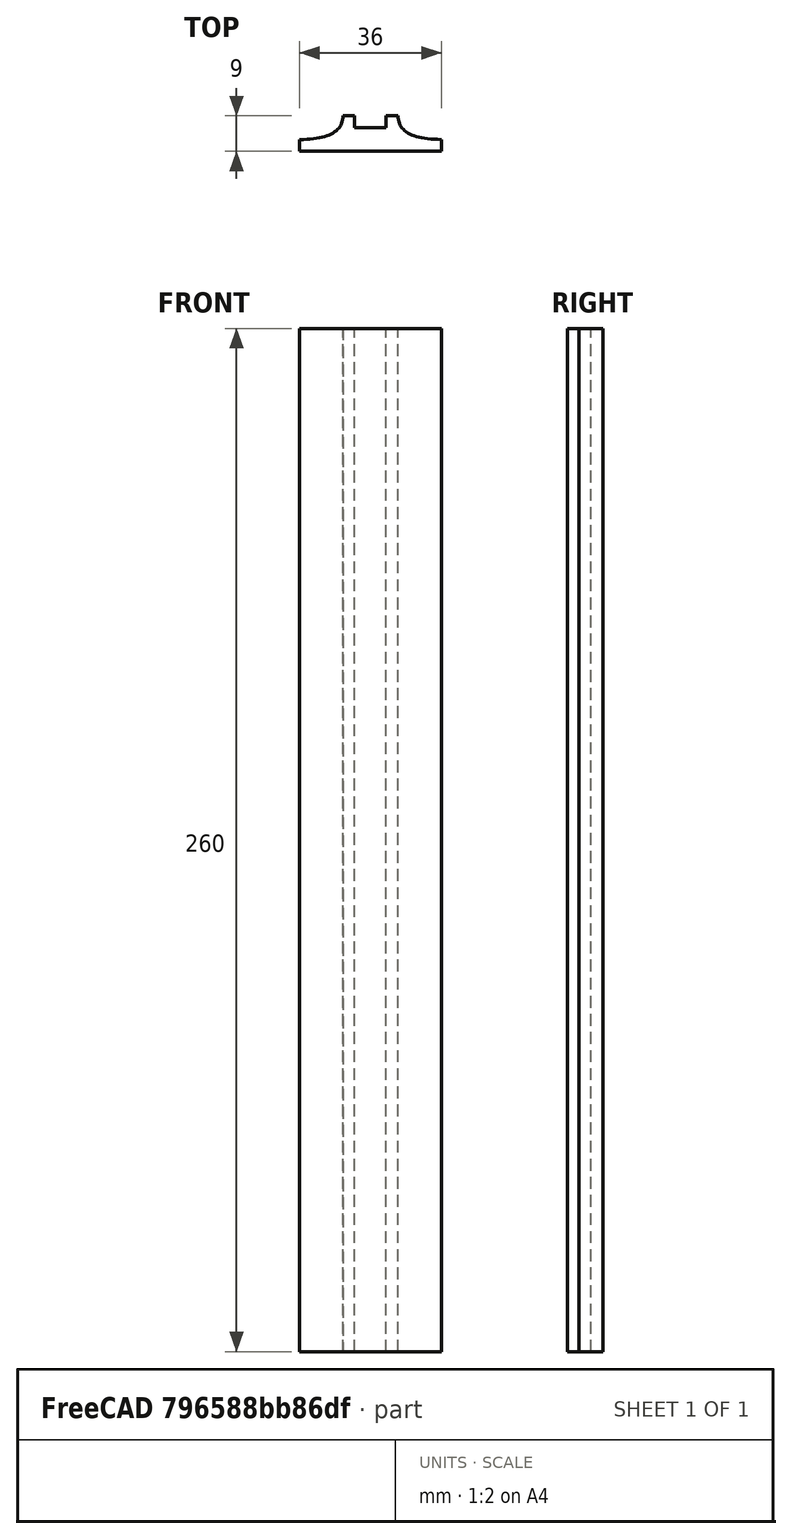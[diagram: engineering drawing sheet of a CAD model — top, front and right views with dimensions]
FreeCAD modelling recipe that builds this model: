
FCSTD DOCUMENT  (FreeCAD 0.19R0.19.2)
Label: laptopStand293.FCStd
License: All rights reserved
LicenseURL: http://en.wikipedia.org/wiki/All_rights_reserved
objects: Sketcher::SketchObject×10, Part::Extrusion×1
note: 11 computed .brp shape members not serialized (recipe doc carries the construction recipe); baked Part::Feature solids carry a one-line shape summary decoded from their .brp

FEATURE [Sketcher::SketchObject] Sketch001  label="legTop"
  FullyConstrained = false
  MapMode = 4
  Placement = pos=(0,0,0) rot=(0.57735,0.57735,0.57735;2.0944rad)
  sketch-geometry (59):
    g0: BSplineCurve PolesCount=3 KnotsCount=2 Degree=2 IsPeriodic=0
    g1: ArcOfCircle CenterX=73.1223 CenterY=-32.291 CenterZ=0 NormalX=0 NormalY=0 NormalZ=1 AngleXU=0 Radius=13 StartAngle=5.92268 EndAngle=9.06428
    g2: ArcOfCircle CenterX=66.7816 CenterY=-49.1439 CenterZ=0 NormalX=0 NormalY=0 NormalZ=1 AngleXU=0 Radius=13 StartAngle=2.78068 EndAngle=5.92131
    g3-g6: Circle x4 (B-spline internal-alignment scaffolding for g7; pole/knot coordinates omitted)
    g7: BSplineCurve PolesCount=4 KnotsCount=2 Degree=3 IsPeriodic=0
    g8: GeomPoint X=28.8094 Y=-19.0875 Z=0
    g9: GeomPoint X=47.0443 Y=-50.4712 Z=0
    g10: Circle CenterX=53.5586 CenterY=-23.2695 CenterZ=0 NormalX=0 NormalY=0 NormalZ=1 AngleXU=0 Radius=3.24518
    g11: LineSegment StartX=117.223 StartY=-19.0875 StartZ=0 EndX=117.223 EndY=-16.0875 EndZ=0
    g12: LineSegment StartX=117.223 StartY=-16.0875 StartZ=0 EndX=17.2232 EndY=-16.0875 EndZ=0
    g13: LineSegment StartX=17.2232 StartY=-16.0875 StartZ=0 EndX=17.2232 EndY=-19.0875 EndZ=0
    g14: LineSegment StartX=28.8094 StartY=-19.0875 StartZ=0 EndX=17.2232 EndY=-19.0875 EndZ=0
    g15: LineSegment StartX=85.2866 StartY=-36.8766 StartZ=0 EndX=78.9396 EndY=-53.7463 EndZ=0
    g16: LineSegment StartX=60.9579 StartY=-27.7053 StartZ=0 EndX=54.6191 EndY=-44.5532 EndZ=0
    g17: BSplineCurve PolesCount=3 KnotsCount=2 Degree=2 IsPeriodic=0
    g18: Circle CenterX=-199.665 CenterY=-138.314 CenterZ=0 NormalX=0 NormalY=0 NormalZ=1 AngleXU=0 Radius=1
    g19: GeomPoint X=-199.665 Y=-138.314 Z=0
    g20: LineSegment StartX=-199.665 StartY=-138.314 StartZ=0 EndX=-200.721 EndY=-141.122 EndZ=0
    g21: Circle CenterX=-17.0256 CenterY=-190.268 CenterZ=0 NormalX=0 NormalY=0 NormalZ=1 AngleXU=0 Radius=10.5072
    g22: Circle CenterX=-37.7758 CenterY=-187.672 CenterZ=0 NormalX=0 NormalY=0 NormalZ=1 AngleXU=0 Radius=5.64388
    g23: Circle CenterX=-51.4606 CenterY=-185.091 CenterZ=0 NormalX=0 NormalY=0 NormalZ=1 AngleXU=0 Radius=3.01653
    g24: Circle CenterX=-60.4835 CenterY=-182.688 CenterZ=0 NormalX=0 NormalY=0 NormalZ=1 AngleXU=0 Radius=2.12826
    g25: Circle CenterX=-3.29005 CenterY=-177.662 CenterZ=0 NormalX=0 NormalY=0 NormalZ=1 AngleXU=0 Radius=3.26661
    g26: ArcOfCircle CenterX=11.0205 CenterY=-198.019 CenterZ=0 NormalX=0 NormalY=0 NormalZ=1 AngleXU=0 Radius=13 StartAngle=2.78068 EndAngle=5.92131
    g27: LineSegment StartX=5.08312 StartY=-176.581 StartZ=0 EndX=-1.14188 EndY=-193.429 EndZ=0
    g28: LineSegment StartX=29.4118 StartY=-185.752 StartZ=0 EndX=23.1786 EndY=-202.622 EndZ=0
    g29: ArcOfCircle CenterX=17.2475 CenterY=-181.166 CenterZ=0 NormalX=0 NormalY=0 NormalZ=1 AngleXU=0 Radius=13 StartAngle=5.92268 EndAngle=9.06428
    g30: LineSegment StartX=38.8952 StartY=-231.233 StartZ=0 EndX=-200.721 EndY=-141.122 EndZ=0
    g31: LineSegment StartX=38.8952 StartY=-231.233 StartZ=0 EndX=39.9512 EndY=-228.425 EndZ=0
    g32: ArcOfCircle CenterX=46.9911 CenterY=-209.705 CenterZ=0 NormalX=0 NormalY=0 NormalZ=1 AngleXU=0 Radius=20 StartAngle=2.78766 EndAngle=4.35269
    g33: LineSegment StartX=23.7323 StartY=-126.969 StartZ=0 EndX=17.4091 EndY=-143.817 EndZ=0
    g34: ArcOfCircle CenterX=29.5716 CenterY=-148.408 CenterZ=0 NormalX=0 NormalY=0 NormalZ=1 AngleXU=0 Radius=13 StartAngle=2.78068 EndAngle=5.92131
    g35: ArcOfCircle CenterX=35.8967 CenterY=-131.555 CenterZ=0 NormalX=0 NormalY=0 NormalZ=1 AngleXU=0 Radius=13 StartAngle=5.92268 EndAngle=9.06428
    g36: ArcOfCircle CenterX=48.1805 CenterY=-98.7782 CenterZ=0 NormalX=0 NormalY=0 NormalZ=1 AngleXU=0 Radius=13 StartAngle=2.78068 EndAngle=5.92131
    g37: LineSegment StartX=42.354 StartY=-77.3391 StartZ=0 EndX=36.018 EndY=-94.1875 EndZ=0
    g38: ArcOfCircle CenterX=54.5183 CenterY=-81.9247 CenterZ=0 NormalX=0 NormalY=0 NormalZ=1 AngleXU=0 Radius=13 StartAngle=5.92268 EndAngle=9.06428
    g39: LineSegment StartX=66.6827 StartY=-86.5104 StartZ=0 EndX=60.3386 EndY=-103.381 EndZ=0
    g40: LineSegment StartX=48.061 StartY=-136.14 StartZ=0 EndX=41.7296 EndY=-153.01 EndZ=0
    g41: LineSegment StartX=28.2308 StartY=-202.773 StartZ=0 EndX=94.6579 EndY=-26.1359 EndZ=0
    g42: LineSegment StartX=47.0443 StartY=-50.4712 StartZ=0 EndX=8.65492 EndY=-152.553 EndZ=0
    g43: LineSegment StartX=23.1786 StartY=-202.622 StartZ=0 EndX=19.0195 EndY=-213.878 EndZ=0
    g44: ArcOfCircle CenterX=20.184 CenterY=-217.506 CenterZ=0 NormalX=0 NormalY=0 NormalZ=1 AngleXU=0 Radius=3.81084 StartAngle=1.88136 EndAngle=6.80465
    g45: LineSegment StartX=28.2308 StartY=-202.773 StartZ=0 EndX=23.4884 EndY=-215.608 EndZ=0
    g46: LineSegment StartX=41.2852 StartY=-117.017 StartZ=0 EndX=40.4092 EndY=-119.359 EndZ=0
    g47: LineSegment StartX=38.4753 StartY=-115.966 StartZ=0 EndX=41.2852 EndY=-117.017 EndZ=0
    g48: ArcOfCircle CenterX=36.3663 CenterY=-113.042 CenterZ=0 NormalX=0 NormalY=0 NormalZ=1 AngleXU=0 Radius=3.60555 StartAngle=0.230024 EndAngle=5.3372
    g49: LineSegment StartX=39.8769 StartY=-112.22 StartZ=0 EndX=42.6867 EndY=-113.271 EndZ=0
    g50: LineSegment StartX=42.6867 StartY=-113.271 StartZ=0 EndX=43.5628 EndY=-110.929 EndZ=0
    g51: LineSegment StartX=22.7134 StartY=-166.661 StartZ=0 EndX=21.8375 EndY=-169.003 EndZ=0
    g52: LineSegment StartX=19.9036 StartY=-165.61 StartZ=0 EndX=22.7134 EndY=-166.661 EndZ=0
    g53: ArcOfCircle CenterX=17.7945 CenterY=-162.686 CenterZ=0 NormalX=0 NormalY=0 NormalZ=1 AngleXU=0 Radius=3.60555 StartAngle=0.230024 EndAngle=5.3372
    g54: LineSegment StartX=21.3051 StartY=-161.864 StartZ=0 EndX=24.1149 EndY=-162.915 EndZ=0
    g55: LineSegment StartX=24.1149 StartY=-162.915 StartZ=0 EndX=24.991 EndY=-160.573 EndZ=0
    g56: LineSegment StartX=41.085 StartY=-66.3176 StartZ=0 EndX=46.0385 EndY=-62.5254 EndZ=0
    g57: LineSegment StartX=48.9563 StartY=-66.3367 StartZ=0 EndX=44.7488 EndY=-73.3482 EndZ=0
    g58: ArcOfCircle CenterX=49.8795 CenterY=-62.6074 CenterZ=0 NormalX=0 NormalY=0 NormalZ=1 AngleXU=0 Radius=3.84187 StartAngle=4.46973 EndAngle=9.40343
  constraints (101):
    c: Block(g0)
    c: Block(g1)
    c: Block(g2)
    c: Weight(g3) = 1
    c: Equal(g3,g4)
    c: Equal(g3,g5)
    c: Equal(g3,g6)
    c: InternalAlignment(g3-g6 -> g7) x4
    c: InternalAlignment(g8,g7)
    c: InternalAlignment(g9,g7)
    c: Block(g10)
    c: Block(g7)
    c: Coincident(g11,g0)
    c: Vertical(g11)
    c: Coincident(g12,g11)
    c: Horizontal(g12)
    c: Coincident(g13,g12)
    c: Vertical(g13)
    c: Block(g12)
    c: Coincident(g14,g7)
    c: Coincident(g14,g13)
    c: Horizontal(g14)
    c: Coincident(g15,g1)
    c: Coincident(g15,g2)
    c: Coincident(g16,g1)
    c: Coincident(g16,g2)
    c: Distance(g12) = 100
    c: Block(g26)
    c: Block(g29)
    c: InternalAlignment(g18,g17)
    c: InternalAlignment(g19,g17)
    c: Block(g17)
    c: Block(g21)
    c: Block(g25)
    c: Block(g22)
    c: Block(g23)
    c: Block(g24)
    c: Block(g32)
    c: Coincident(g31,g30)
    c: Coincident(g31,g32)
    c: Block(g31)
    c: Coincident(g20,g17)
    c: Coincident(g20,g30)
    c: Block(g30)
    c: Coincident(g27,g29)
    c: Coincident(g27,g26)
    c: Coincident(g28,g29)
    c: Coincident(g28,g26)
    c: Block(g34)
    c: Block(g35)
    c: Coincident(g33,g35)
    c: Coincident(g33,g34)
    c: Block(g36)
    c: Block(g38)
    c: Coincident(g37,g38)
    c: Coincident(g37,g36)
    c: Coincident(g39,g38)
    c: Coincident(g39,g36)
    c: Coincident(g40,g35)
    c: Coincident(g40,g34)
    c: Coincident(g41,g32)
    c: Coincident(g41,g0)
    c: Coincident(g42,g7)
    c: Coincident(g42,g17)
    c: Coincident(g43,g26)
    c: Parallel(g28,g43)
    c: Distance(g43) = 12
    c: Block(g28)
    c: Coincident(g44,g43)
    c: Block(g44)
    c: Coincident(g45,g32)
    c: Coincident(g45,g44)
    c: Tangent(g45,g32)
    c: Parallel(g45,g43)
    c: Block(g45)
    c: Block(g48)
    c: Coincident(g49,g48)
    c: Coincident(g47,g48)
    c: Parallel(g49,g47)
    c: Coincident(g46,g47)
    c: Coincident(g50,g49)
    c: Block(g50)
    c: Block(g46)
    c: Block(g47)
    c: Block(g49)
    c: Block(g53)
    c: Coincident(g54,g53)
    c: Coincident(g52,g53)
    c: Parallel(g54,g52)
    c: Coincident(g51,g52)
    c: Coincident(g55,g54)
    c: Block(g55)
    c: Block(g51)
    c: Block(g52)
    c: Block(g54)
    c: PointOnObject(g56,g42)
    c: Block(g56)
    c: PointOnObject(g57,g38)
    c: Coincident(g58,g56)
    c: Coincident(g58,g57)
    c: Block(g58)
FEATURE [Sketcher::SketchObject] Sketch002
  FullyConstrained = true
  sketch-geometry (20):
    g0: LineSegment StartX=-2.77179 StartY=-200.304 StartZ=0 EndX=5.22821 EndY=-200.304 EndZ=0
    g1: LineSegment StartX=5.22821 StartY=-200.304 StartZ=0 EndX=5.22821 EndY=-197.304 EndZ=0
    g2: LineSegment StartX=-2.77179 StartY=-200.304 StartZ=0 EndX=-2.77179 EndY=-197.304 EndZ=0
    g3: LineSegment StartX=5.22821 StartY=-197.304 StartZ=0 EndX=8.22821 EndY=-197.304 EndZ=0
    g4: LineSegment StartX=-2.77179 StartY=-197.304 StartZ=0 EndX=-5.77179 EndY=-197.304 EndZ=0
    g5: LineSegment StartX=19.2282 StartY=-203.304 StartZ=0 EndX=19.2282 EndY=-206.304 EndZ=0
    g6: LineSegment StartX=-16.7718 StartY=-203.304 StartZ=0 EndX=-16.7718 EndY=-206.304 EndZ=0
    g7: LineSegment StartX=-16.7718 StartY=-206.304 StartZ=0 EndX=19.2282 EndY=-206.304 EndZ=0
    g8: Circle CenterX=-16.7718 CenterY=-203.304 CenterZ=0 NormalX=0 NormalY=0 NormalZ=1 AngleXU=0 Radius=1
    g9: Circle CenterX=-5.77179 CenterY=-203.304 CenterZ=0 NormalX=0 NormalY=0 NormalZ=1 AngleXU=0 Radius=1
    g10: Circle CenterX=-5.77179 CenterY=-197.304 CenterZ=0 NormalX=0 NormalY=0 NormalZ=1 AngleXU=0 Radius=1
    g11: BSplineCurve PolesCount=3 KnotsCount=2 Degree=2 IsPeriodic=0
    g12: GeomPoint X=-16.7718 Y=-203.304 Z=0
    g13: GeomPoint X=-5.77179 Y=-197.304 Z=0
    g14: Circle CenterX=19.2282 CenterY=-203.304 CenterZ=0 NormalX=0 NormalY=0 NormalZ=1 AngleXU=0 Radius=1
    g15: Circle CenterX=8.22821 CenterY=-203.304 CenterZ=0 NormalX=0 NormalY=0 NormalZ=1 AngleXU=0 Radius=1
    g16: Circle CenterX=8.22821 CenterY=-197.304 CenterZ=0 NormalX=0 NormalY=0 NormalZ=1 AngleXU=0 Radius=1
    g17: BSplineCurve PolesCount=3 KnotsCount=2 Degree=2 IsPeriodic=0
    g18: GeomPoint X=19.2282 Y=-203.304 Z=0
    g19: GeomPoint X=8.22821 Y=-197.304 Z=0
  constraints (41):
    c: Horizontal(g0)
    c: Distance(g0) = 8
    c: Coincident(g1,g0)
    c: Vertical(g1)
    c: Distance(g1) = 3
    c: Coincident(g2,g0)
    c: Vertical(g2)
    c: Distance(g2) = 3
    c: Coincident(g3,g1)
    c: Horizontal(g3)
    c: Distance(g3) = 3
    c: Coincident(g4,g2)
    c: Horizontal(g4)
    c: Distance(g4) = 3
    c: Vertical(g5)
    c: Vertical(g6)
    c: Coincident(g7,g6)
    c: Coincident(g7,g5)
    c: Weight(g8) = 1
    c: Equal(g8,g9)
    c: Equal(g8,g10)
    c: Coincident(g11,g4)
    c: InternalAlignment(g8,g11)
    c: InternalAlignment(g9,g11)
    c: InternalAlignment(g10,g11)
    c: InternalAlignment(g12,g11)
    c: InternalAlignment(g13,g11)
    c: Coincident(g17,g5)
    c: Weight(g14) = 1
    c: Equal(g14,g15)
    c: Equal(g14,g16)
    c: Coincident(g17,g3)
    c: InternalAlignment(g14,g17)
    c: InternalAlignment(g15,g17)
    c: InternalAlignment(g16,g17)
    c: InternalAlignment(g18,g17)
    c: InternalAlignment(g19,g17)
    c: Block(g7)
    c: Block(g17)
    c: Block(g11)
    c: Block(g6)
FEATURE [Part::Extrusion] Extrude003
  Base = -> Sketch002
  Dir = (0,0,1)
  DirMode = 2
  FaceMakerClass = Part::FaceMakerBullseye
  LengthFwd = 260
  LengthRev = 0
  Solid = true
  Symmetric = false
FEATURE [Sketcher::SketchObject] Sketch003  label="original"
  FullyConstrained = false
  sketch-geometry (469):
    g0: LineSegment StartX=-42.9272 StartY=136.221 StartZ=0 EndX=-42.9272 EndY=-103.779 EndZ=0
    g1: LineSegment StartX=407.073 StartY=136.221 StartZ=0 EndX=407.073 EndY=-103.779 EndZ=0
    g2: ArcOfCircle CenterX=-26.9272 CenterY=-83.7794 CenterZ=0 NormalX=0 NormalY=0 NormalZ=1 AngleXU=0 Radius=8 StartAngle=3.14159 EndAngle=6.28319
    g3: ArcOfCircle CenterX=391.073 CenterY=-83.7794 CenterZ=0 NormalX=0 NormalY=0 NormalZ=1 AngleXU=0 Radius=8 StartAngle=3.14159 EndAngle=6.28319
    g4: Circle CenterX=175.022 CenterY=27.0628 CenterZ=0 NormalX=0 NormalY=0 NormalZ=1 AngleXU=0 Radius=1
    g5: Circle CenterX=179.022 CenterY=24.8665 CenterZ=0 NormalX=0 NormalY=0 NormalZ=1 AngleXU=0 Radius=1
    g6: Circle CenterX=179.022 CenterY=27.0628 CenterZ=0 NormalX=0 NormalY=0 NormalZ=1 AngleXU=0 Radius=1
    g7: BSplineCurve PolesCount=3 KnotsCount=2 Degree=2 IsPeriodic=0
    g8: GeomPoint X=175.022 Y=27.0628 Z=0
    g9: GeomPoint X=179.022 Y=27.0628 Z=0
    g10: Circle CenterX=189.124 CenterY=27.0628 CenterZ=0 NormalX=0 NormalY=0 NormalZ=1 AngleXU=0 Radius=1
    g11: Circle CenterX=185.124 CenterY=24.8665 CenterZ=0 NormalX=0 NormalY=0 NormalZ=1 AngleXU=0 Radius=1
    g12: Circle CenterX=185.124 CenterY=27.0628 CenterZ=0 NormalX=0 NormalY=0 NormalZ=1 AngleXU=0 Radius=1
    g13: BSplineCurve PolesCount=3 KnotsCount=2 Degree=2 IsPeriodic=0
    g14: GeomPoint X=189.124 Y=27.0628 Z=0
    g15: GeomPoint X=185.124 Y=27.0628 Z=0
    g16: Circle CenterX=175.022 CenterY=5.37834 CenterZ=0 NormalX=0 NormalY=0 NormalZ=1 AngleXU=0 Radius=1
    g17: Circle CenterX=179.022 CenterY=7.57463 CenterZ=0 NormalX=0 NormalY=0 NormalZ=1 AngleXU=0 Radius=1
    g18: Circle CenterX=179.022 CenterY=5.34704 CenterZ=0 NormalX=0 NormalY=0 NormalZ=1 AngleXU=0 Radius=1
    g19: BSplineCurve PolesCount=3 KnotsCount=2 Degree=2 IsPeriodic=0
    g20: GeomPoint X=175.022 Y=5.37834 Z=0
    g21: GeomPoint X=179.022 Y=5.34704 Z=0
    g22: Circle CenterX=189.124 CenterY=5.37834 CenterZ=0 NormalX=0 NormalY=0 NormalZ=1 AngleXU=0 Radius=1
    g23: Circle CenterX=185.124 CenterY=7.57463 CenterZ=0 NormalX=0 NormalY=0 NormalZ=1 AngleXU=0 Radius=1
    g24: Circle CenterX=185.124 CenterY=5.34704 CenterZ=0 NormalX=0 NormalY=0 NormalZ=1 AngleXU=0 Radius=1
    g25: BSplineCurve PolesCount=3 KnotsCount=2 Degree=2 IsPeriodic=0
    g26: GeomPoint X=189.124 Y=5.37834 Z=0
    g27: GeomPoint X=185.124 Y=5.34704 Z=0
    g28: Circle CenterX=165.871 CenterY=18.1458 CenterZ=0 NormalX=0 NormalY=0 NormalZ=1 AngleXU=0 Radius=1
    g29: Circle CenterX=169.377 CenterY=16.2206 CenterZ=0 NormalX=0 NormalY=0 NormalZ=1 AngleXU=0 Radius=1
    g30: Circle CenterX=165.871 CenterY=14.2956 CenterZ=0 NormalX=0 NormalY=0 NormalZ=1 AngleXU=0 Radius=1
    g31: BSplineCurve PolesCount=3 KnotsCount=2 Degree=2 IsPeriodic=0
    g32: GeomPoint X=165.871 Y=18.1458 Z=0
    g33: GeomPoint X=165.871 Y=14.2956 Z=0
    g34: Circle CenterX=198.275 CenterY=18.1318 CenterZ=0 NormalX=0 NormalY=0 NormalZ=1 AngleXU=0 Radius=1
    g35: Circle CenterX=194.768 CenterY=16.2206 CenterZ=0 NormalX=0 NormalY=0 NormalZ=1 AngleXU=0 Radius=1
    g36: Circle CenterX=198.264 CenterY=14.2963 CenterZ=0 NormalX=0 NormalY=0 NormalZ=1 AngleXU=0 Radius=1
    g37: BSplineCurve PolesCount=3 KnotsCount=2 Degree=2 IsPeriodic=0
    g38: GeomPoint X=198.275 Y=18.1318 Z=0
    g39: GeomPoint X=198.264 Y=14.2963 Z=0
    g40: LineSegment StartX=407.073 StartY=-103.779 StartZ=0 EndX=-42.9272 EndY=-103.779 EndZ=0
    g41: Circle CenterX=125.607 CenterY=54.1951 CenterZ=0 NormalX=0 NormalY=0 NormalZ=1 AngleXU=0 Radius=1
    g42: Circle CenterX=139.632 CenterY=46.4944 CenterZ=0 NormalX=0 NormalY=0 NormalZ=1 AngleXU=0 Radius=1
    g43: Circle CenterX=127.326 CenterY=56.7187 CenterZ=0 NormalX=0 NormalY=0 NormalZ=1 AngleXU=0 Radius=1
    g44: BSplineCurve PolesCount=3 KnotsCount=2 Degree=2 IsPeriodic=0
    g45: GeomPoint X=125.607 Y=54.1951 Z=0
    g46: GeomPoint X=127.326 Y=56.7187 Z=0
    g47: Circle CenterX=236.824 CenterY=56.7187 CenterZ=0 NormalX=0 NormalY=0 NormalZ=1 AngleXU=0 Radius=1
    g48: Circle CenterX=224.513 CenterY=46.4944 CenterZ=0 NormalX=0 NormalY=0 NormalZ=1 AngleXU=0 Radius=1
    g49: Circle CenterX=238.538 CenterY=54.1951 CenterZ=0 NormalX=0 NormalY=0 NormalZ=1 AngleXU=0 Radius=1
    g50: BSplineCurve PolesCount=3 KnotsCount=2 Degree=2 IsPeriodic=0
    g51: GeomPoint X=236.824 Y=56.7187 Z=0
    g52: GeomPoint X=238.538 Y=54.1951 Z=0
    g53: Circle CenterX=238.538 CenterY=-21.7516 CenterZ=0 NormalX=0 NormalY=0 NormalZ=1 AngleXU=0 Radius=1
    g54: Circle CenterX=224.513 CenterY=-14.0532 CenterZ=0 NormalX=0 NormalY=0 NormalZ=1 AngleXU=0 Radius=1
    g55: Circle CenterX=236.584 CenterY=-24.2775 CenterZ=0 NormalX=0 NormalY=0 NormalZ=1 AngleXU=0 Radius=1
    g56: BSplineCurve PolesCount=3 KnotsCount=2 Degree=2 IsPeriodic=0
    g57: GeomPoint X=238.538 Y=-21.7516 Z=0
    g58: GeomPoint X=236.584 Y=-24.2775 Z=0
    g59: Circle CenterX=125.607 CenterY=-21.7539 CenterZ=0 NormalX=0 NormalY=0 NormalZ=1 AngleXU=0 Radius=1
    g60: Circle CenterX=139.632 CenterY=-14.0532 CenterZ=0 NormalX=0 NormalY=0 NormalZ=1 AngleXU=0 Radius=1
    g61: Circle CenterX=127.325 CenterY=-24.2775 CenterZ=0 NormalX=0 NormalY=0 NormalZ=1 AngleXU=0 Radius=1
    g62: BSplineCurve PolesCount=3 KnotsCount=2 Degree=2 IsPeriodic=0
    g63: GeomPoint X=125.607 Y=-21.7539 Z=0
    g64: GeomPoint X=127.325 Y=-24.2775 Z=0
    g65: Circle CenterX=302.996 CenterY=111.695 CenterZ=0 NormalX=0 NormalY=0 NormalZ=1 AngleXU=0 Radius=1
    g66: Circle CenterX=306.073 CenterY=114.251 CenterZ=0 NormalX=0 NormalY=0 NormalZ=1 AngleXU=0 Radius=1
    g67: Circle CenterX=306.073 CenterY=110.251 CenterZ=0 NormalX=0 NormalY=0 NormalZ=1 AngleXU=0 Radius=1
    g68: BSplineCurve PolesCount=3 KnotsCount=2 Degree=2 IsPeriodic=0
    g69: GeomPoint X=302.996 Y=111.695 Z=0
    g70: GeomPoint X=306.073 Y=110.251 Z=0
    g71: Circle CenterX=306.073 CenterY=95.2763 CenterZ=0 NormalX=0 NormalY=0 NormalZ=1 AngleXU=0 Radius=1
    g72: Circle CenterX=306.073 CenterY=91.2763 CenterZ=0 NormalX=0 NormalY=0 NormalZ=1 AngleXU=0 Radius=1
    g73: Circle CenterX=302.567 CenterY=89.3511 CenterZ=0 NormalX=0 NormalY=0 NormalZ=1 AngleXU=0 Radius=1
    g74: BSplineCurve PolesCount=3 KnotsCount=2 Degree=2 IsPeriodic=0
    g75: GeomPoint X=306.073 Y=95.2763 Z=0
    g76: GeomPoint X=302.567 Y=89.3511 Z=0
    g77: LineSegment StartX=306.073 StartY=110.251 StartZ=0 EndX=306.073 EndY=95.2763 EndZ=0
    g78: LineSegment StartX=302.996 StartY=111.695 StartZ=0 EndX=236.824 EndY=56.7187 EndZ=0
    g79: LineSegment StartX=238.538 StartY=54.1951 StartZ=0 EndX=302.567 EndY=89.3511 EndZ=0
    g80: Circle CenterX=61.1496 CenterY=111.695 CenterZ=0 NormalX=0 NormalY=0 NormalZ=1 AngleXU=0 Radius=1
    g81: Circle CenterX=58.0728 CenterY=114.251 CenterZ=0 NormalX=0 NormalY=0 NormalZ=1 AngleXU=0 Radius=1
    g82: Circle CenterX=58.0728 CenterY=110.251 CenterZ=0 NormalX=0 NormalY=0 NormalZ=1 AngleXU=0 Radius=1
    g83: BSplineCurve PolesCount=3 KnotsCount=2 Degree=2 IsPeriodic=0
    g84: GeomPoint X=61.1496 Y=111.695 Z=0
    g85: GeomPoint X=58.0728 Y=110.251 Z=0
    g86: Circle CenterX=61.5791 CenterY=89.3511 CenterZ=0 NormalX=0 NormalY=0 NormalZ=1 AngleXU=0 Radius=1
    g87: Circle CenterX=58.0728 CenterY=91.2763 CenterZ=0 NormalX=0 NormalY=0 NormalZ=1 AngleXU=0 Radius=1
    g88: Circle CenterX=58.0728 CenterY=95.2763 CenterZ=0 NormalX=0 NormalY=0 NormalZ=1 AngleXU=0 Radius=1
    g89: BSplineCurve PolesCount=3 KnotsCount=2 Degree=2 IsPeriodic=0
    g90: GeomPoint X=61.5791 Y=89.3511 Z=0
    g91: GeomPoint X=58.0728 Y=95.2763 Z=0
    g92: LineSegment StartX=58.0728 StartY=110.251 StartZ=0 EndX=58.0728 EndY=95.2763 EndZ=0
    g93: LineSegment StartX=61.1496 StartY=111.695 StartZ=0 EndX=127.326 EndY=56.7187 EndZ=0
    g94: LineSegment StartX=125.607 StartY=54.1951 StartZ=0 EndX=61.5791 EndY=89.3511 EndZ=0
    g95: Circle CenterX=61.5791 CenterY=-56.9099 CenterZ=0 NormalX=0 NormalY=0 NormalZ=1 AngleXU=0 Radius=1
    g96: Circle CenterX=58.0728 CenterY=-58.8351 CenterZ=0 NormalX=0 NormalY=0 NormalZ=1 AngleXU=0 Radius=1
    g97: Circle CenterX=58.0728 CenterY=-62.8351 CenterZ=0 NormalX=0 NormalY=0 NormalZ=1 AngleXU=0 Radius=1
    g98: BSplineCurve PolesCount=3 KnotsCount=2 Degree=2 IsPeriodic=0
    g99: GeomPoint X=61.5791 Y=-56.9099 Z=0
    g100: GeomPoint X=58.0728 Y=-62.8351 Z=0
    g101: Circle CenterX=58.0728 CenterY=-77.8102 CenterZ=0 NormalX=0 NormalY=0 NormalZ=1 AngleXU=0 Radius=1
    g102: Circle CenterX=58.0728 CenterY=-81.8102 CenterZ=0 NormalX=0 NormalY=0 NormalZ=1 AngleXU=0 Radius=1
    g103: Circle CenterX=61.1496 CenterY=-79.2541 CenterZ=0 NormalX=0 NormalY=0 NormalZ=1 AngleXU=0 Radius=1
    g104: BSplineCurve PolesCount=3 KnotsCount=2 Degree=2 IsPeriodic=0
    g105: GeomPoint X=58.0728 Y=-77.8102 Z=0
    g106: GeomPoint X=61.1496 Y=-79.2541 Z=0
    g107: LineSegment StartX=58.0728 StartY=-62.8351 StartZ=0 EndX=58.0728 EndY=-77.8102 EndZ=0
    g108: LineSegment StartX=61.1496 StartY=-79.2541 StartZ=0 EndX=127.325 EndY=-24.2775 EndZ=0
    g109: LineSegment StartX=125.607 StartY=-21.7539 StartZ=0 EndX=61.5791 EndY=-56.9099 EndZ=0
    g110: Circle CenterX=302.567 CenterY=-56.9099 CenterZ=0 NormalX=0 NormalY=0 NormalZ=1 AngleXU=0 Radius=1
    g111: Circle CenterX=306.073 CenterY=-58.8351 CenterZ=0 NormalX=0 NormalY=0 NormalZ=1 AngleXU=0 Radius=1
    g112: Circle CenterX=306.073 CenterY=-62.8351 CenterZ=0 NormalX=0 NormalY=0 NormalZ=1 AngleXU=0 Radius=1
    g113: BSplineCurve PolesCount=3 KnotsCount=2 Degree=2 IsPeriodic=0
    g114: GeomPoint X=302.567 Y=-56.9099 Z=0
    g115: GeomPoint X=306.073 Y=-62.8351 Z=0
    g116: Circle CenterX=302.996 CenterY=-79.2541 CenterZ=0 NormalX=0 NormalY=0 NormalZ=1 AngleXU=0 Radius=1
    g117: Circle CenterX=306.073 CenterY=-81.8102 CenterZ=0 NormalX=0 NormalY=0 NormalZ=1 AngleXU=0 Radius=1
    g118: Circle CenterX=306.073 CenterY=-77.8102 CenterZ=0 NormalX=0 NormalY=0 NormalZ=1 AngleXU=0 Radius=1
    g119: BSplineCurve PolesCount=3 KnotsCount=2 Degree=2 IsPeriodic=0
    g120: GeomPoint X=302.996 Y=-79.2541 Z=0
    g121: GeomPoint X=306.073 Y=-77.8102 Z=0
    g122: LineSegment StartX=306.073 StartY=-62.8351 StartZ=0 EndX=306.073 EndY=-77.8102 EndZ=0
    g123: LineSegment StartX=302.996 StartY=-79.2541 StartZ=0 EndX=236.584 EndY=-24.2775 EndZ=0
    g124: LineSegment StartX=238.538 StartY=-21.7516 StartZ=0 EndX=302.567 EndY=-56.9099 EndZ=0
    g125: Circle CenterX=61.6457 CenterY=-88.8112 CenterZ=0 NormalX=0 NormalY=0 NormalZ=1 AngleXU=0 Radius=1
    g126: Circle CenterX=58.0728 CenterY=-91.7794 CenterZ=0 NormalX=0 NormalY=0 NormalZ=1 AngleXU=0 Radius=1
    g127: Circle CenterX=63.9135 CenterY=-91.7791 CenterZ=0 NormalX=0 NormalY=0 NormalZ=1 AngleXU=0 Radius=1
    g128: BSplineCurve PolesCount=3 KnotsCount=2 Degree=2 IsPeriodic=0
    g129: GeomPoint X=61.6457 Y=-88.8112 Z=0
    g130: GeomPoint X=63.9135 Y=-91.7791 Z=0
    g131: Circle CenterX=179.022 CenterY=-85.8163 CenterZ=0 NormalX=0 NormalY=0 NormalZ=1 AngleXU=0 Radius=1
    g132: Circle CenterX=179.022 CenterY=-91.7794 CenterZ=0 NormalX=0 NormalY=0 NormalZ=1 AngleXU=0 Radius=1
    g133: Circle CenterX=171.895 CenterY=-91.7791 CenterZ=0 NormalX=0 NormalY=0 NormalZ=1 AngleXU=0 Radius=1
    g134: BSplineCurve PolesCount=3 KnotsCount=2 Degree=2 IsPeriodic=0
    g135: GeomPoint X=179.022 Y=-85.8163 Z=0
    g136: GeomPoint X=171.895 Y=-91.7791 Z=0
    g137: Circle CenterX=185.124 CenterY=-86.2028 CenterZ=0 NormalX=0 NormalY=0 NormalZ=1 AngleXU=0 Radius=1
    g138: Circle CenterX=185.124 CenterY=-91.7794 CenterZ=0 NormalX=0 NormalY=0 NormalZ=1 AngleXU=0 Radius=1
    g139: Circle CenterX=191.747 CenterY=-91.7794 CenterZ=0 NormalX=0 NormalY=0 NormalZ=1 AngleXU=0 Radius=1
    g140: BSplineCurve PolesCount=3 KnotsCount=2 Degree=2 IsPeriodic=0
    g141: GeomPoint X=185.124 Y=-86.2028 Z=0
    g142: GeomPoint X=191.747 Y=-91.7794 Z=0
    g143: Circle CenterX=299.888 CenterY=-86.6413 CenterZ=0 NormalX=0 NormalY=0 NormalZ=1 AngleXU=0 Radius=1
    g144: Circle CenterX=306.073 CenterY=-91.7794 CenterZ=0 NormalX=0 NormalY=0 NormalZ=1 AngleXU=0 Radius=1
    g145: Circle CenterX=298.776 CenterY=-91.7794 CenterZ=0 NormalX=0 NormalY=0 NormalZ=1 AngleXU=0 Radius=1
    g146: BSplineCurve PolesCount=3 KnotsCount=2 Degree=2 IsPeriodic=0
    g147: GeomPoint X=299.888 Y=-86.6413 Z=0
    g148: GeomPoint X=298.776 Y=-91.7794 Z=0
    g149: LineSegment StartX=189.124 StartY=5.37834 StartZ=0 EndX=299.888 EndY=-86.6413 EndZ=0
    g150: LineSegment StartX=298.776 StartY=-91.7794 StartZ=0 EndX=191.747 EndY=-91.7794 EndZ=0
    g151: LineSegment StartX=185.124 StartY=-86.2028 StartZ=0 EndX=185.124 EndY=5.34704 EndZ=0
    g152: LineSegment StartX=179.022 StartY=5.34704 StartZ=0 EndX=179.022 EndY=-85.8163 EndZ=0
    g153: LineSegment StartX=171.895 StartY=-91.7791 StartZ=0 EndX=63.9135 EndY=-91.7791 EndZ=0
    g154: LineSegment StartX=61.6457 StartY=-88.8112 StartZ=0 EndX=175.022 EndY=5.37834 EndZ=0
    g155: Circle CenterX=302.073 CenterY=124.221 CenterZ=0 NormalX=0 NormalY=0 NormalZ=1 AngleXU=0 Radius=1
    g156: Circle CenterX=306.073 CenterY=124.221 CenterZ=0 NormalX=0 NormalY=0 NormalZ=1 AngleXU=0 Radius=1
    g157: Circle CenterX=302.996 CenterY=121.665 CenterZ=0 NormalX=0 NormalY=0 NormalZ=1 AngleXU=0 Radius=1
    g158: BSplineCurve PolesCount=3 KnotsCount=2 Degree=2 IsPeriodic=0
    g159: GeomPoint X=302.073 Y=124.221 Z=0
    g160: GeomPoint X=302.996 Y=121.665 Z=0
    g161: Circle CenterX=189.124 CenterY=124.221 CenterZ=0 NormalX=0 NormalY=0 NormalZ=1 AngleXU=0 Radius=1
    g162: Circle CenterX=185.124 CenterY=124.221 CenterZ=0 NormalX=0 NormalY=0 NormalZ=1 AngleXU=0 Radius=1
    g163: Circle CenterX=185.124 CenterY=120.221 CenterZ=0 NormalX=0 NormalY=0 NormalZ=1 AngleXU=0 Radius=1
    g164: BSplineCurve PolesCount=3 KnotsCount=2 Degree=2 IsPeriodic=0
    g165: GeomPoint X=189.124 Y=124.221 Z=0
    g166: GeomPoint X=185.124 Y=120.221 Z=0
    g167: Circle CenterX=175.022 CenterY=124.221 CenterZ=0 NormalX=0 NormalY=0 NormalZ=1 AngleXU=0 Radius=1
    g168: Circle CenterX=179.022 CenterY=124.221 CenterZ=0 NormalX=0 NormalY=0 NormalZ=1 AngleXU=0 Radius=1
    g169: Circle CenterX=179.022 CenterY=120.221 CenterZ=0 NormalX=0 NormalY=0 NormalZ=1 AngleXU=0 Radius=1
    g170: BSplineCurve PolesCount=3 KnotsCount=2 Degree=2 IsPeriodic=0
    g171: GeomPoint X=175.022 Y=124.221 Z=0
    g172: GeomPoint X=179.022 Y=120.221 Z=0
    g173: Circle CenterX=62.0728 CenterY=124.221 CenterZ=0 NormalX=0 NormalY=0 NormalZ=1 AngleXU=0 Radius=1
    g174: Circle CenterX=58.0728 CenterY=124.221 CenterZ=0 NormalX=0 NormalY=0 NormalZ=1 AngleXU=0 Radius=1
    g175: Circle CenterX=61.1496 CenterY=121.665 CenterZ=0 NormalX=0 NormalY=0 NormalZ=1 AngleXU=0 Radius=1
    g176: BSplineCurve PolesCount=3 KnotsCount=2 Degree=2 IsPeriodic=0
    g177: GeomPoint X=62.0728 Y=124.221 Z=0
    g178: GeomPoint X=61.1496 Y=121.665 Z=0
    g179: LineSegment StartX=179.022 StartY=120.221 StartZ=0 EndX=179.022 EndY=27.0628 EndZ=0
    g180: LineSegment StartX=185.124 StartY=27.0628 StartZ=0 EndX=185.124 EndY=120.221 EndZ=0
    g181: LineSegment StartX=302.996 StartY=121.665 StartZ=0 EndX=189.124 EndY=27.0628 EndZ=0
    g182: LineSegment StartX=175.022 StartY=27.0628 StartZ=0 EndX=61.1496 EndY=121.665 EndZ=0
    g183: Circle CenterX=61.5791 CenterY=75.4095 CenterZ=0 NormalX=0 NormalY=0 NormalZ=1 AngleXU=0 Radius=1
    g184: Circle CenterX=58.0728 CenterY=77.3346 CenterZ=0 NormalX=0 NormalY=0 NormalZ=1 AngleXU=0 Radius=1
    g185: Circle CenterX=58.0728 CenterY=73.3346 CenterZ=0 NormalX=0 NormalY=0 NormalZ=1 AngleXU=0 Radius=1
    g186: BSplineCurve PolesCount=3 KnotsCount=2 Degree=2 IsPeriodic=0
    g187: GeomPoint X=61.5791 Y=75.4095 Z=0
    g188: GeomPoint X=58.0728 Y=73.3346 Z=0
    g189: Circle CenterX=58.0728 CenterY=-40.8935 CenterZ=0 NormalX=0 NormalY=0 NormalZ=1 AngleXU=0 Radius=1
    g190: Circle CenterX=58.0728 CenterY=-44.8935 CenterZ=0 NormalX=0 NormalY=0 NormalZ=1 AngleXU=0 Radius=1
    g191: Circle CenterX=61.5791 CenterY=-42.9683 CenterZ=0 NormalX=0 NormalY=0 NormalZ=1 AngleXU=0 Radius=1
    g192: BSplineCurve PolesCount=3 KnotsCount=2 Degree=2 IsPeriodic=0
    g193: GeomPoint X=58.0728 Y=-40.8935 Z=0
    g194: GeomPoint X=61.5791 Y=-42.9683 Z=0
    g195: LineSegment StartX=61.5791 StartY=-42.9683 StartZ=0 EndX=165.871 EndY=14.2956 EndZ=0
    g196: LineSegment StartX=165.871 StartY=18.1458 StartZ=0 EndX=61.5791 EndY=75.4095 EndZ=0
    g197: LineSegment StartX=58.0728 StartY=73.3346 StartZ=0 EndX=58.0728 EndY=-40.8935 EndZ=0
    g198: Circle CenterX=302.567 CenterY=-42.9683 CenterZ=0 NormalX=0 NormalY=0 NormalZ=1 AngleXU=0 Radius=1
    g199: Circle CenterX=306.073 CenterY=-44.8935 CenterZ=0 NormalX=0 NormalY=0 NormalZ=1 AngleXU=0 Radius=1
    g200: Circle CenterX=306.073 CenterY=-40.8935 CenterZ=0 NormalX=0 NormalY=0 NormalZ=1 AngleXU=0 Radius=1
    g201: BSplineCurve PolesCount=3 KnotsCount=2 Degree=2 IsPeriodic=0
    g202: GeomPoint X=302.567 Y=-42.9683 Z=0
    g203: GeomPoint X=306.073 Y=-40.8935 Z=0
    g204: Circle CenterX=306.073 CenterY=73.3346 CenterZ=0 NormalX=0 NormalY=0 NormalZ=1 AngleXU=0 Radius=1
    g205: Circle CenterX=306.073 CenterY=77.3346 CenterZ=0 NormalX=0 NormalY=0 NormalZ=1 AngleXU=0 Radius=1
    g206: Circle CenterX=302.535 CenterY=75.4095 CenterZ=0 NormalX=0 NormalY=0 NormalZ=1 AngleXU=0 Radius=1
    g207: BSplineCurve PolesCount=3 KnotsCount=2 Degree=2 IsPeriodic=0
    g208: GeomPoint X=306.073 Y=73.3346 Z=0
    g209: GeomPoint X=302.535 Y=75.4095 Z=0
    g210: LineSegment StartX=302.567 StartY=-42.9683 StartZ=0 EndX=198.264 EndY=14.2963 EndZ=0
    g211: LineSegment StartX=198.275 StartY=18.1318 StartZ=0 EndX=302.535 EndY=75.4095 EndZ=0
    g212: LineSegment StartX=306.073 StartY=73.3346 StartZ=0 EndX=306.073 EndY=-40.8935 EndZ=0
    g213: LineSegment StartX=322.073 StartY=105.865 StartZ=0 EndX=328.643 EndY=105.865 EndZ=0
    g214: LineSegment StartX=318.073 StartY=120.221 StartZ=0 EndX=318.073 EndY=109.865 EndZ=0
    g215: LineSegment StartX=336.157 StartY=107.779 StartZ=0 EndX=362.567 EndY=122.294 EndZ=0
    g216: Circle CenterX=362.073 CenterY=124.221 CenterZ=0 NormalX=0 NormalY=0 NormalZ=1 AngleXU=0 Radius=1
    g217: Circle CenterX=366.073 CenterY=124.221 CenterZ=0 NormalX=0 NormalY=0 NormalZ=1 AngleXU=0 Radius=1
    g218: Circle CenterX=362.567 CenterY=122.294 CenterZ=0 NormalX=0 NormalY=0 NormalZ=1 AngleXU=0 Radius=1
    g219: BSplineCurve PolesCount=3 KnotsCount=2 Degree=2 IsPeriodic=0
    g220: GeomPoint X=362.073 Y=124.221 Z=0
    g221: GeomPoint X=362.567 Y=122.294 Z=0
    g222: Circle CenterX=322.073 CenterY=124.221 CenterZ=0 NormalX=0 NormalY=0 NormalZ=1 AngleXU=0 Radius=1
    g223: Circle CenterX=318.073 CenterY=124.221 CenterZ=0 NormalX=0 NormalY=0 NormalZ=1 AngleXU=0 Radius=1
    g224: Circle CenterX=318.073 CenterY=120.221 CenterZ=0 NormalX=0 NormalY=0 NormalZ=1 AngleXU=0 Radius=1
    g225: BSplineCurve PolesCount=3 KnotsCount=2 Degree=2 IsPeriodic=0
    g226: GeomPoint X=322.073 Y=124.221 Z=0
    g227: GeomPoint X=318.073 Y=120.221 Z=0
    g228: Circle CenterX=322.073 CenterY=105.865 CenterZ=0 NormalX=0 NormalY=0 NormalZ=1 AngleXU=0 Radius=1
    g229: Circle CenterX=318.073 CenterY=105.865 CenterZ=0 NormalX=0 NormalY=0 NormalZ=1 AngleXU=0 Radius=1
    g230: Circle CenterX=318.073 CenterY=109.865 CenterZ=0 NormalX=0 NormalY=0 NormalZ=1 AngleXU=0 Radius=1
    g231: BSplineCurve PolesCount=3 KnotsCount=2 Degree=2 IsPeriodic=0
    g232: GeomPoint X=322.073 Y=105.865 Z=0
    g233: GeomPoint X=318.073 Y=109.865 Z=0
    g234: Circle CenterX=336.157 CenterY=107.779 CenterZ=0 NormalX=0 NormalY=0 NormalZ=1 AngleXU=0 Radius=1
    g235: Circle CenterX=332.651 CenterY=105.853 CenterZ=0 NormalX=0 NormalY=0 NormalZ=1 AngleXU=0 Radius=1
    g236: Circle CenterX=328.643 CenterY=105.865 CenterZ=0 NormalX=0 NormalY=0 NormalZ=1 AngleXU=0 Radius=1
    g237: BSplineCurve PolesCount=3 KnotsCount=2 Degree=2 IsPeriodic=0
    g238: GeomPoint X=336.157 Y=107.779 Z=0
    g239: GeomPoint X=328.643 Y=105.865 Z=0
    g240: LineSegment StartX=322.073 StartY=124.221 StartZ=0 EndX=362.073 EndY=124.221 EndZ=0
    g241: Circle CenterX=371.567 CenterY=-80.8644 CenterZ=0 NormalX=0 NormalY=0 NormalZ=1 AngleXU=0 Radius=1
    g242: Circle CenterX=375.073 CenterY=-82.7896 CenterZ=0 NormalX=0 NormalY=0 NormalZ=1 AngleXU=0 Radius=1
    g243: Circle CenterX=375.073 CenterY=-78.7896 CenterZ=0 NormalX=0 NormalY=0 NormalZ=1 AngleXU=0 Radius=1
    g244: BSplineCurve PolesCount=3 KnotsCount=2 Degree=2 IsPeriodic=0
    g245: GeomPoint X=371.567 Y=-80.8644 Z=0
    g246: GeomPoint X=375.073 Y=-78.7896 Z=0
    g247: Circle CenterX=321.579 CenterY=-53.4075 CenterZ=0 NormalX=0 NormalY=0 NormalZ=1 AngleXU=0 Radius=1
    g248: Circle CenterX=318.073 CenterY=-51.4823 CenterZ=0 NormalX=0 NormalY=0 NormalZ=1 AngleXU=0 Radius=1
    g249: Circle CenterX=318.073 CenterY=-47.4805 CenterZ=0 NormalX=0 NormalY=0 NormalZ=1 AngleXU=0 Radius=1
    g250: BSplineCurve PolesCount=3 KnotsCount=2 Degree=2 IsPeriodic=0
    g251: GeomPoint X=321.579 Y=-53.4075 Z=0
    g252: GeomPoint X=318.073 Y=-47.4805 Z=0
    g253: LineSegment StartX=371.567 StartY=-80.8644 StartZ=0 EndX=321.579 EndY=-53.4075 EndZ=0
    g254: Circle CenterX=321.579 CenterY=-67.3492 CenterZ=0 NormalX=0 NormalY=0 NormalZ=1 AngleXU=0 Radius=1
    g255: Circle CenterX=318.073 CenterY=-65.424 CenterZ=0 NormalX=0 NormalY=0 NormalZ=1 AngleXU=0 Radius=1
    g256: Circle CenterX=318.073 CenterY=-69.424 CenterZ=0 NormalX=0 NormalY=0 NormalZ=1 AngleXU=0 Radius=1
    g257: BSplineCurve PolesCount=3 KnotsCount=2 Degree=2 IsPeriodic=0
    g258: GeomPoint X=321.579 Y=-67.3492 Z=0
    g259: GeomPoint X=318.073 Y=-69.424 Z=0
    g260: Circle CenterX=362.567 CenterY=-89.8542 CenterZ=0 NormalX=0 NormalY=0 NormalZ=1 AngleXU=0 Radius=1
    g261: Circle CenterX=366.073 CenterY=-91.7794 CenterZ=0 NormalX=0 NormalY=0 NormalZ=1 AngleXU=0 Radius=1
    g262: Circle CenterX=362.073 CenterY=-91.7794 CenterZ=0 NormalX=0 NormalY=0 NormalZ=1 AngleXU=0 Radius=1
    g263: BSplineCurve PolesCount=3 KnotsCount=2 Degree=2 IsPeriodic=0
    g264: GeomPoint X=362.567 Y=-89.8542 Z=0
    g265: GeomPoint X=362.073 Y=-91.7794 Z=0
    g266: Circle CenterX=322.073 CenterY=-91.7794 CenterZ=0 NormalX=0 NormalY=0 NormalZ=1 AngleXU=0 Radius=1
    g267: Circle CenterX=318.073 CenterY=-91.7794 CenterZ=0 NormalX=0 NormalY=0 NormalZ=1 AngleXU=0 Radius=1
    g268: Circle CenterX=318.073 CenterY=-87.7794 CenterZ=0 NormalX=0 NormalY=0 NormalZ=1 AngleXU=0 Radius=1
    g269: BSplineCurve PolesCount=3 KnotsCount=2 Degree=2 IsPeriodic=0
    g270: GeomPoint X=322.073 Y=-91.7794 Z=0
    g271: GeomPoint X=318.073 Y=-87.7794 Z=0
    g272: LineSegment StartX=362.567 StartY=-89.8542 StartZ=0 EndX=321.579 EndY=-67.3492 EndZ=0
    g273: LineSegment StartX=318.073 StartY=-69.424 StartZ=0 EndX=318.073 EndY=-87.7794 EndZ=0
    g274: LineSegment StartX=322.073 StartY=-91.7794 StartZ=0 EndX=362.073 EndY=-91.7794 EndZ=0
    g275: Circle CenterX=2.07281 CenterY=124.221 CenterZ=0 NormalX=0 NormalY=0 NormalZ=1 AngleXU=0 Radius=1
    g276: Circle CenterX=1.57905 CenterY=122.295 CenterZ=0 NormalX=0 NormalY=0 NormalZ=1 AngleXU=0 Radius=1
    g277: BSplineCurve PolesCount=3 KnotsCount=2 Degree=2 IsPeriodic=0
    g278: GeomPoint X=2.07281 Y=124.221 Z=0
    g279: GeomPoint X=1.57905 Y=122.295 Z=0
    g280: Circle CenterX=42.0728 CenterY=124.221 CenterZ=0 NormalX=0 NormalY=0 NormalZ=1 AngleXU=0 Radius=1
    g281: Circle CenterX=46.0728 CenterY=124.221 CenterZ=0 NormalX=0 NormalY=0 NormalZ=1 AngleXU=0 Radius=1
    g282: Circle CenterX=46.0728 CenterY=120.221 CenterZ=0 NormalX=0 NormalY=0 NormalZ=1 AngleXU=0 Radius=1
    g283: BSplineCurve PolesCount=3 KnotsCount=2 Degree=2 IsPeriodic=0
    g284: GeomPoint X=42.0728 Y=124.221 Z=0
    g285: GeomPoint X=46.0728 Y=120.221 Z=0
    g286: Circle CenterX=46.0728 CenterY=109.865 CenterZ=0 NormalX=0 NormalY=0 NormalZ=1 AngleXU=0 Radius=1
    g287: Circle CenterX=46.0728 CenterY=105.865 CenterZ=0 NormalX=0 NormalY=0 NormalZ=1 AngleXU=0 Radius=1
    g288: Circle CenterX=42.0728 CenterY=105.865 CenterZ=0 NormalX=0 NormalY=0 NormalZ=1 AngleXU=0 Radius=1
    g289: BSplineCurve PolesCount=3 KnotsCount=2 Degree=2 IsPeriodic=0
    g290: GeomPoint X=46.0728 Y=109.865 Z=0
    g291: GeomPoint X=42.0728 Y=105.865 Z=0
    g292: Circle CenterX=35.5028 CenterY=105.865 CenterZ=0 NormalX=0 NormalY=0 NormalZ=1 AngleXU=0 Radius=1
    g293: Circle CenterX=31.5028 CenterY=105.865 CenterZ=0 NormalX=0 NormalY=0 NormalZ=1 AngleXU=0 Radius=1
    g294: Circle CenterX=27.9965 CenterY=107.79 CenterZ=0 NormalX=0 NormalY=0 NormalZ=1 AngleXU=0 Radius=1
    g295: BSplineCurve PolesCount=3 KnotsCount=2 Degree=2 IsPeriodic=0
    g296: GeomPoint X=35.5028 Y=105.865 Z=0
    g297: GeomPoint X=27.9965 Y=107.79 Z=0
    g298: LineSegment StartX=2.07281 StartY=124.221 StartZ=0 EndX=42.0728 EndY=124.221 EndZ=0
    g299: LineSegment StartX=46.0728 StartY=120.221 StartZ=0 EndX=46.0728 EndY=109.865 EndZ=0
    g300: LineSegment StartX=42.0728 StartY=105.865 StartZ=0 EndX=35.5028 EndY=105.865 EndZ=0
    g301: LineSegment StartX=27.9965 StartY=107.79 StartZ=0 EndX=1.57905 EndY=122.295 EndZ=0
    g302: Circle CenterX=42.5666 CenterY=-67.3492 CenterZ=0 NormalX=0 NormalY=0 NormalZ=1 AngleXU=0 Radius=1
    g303: Circle CenterX=46.0728 CenterY=-65.424 CenterZ=0 NormalX=0 NormalY=0 NormalZ=1 AngleXU=0 Radius=1
    g304: Circle CenterX=46.0728 CenterY=-69.424 CenterZ=0 NormalX=0 NormalY=0 NormalZ=1 AngleXU=0 Radius=1
    g305: BSplineCurve PolesCount=3 KnotsCount=2 Degree=2 IsPeriodic=0
    g306: GeomPoint X=42.5666 Y=-67.3492 Z=0
    g307: GeomPoint X=46.0728 Y=-69.424 Z=0
    g308: Circle CenterX=46.0728 CenterY=-87.7794 CenterZ=0 NormalX=0 NormalY=0 NormalZ=1 AngleXU=0 Radius=1
    g309: Circle CenterX=46.0728 CenterY=-91.7794 CenterZ=0 NormalX=0 NormalY=0 NormalZ=1 AngleXU=0 Radius=1
    g310: Circle CenterX=42.0728 CenterY=-91.7794 CenterZ=0 NormalX=0 NormalY=0 NormalZ=1 AngleXU=0 Radius=1
    g311: BSplineCurve PolesCount=3 KnotsCount=2 Degree=2 IsPeriodic=0
    g312: GeomPoint X=46.0728 Y=-87.7794 Z=0
    g313: GeomPoint X=42.0728 Y=-91.7794 Z=0
    g314: Circle CenterX=2.07281 CenterY=-91.7794 CenterZ=0 NormalX=0 NormalY=0 NormalZ=1 AngleXU=0 Radius=1
    g315: Circle CenterX=-1.92719 CenterY=-91.7794 CenterZ=0 NormalX=0 NormalY=0 NormalZ=1 AngleXU=0 Radius=1
    g316: Circle CenterX=1.57905 CenterY=-89.8542 CenterZ=0 NormalX=0 NormalY=0 NormalZ=1 AngleXU=0 Radius=1
    g317: BSplineCurve PolesCount=3 KnotsCount=2 Degree=2 IsPeriodic=0
    g318: GeomPoint X=2.07281 Y=-91.7794 Z=0
    g319: GeomPoint X=1.57905 Y=-89.8542 Z=0
    g320: LineSegment StartX=2.07281 StartY=-91.7794 StartZ=0 EndX=42.0728 EndY=-91.7794 EndZ=0
    g321: LineSegment StartX=46.0728 StartY=-87.7794 StartZ=0 EndX=46.0728 EndY=-69.424 EndZ=0
    g322: LineSegment StartX=42.5666 StartY=-67.3492 StartZ=0 EndX=1.57905 EndY=-89.8542 EndZ=0
    g323: Circle CenterX=322.073 CenterY=76.4095 CenterZ=0 NormalX=0 NormalY=0 NormalZ=1 AngleXU=0 Radius=4
    g324: BSplineCurve PolesCount=3 KnotsCount=2 Degree=2 IsPeriodic=0
    g325: GeomPoint X=318.073 Y=72.4095 Z=0
    g326: GeomPoint X=322.073 Y=76.4095 Z=0
    g327: Circle CenterX=375.073 CenterY=72.4095 CenterZ=0 NormalX=0 NormalY=0 NormalZ=1 AngleXU=0 Radius=1
    g328: Circle CenterX=375.073 CenterY=76.4095 CenterZ=0 NormalX=0 NormalY=0 NormalZ=1 AngleXU=0 Radius=1
    g329: Circle CenterX=371.073 CenterY=76.4095 CenterZ=0 NormalX=0 NormalY=0 NormalZ=1 AngleXU=0 Radius=1
    g330: BSplineCurve PolesCount=3 KnotsCount=2 Degree=2 IsPeriodic=0
    g331: GeomPoint X=375.073 Y=72.4095 Z=0
    g332: GeomPoint X=371.073 Y=76.4095 Z=0
    g333: LineSegment StartX=322.073 StartY=76.4095 StartZ=0 EndX=371.073 EndY=76.4095 EndZ=0
    g334: LineSegment StartX=318.073 StartY=72.4095 StartZ=0 EndX=318.073 EndY=-47.4805 EndZ=0
    g335: LineSegment StartX=375.073 StartY=72.4095 StartZ=0 EndX=375.073 EndY=-78.7896 EndZ=0
    g336: ArcOfCircle CenterX=-26.9272 CenterY=22.1087 CenterZ=0 NormalX=0 NormalY=0 NormalZ=1 AngleXU=0 Radius=4 StartAngle=5e-16 EndAngle=3.14159
    g337: LineSegment StartX=-22.9272 StartY=22.1087 StartZ=0 EndX=-18.9272 EndY=-83.7794 EndZ=0
    g338: LineSegment StartX=-34.9272 StartY=-83.7794 StartZ=0 EndX=-30.9272 EndY=22.1087 EndZ=0
    g339: ArcOfCircle CenterX=391.073 CenterY=22.1087 CenterZ=0 NormalX=0 NormalY=0 NormalZ=1 AngleXU=0 Radius=4 StartAngle=0 EndAngle=3.14159
    g340: LineSegment StartX=387.073 StartY=22.1087 StartZ=0 EndX=383.073 EndY=-83.7794 EndZ=0
    g341: LineSegment StartX=395.073 StartY=22.1087 StartZ=0 EndX=399.073 EndY=-83.7794 EndZ=0
    g342: Circle CenterX=-10.9272 CenterY=-78.7794 CenterZ=0 NormalX=0 NormalY=0 NormalZ=1 AngleXU=0 Radius=1
    g343: Circle CenterX=-10.9272 CenterY=-82.7794 CenterZ=0 NormalX=0 NormalY=0 NormalZ=1 AngleXU=0 Radius=1
    g344: Circle CenterX=-7.42095 CenterY=-80.8542 CenterZ=0 NormalX=0 NormalY=0 NormalZ=1 AngleXU=0 Radius=1
    g345: BSplineCurve PolesCount=3 KnotsCount=2 Degree=2 IsPeriodic=0
    g346: GeomPoint X=-10.9272 Y=-78.7794 Z=0
    g347: GeomPoint X=-7.42095 Y=-80.8542 Z=0
    g348: Circle CenterX=42.5666 CenterY=-53.4075 CenterZ=0 NormalX=0 NormalY=0 NormalZ=1 AngleXU=0 Radius=1
    g349: Circle CenterX=46.0728 CenterY=-51.4823 CenterZ=0 NormalX=0 NormalY=0 NormalZ=1 AngleXU=0 Radius=1
    g350: Circle CenterX=46.0728 CenterY=-47.4823 CenterZ=0 NormalX=0 NormalY=0 NormalZ=1 AngleXU=0 Radius=1
    g351: BSplineCurve PolesCount=3 KnotsCount=2 Degree=2 IsPeriodic=0
    g352: GeomPoint X=42.5666 Y=-53.4075 Z=0
    g353: GeomPoint X=46.0728 Y=-47.4823 Z=0
    g354: Circle CenterX=46.0728 CenterY=72.4095 CenterZ=0 NormalX=0 NormalY=0 NormalZ=1 AngleXU=0 Radius=1
    g355: Circle CenterX=46.0728 CenterY=76.4095 CenterZ=0 NormalX=0 NormalY=0 NormalZ=1 AngleXU=0 Radius=1
    g356: Circle CenterX=42.0728 CenterY=76.4095 CenterZ=0 NormalX=0 NormalY=0 NormalZ=1 AngleXU=0 Radius=1
    g357: BSplineCurve PolesCount=3 KnotsCount=2 Degree=2 IsPeriodic=0
    g358: GeomPoint X=46.0728 Y=72.4095 Z=0
    g359: GeomPoint X=42.0728 Y=76.4095 Z=0
    g360: Circle CenterX=-6.92719 CenterY=76.4095 CenterZ=0 NormalX=0 NormalY=0 NormalZ=1 AngleXU=0 Radius=1
    g361: Circle CenterX=-10.9272 CenterY=76.4095 CenterZ=0 NormalX=0 NormalY=0 NormalZ=1 AngleXU=0 Radius=1
    g362: Circle CenterX=-10.9272 CenterY=72.4095 CenterZ=0 NormalX=0 NormalY=0 NormalZ=1 AngleXU=0 Radius=1
    g363: BSplineCurve PolesCount=3 KnotsCount=2 Degree=2 IsPeriodic=0
    g364: GeomPoint X=-6.92719 Y=76.4095 Z=0
    g365: GeomPoint X=-10.9272 Y=72.4095 Z=0
    g366: LineSegment StartX=-10.9272 StartY=72.4095 StartZ=0 EndX=-10.9272 EndY=-78.7794 EndZ=0
    g367: LineSegment StartX=-7.42095 StartY=-80.8542 StartZ=0 EndX=42.5666 EndY=-53.4075 EndZ=0
    g368: LineSegment StartX=46.0728 StartY=-47.4823 StartZ=0 EndX=46.0728 EndY=72.4095 EndZ=0
    g369: LineSegment StartX=42.0728 StartY=76.4095 StartZ=0 EndX=-6.92719 EndY=76.4095 EndZ=0
    g370: LineSegment StartX=-42.9272 StartY=136.221 StartZ=0 EndX=407.073 EndY=136.221 EndZ=0
    g371: LineSegment StartX=232.072 StartY=136.221 StartZ=0 EndX=220.072 EndY=136.221 EndZ=0
    g372: LineSegment StartX=232.072 StartY=136.221 StartZ=0 EndX=232.072 EndY=124.221 EndZ=0
    g373: LineSegment StartX=220.072 StartY=136.221 StartZ=0 EndX=220.072 EndY=124.221 EndZ=0
    g374: LineSegment StartX=220.072 StartY=136.221 StartZ=0 EndX=226.072 EndY=136.221 EndZ=0
    g375: LineSegment StartX=220.072 StartY=136.221 StartZ=0 EndX=220.072 EndY=130.221 EndZ=0
    g376: LineSegment StartX=220.072 StartY=124.221 StartZ=0 EndX=226.072 EndY=124.221 EndZ=0
    g377: LineSegment StartX=232.072 StartY=124.221 StartZ=0 EndX=232.072 EndY=127.221 EndZ=0
    g378: LineSegment StartX=232.072 StartY=136.221 StartZ=0 EndX=232.072 EndY=133.221 EndZ=0
    g379-g383: Circle x5 (B-spline internal-alignment scaffolding for g384; pole/knot coordinates omitted)
    g384: BSplineCurve PolesCount=5 KnotsCount=3 Degree=3 IsPeriodic=0
    g385: GeomPoint X=232.072 Y=133.221 Z=0
    g386: GeomPoint X=223.072 Y=130.221 Z=0
    g387: GeomPoint X=232.072 Y=127.221 Z=0
    g388: LineSegment StartX=189.124 StartY=124.221 StartZ=0 EndX=302.073 EndY=124.221 EndZ=0
    g389: LineSegment StartX=132.072 StartY=136.221 StartZ=0 EndX=132.072 EndY=124.221 EndZ=0
    g390: LineSegment StartX=132.072 StartY=136.221 StartZ=0 EndX=144.072 EndY=136.221 EndZ=0
    g391: LineSegment StartX=144.072 StartY=136.221 StartZ=0 EndX=144.072 EndY=124.221 EndZ=0
    g392: LineSegment StartX=144.072 StartY=136.221 StartZ=0 EndX=138.072 EndY=136.221 EndZ=0
    g393: LineSegment StartX=144.072 StartY=136.221 StartZ=0 EndX=144.072 EndY=130.221 EndZ=0
    g394: LineSegment StartX=132.072 StartY=136.221 StartZ=0 EndX=132.072 EndY=133.221 EndZ=0
    g395: LineSegment StartX=132.072 StartY=133.221 StartZ=0 EndX=132.072 EndY=127.221 EndZ=0
    g396-g400: Circle x5 (B-spline internal-alignment scaffolding for g401; pole/knot coordinates omitted)
    g401: BSplineCurve PolesCount=5 KnotsCount=3 Degree=3 IsPeriodic=0
    g402: GeomPoint X=132.072 Y=133.221 Z=0
    g403: GeomPoint X=141.072 Y=130.221 Z=0
    g404: GeomPoint X=132.072 Y=127.221 Z=0
    g405: LineSegment StartX=132.072 StartY=124.221 StartZ=0 EndX=175.022 EndY=124.221 EndZ=0
    g406: LineSegment StartX=62.0728 StartY=124.221 StartZ=0 EndX=132.072 EndY=124.221 EndZ=0
    g407: LineSegment StartX=132.072 StartY=136.221 StartZ=0 EndX=131.457 EndY=138.832 EndZ=0
    ... +61 more geometry lines
  constraints (808):
    c: Vertical(g0)
    c: Vertical(g1)
    c: Block(g1)
    c: Block(g0)
    c: Weight(g4) = 1
    c: Equal(g4,g5)
    c: Equal(g4,g6)
    c: InternalAlignment(g4,g7)
    c: InternalAlignment(g5,g7)
    c: InternalAlignment(g6,g7)
    c: InternalAlignment(g8,g7)
    c: InternalAlignment(g9,g7)
    c: Weight(g10) = 1
    c: Equal(g10,g11)
    c: Equal(g10,g12)
    c: InternalAlignment(g10,g13)
    c: InternalAlignment(g11,g13)
    c: InternalAlignment(g12,g13)
    c: InternalAlignment(g14,g13)
    c: InternalAlignment(g15,g13)
    c: Block(g13)
    c: Block(g7)
    c: Weight(g16) = 1
    c: Equal(g16,g17)
    c: Equal(g16,g18)
    c: InternalAlignment(g16,g19)
    c: InternalAlignment(g17,g19)
    c: InternalAlignment(g18,g19)
    c: InternalAlignment(g20,g19)
    c: InternalAlignment(g21,g19)
    c: Weight(g22) = 1
    c: Equal(g22,g23)
    c: Equal(g22,g24)
    c: InternalAlignment(g22,g25)
    c: InternalAlignment(g23,g25)
    c: InternalAlignment(g24,g25)
    c: InternalAlignment(g26,g25)
    c: InternalAlignment(g27,g25)
    c: Block(g25)
    c: Block(g19)
    c: Weight(g28) = 1
    c: Equal(g28,g29)
    c: Equal(g28,g30)
    c: InternalAlignment(g28,g31)
    c: InternalAlignment(g29,g31)
    c: InternalAlignment(g30,g31)
    c: InternalAlignment(g32,g31)
    c: InternalAlignment(g33,g31)
    c: Weight(g34) = 1
    c: Equal(g34,g35)
    c: Equal(g34,g36)
    c: InternalAlignment(g34,g37)
    c: InternalAlignment(g35,g37)
    c: InternalAlignment(g36,g37)
    c: InternalAlignment(g38,g37)
    c: InternalAlignment(g39,g37)
    c: Block(g31)
    c: Block(g37)
    c: Coincident(g40,g1)
    c: Coincident(g40,g0)
    c: Horizontal(g40)
    c: Distance(g40) = 450
    c: Weight(g41) = 1
    c: Equal(g41,g42)
    c: Equal(g41,g43)
    c: InternalAlignment(g41,g44)
    c: InternalAlignment(g42,g44)
    c: InternalAlignment(g43,g44)
    c: InternalAlignment(g45,g44)
    c: InternalAlignment(g46,g44)
    c: Block(g44)
    c: Weight(g47) = 1
    c: Equal(g47,g48)
    c: Equal(g47,g49)
    c: InternalAlignment(g47,g50)
    c: InternalAlignment(g48,g50)
    c: InternalAlignment(g49,g50)
    c: InternalAlignment(g51,g50)
    c: InternalAlignment(g52,g50)
    c: Block(g50)
    c: Weight(g53) = 1
    c: Equal(g53,g54)
    c: Equal(g53,g55)
    c: InternalAlignment(g53,g56)
    c: InternalAlignment(g54,g56)
    c: InternalAlignment(g55,g56)
    c: InternalAlignment(g57,g56)
    c: InternalAlignment(g58,g56)
    c: Block(g56)
    c: Weight(g59) = 1
    c: Equal(g59,g60)
    c: Equal(g59,g61)
    c: InternalAlignment(g59,g62)
    c: InternalAlignment(g60,g62)
    c: InternalAlignment(g61,g62)
    c: InternalAlignment(g63,g62)
    c: InternalAlignment(g64,g62)
    c: Block(g62)
    c: Weight(g65) = 1
    c: Equal(g65,g66)
    c: Equal(g65,g67)
    c: InternalAlignment(g65,g68)
    c: InternalAlignment(g66,g68)
    c: InternalAlignment(g67,g68)
    c: InternalAlignment(g69,g68)
    c: InternalAlignment(g70,g68)
    c: Weight(g71) = 1
    c: Equal(g71,g72)
    c: Equal(g71,g73)
    c: InternalAlignment(g71,g74)
    c: InternalAlignment(g72,g74)
    c: InternalAlignment(g73,g74)
    c: InternalAlignment(g75,g74)
    c: InternalAlignment(g76,g74)
    c: Block(g68)
    c: Block(g74)
    c: Coincident(g77,g68)
    c: Coincident(g77,g74)
    c: Vertical(g77)
    c: Coincident(g78,g68)
    c: Coincident(g78,g50)
    c: Coincident(g79,g50)
    c: Coincident(g79,g74)
    c: Weight(g80) = 1
    c: Equal(g80,g81)
    c: Equal(g80,g82)
    c: InternalAlignment(g80,g83)
    c: InternalAlignment(g81,g83)
    c: InternalAlignment(g82,g83)
    c: InternalAlignment(g84,g83)
    c: InternalAlignment(g85,g83)
    c: Weight(g86) = 1
    c: Equal(g86,g87)
    c: Equal(g86,g88)
    c: InternalAlignment(g86,g89)
    c: InternalAlignment(g87,g89)
    c: InternalAlignment(g88,g89)
    c: InternalAlignment(g90,g89)
    c: InternalAlignment(g91,g89)
    c: Block(g83)
    c: Block(g89)
    c: Coincident(g92,g83)
    c: Coincident(g92,g89)
    c: Vertical(g92)
    c: Coincident(g93,g83)
    c: Coincident(g93,g44)
    c: Coincident(g94,g44)
    c: Coincident(g94,g89)
    c: Weight(g95) = 1
    c: Equal(g95,g96)
    c: Equal(g95,g97)
    c: InternalAlignment(g95,g98)
    c: InternalAlignment(g96,g98)
    c: InternalAlignment(g97,g98)
    c: InternalAlignment(g99,g98)
    c: InternalAlignment(g100,g98)
    c: Weight(g101) = 1
    c: Equal(g101,g102)
    c: Equal(g101,g103)
    c: InternalAlignment(g101,g104)
    c: InternalAlignment(g102,g104)
    c: InternalAlignment(g103,g104)
    c: InternalAlignment(g105,g104)
    c: InternalAlignment(g106,g104)
    c: Block(g98)
    c: Block(g104)
    c: Coincident(g107,g98)
    c: Coincident(g107,g104)
    c: Vertical(g107)
    c: Coincident(g108,g104)
    c: Coincident(g108,g62)
    c: Coincident(g109,g62)
    c: Coincident(g109,g98)
    c: Weight(g110) = 1
    c: Equal(g110,g111)
    c: Equal(g110,g112)
    c: InternalAlignment(g110,g113)
    c: InternalAlignment(g111,g113)
    c: InternalAlignment(g112,g113)
    c: InternalAlignment(g114,g113)
    c: InternalAlignment(g115,g113)
    c: Weight(g116) = 1
    c: Equal(g116,g117)
    c: Equal(g116,g118)
    c: InternalAlignment(g116,g119)
    c: InternalAlignment(g117,g119)
    c: InternalAlignment(g118,g119)
    c: InternalAlignment(g120,g119)
    c: InternalAlignment(g121,g119)
    c: Block(g113)
    c: Block(g119)
    c: Coincident(g122,g113)
    c: Coincident(g122,g119)
    c: Vertical(g122)
    c: Coincident(g123,g119)
    c: Coincident(g123,g56)
    c: Coincident(g124,g56)
    c: Coincident(g124,g113)
    c: Weight(g125) = 1
    c: Equal(g125,g126)
    c: Equal(g125,g127)
    c: InternalAlignment(g125,g128)
    c: InternalAlignment(g126,g128)
    c: InternalAlignment(g127,g128)
    c: InternalAlignment(g129,g128)
    c: InternalAlignment(g130,g128)
    c: Weight(g131) = 1
    c: Equal(g131,g132)
    c: Equal(g131,g133)
    c: InternalAlignment(g131,g134)
    c: InternalAlignment(g132,g134)
    c: InternalAlignment(g133,g134)
    c: InternalAlignment(g135,g134)
    c: InternalAlignment(g136,g134)
    c: Weight(g137) = 1
    c: Equal(g137,g138)
    c: Equal(g137,g139)
    c: InternalAlignment(g137,g140)
    c: InternalAlignment(g138,g140)
    c: InternalAlignment(g139,g140)
    c: InternalAlignment(g141,g140)
    c: InternalAlignment(g142,g140)
    c: Weight(g143) = 1
    c: Equal(g143,g144)
    c: Equal(g143,g145)
    c: InternalAlignment(g143,g146)
    c: InternalAlignment(g144,g146)
    c: InternalAlignment(g145,g146)
    c: InternalAlignment(g147,g146)
    c: InternalAlignment(g148,g146)
    c: Block(g146)
    c: Block(g140)
    c: Block(g134)
    c: Block(g128)
    c: Coincident(g149,g25)
    c: Coincident(g149,g146)
    c: Coincident(g150,g146)
    c: Coincident(g150,g140)
    c: Horizontal(g150)
    c: Coincident(g151,g140)
    c: Coincident(g151,g25)
    c: Vertical(g151)
    c: Coincident(g152,g19)
    c: Coincident(g152,g134)
    c: Vertical(g152)
    c: Coincident(g153,g134)
    c: Coincident(g153,g128)
    c: Horizontal(g153)
    c: Coincident(g154,g128)
    c: Coincident(g154,g19)
    c: Weight(g155) = 1
    c: Equal(g155,g156)
    c: Equal(g155,g157)
    c: InternalAlignment(g155,g158)
    c: InternalAlignment(g156,g158)
    c: InternalAlignment(g157,g158)
    c: InternalAlignment(g159,g158)
    c: InternalAlignment(g160,g158)
    c: Weight(g161) = 1
    c: Equal(g161,g162)
    c: Equal(g161,g163)
    c: InternalAlignment(g161,g164)
    c: InternalAlignment(g162,g164)
    c: InternalAlignment(g163,g164)
    c: InternalAlignment(g165,g164)
    c: InternalAlignment(g166,g164)
    c: Weight(g167) = 1
    c: Equal(g167,g168)
    c: Equal(g167,g169)
    c: InternalAlignment(g167,g170)
    c: InternalAlignment(g168,g170)
    c: InternalAlignment(g169,g170)
    c: InternalAlignment(g171,g170)
    c: InternalAlignment(g172,g170)
    c: Weight(g173) = 1
    c: Equal(g173,g174)
    c: Equal(g173,g175)
    c: InternalAlignment(g173,g176)
    c: InternalAlignment(g174,g176)
    c: InternalAlignment(g175,g176)
    c: InternalAlignment(g177,g176)
    c: InternalAlignment(g178,g176)
    c: Block(g176)
    c: Block(g170)
    c: Block(g164)
    c: Block(g158)
    c: Coincident(g179,g170)
    c: Coincident(g179,g7)
    c: Vertical(g179)
    c: Coincident(g180,g13)
    c: Coincident(g180,g164)
    c: Vertical(g180)
    c: Coincident(g181,g158)
    c: Coincident(g181,g13)
    c: Coincident(g182,g7)
    c: Weight(g183) = 1
    c: Equal(g183,g184)
    c: Equal(g183,g185)
    c: InternalAlignment(g183,g186)
    c: InternalAlignment(g184,g186)
    c: InternalAlignment(g185,g186)
    c: InternalAlignment(g187,g186)
    c: InternalAlignment(g188,g186)
    c: Weight(g189) = 1
    c: Equal(g189,g190)
    c: Equal(g189,g191)
    c: InternalAlignment(g189,g192)
    c: InternalAlignment(g190,g192)
    c: InternalAlignment(g191,g192)
    c: InternalAlignment(g193,g192)
    c: InternalAlignment(g194,g192)
    c: Block(g192)
    c: Block(g186)
    c: Coincident(g195,g192)
    c: Coincident(g195,g31)
    c: Coincident(g196,g31)
    c: Coincident(g196,g186)
    c: Coincident(g197,g186)
    c: Coincident(g197,g192)
    c: Vertical(g197)
    c: Weight(g198) = 1
    c: Equal(g198,g199)
    c: Equal(g198,g200)
    c: InternalAlignment(g198,g201)
    c: InternalAlignment(g199,g201)
    c: InternalAlignment(g200,g201)
    c: InternalAlignment(g202,g201)
    c: InternalAlignment(g203,g201)
    c: Weight(g204) = 1
    c: Equal(g204,g205)
    c: Equal(g204,g206)
    c: InternalAlignment(g204,g207)
    c: InternalAlignment(g205,g207)
    c: InternalAlignment(g206,g207)
    c: InternalAlignment(g208,g207)
    c: InternalAlignment(g209,g207)
    c: Block(g207)
    c: Block(g201)
    c: Coincident(g210,g201)
    c: Coincident(g210,g37)
    c: Coincident(g211,g37)
    c: Coincident(g211,g207)
    c: Coincident(g212,g207)
    c: Coincident(g212,g201)
    c: Vertical(g212)
    c: Horizontal(g213)
    c: Block(g213)
    c: Vertical(g214)
    c: Block(g214)
    c: Block(g215)
    c: Weight(g216) = 1
    c: Equal(g216,g217)
    c: Equal(g216,g218)
    c: InternalAlignment(g216,g219)
    c: InternalAlignment(g217,g219)
    c: InternalAlignment(g218,g219)
    c: InternalAlignment(g220,g219)
    c: InternalAlignment(g221,g219)
    c: Weight(g222) = 1
    c: Equal(g222,g223)
    c: Equal(g222,g224)
    c: InternalAlignment(g222,g225)
    c: InternalAlignment(g223,g225)
    c: InternalAlignment(g224,g225)
    c: InternalAlignment(g226,g225)
    c: InternalAlignment(g227,g225)
    c: Weight(g228) = 1
    c: Equal(g228,g229)
    c: Equal(g228,g230)
    c: InternalAlignment(g228,g231)
    c: InternalAlignment(g229,g231)
    c: InternalAlignment(g230,g231)
    c: InternalAlignment(g232,g231)
    c: InternalAlignment(g233,g231)
    c: Weight(g234) = 1
    c: Equal(g234,g235)
    c: Equal(g234,g236)
    c: InternalAlignment(g234,g237)
    c: InternalAlignment(g235,g237)
    c: InternalAlignment(g236,g237)
    c: InternalAlignment(g238,g237)
    c: InternalAlignment(g239,g237)
    c: Block(g219)
    c: Block(g225)
    c: Block(g231)
    c: Block(g237)
    c: Coincident(g240,g225)
    c: Coincident(g240,g219)
    c: Horizontal(g240)
    c: Block(g182)
    c: Weight(g241) = 1
    c: Equal(g241,g242)
    c: Equal(g241,g243)
    c: InternalAlignment(g241,g244)
    c: InternalAlignment(g242,g244)
    c: InternalAlignment(g243,g244)
    c: InternalAlignment(g245,g244)
    c: InternalAlignment(g246,g244)
    c: Weight(g247) = 1
    c: Equal(g247,g248)
    c: Equal(g247,g249)
    c: InternalAlignment(g247,g250)
    c: InternalAlignment(g248,g250)
    c: InternalAlignment(g249,g250)
    c: InternalAlignment(g251,g250)
    c: InternalAlignment(g252,g250)
    c: Block(g244)
    c: Block(g250)
    c: Coincident(g253,g244)
    c: Coincident(g253,g250)
    c: Weight(g254) = 1
    c: Equal(g254,g255)
    c: Equal(g254,g256)
    c: InternalAlignment(g254,g257)
    c: InternalAlignment(g255,g257)
    c: InternalAlignment(g256,g257)
    c: InternalAlignment(g258,g257)
    c: InternalAlignment(g259,g257)
    c: Weight(g260) = 1
    c: Equal(g260,g261)
    c: Equal(g260,g262)
    c: InternalAlignment(g260,g263)
    c: InternalAlignment(g261,g263)
    c: InternalAlignment(g262,g263)
    c: InternalAlignment(g264,g263)
    c: InternalAlignment(g265,g263)
    c: Weight(g266) = 1
    c: Equal(g266,g267)
    c: Equal(g266,g268)
    c: InternalAlignment(g266,g269)
    c: InternalAlignment(g267,g269)
    c: InternalAlignment(g268,g269)
    c: InternalAlignment(g270,g269)
    c: InternalAlignment(g271,g269)
    c: Block(g269)
    c: Block(g263)
    c: Block(g257)
    c: Coincident(g272,g263)
    c: Coincident(g272,g257)
    c: Coincident(g273,g257)
    c: Coincident(g273,g269)
    c: Vertical(g273)
    c: Coincident(g274,g269)
    c: Coincident(g274,g263)
    c: Horizontal(g274)
    c: Weight(g275) = 1
    c: Equal(g275,g276)
    c: InternalAlignment(g275,g277)
    c: InternalAlignment(g276,g277)
    c: InternalAlignment(g278,g277)
    c: InternalAlignment(g279,g277)
    c: Weight(g280) = 1
    c: InternalAlignment(g281,g283)
    c: InternalAlignment(g282,g283)
    c: InternalAlignment(g284,g283)
    c: InternalAlignment(g285,g283)
    c: Weight(g286) = 1
    c: Equal(g286,g287)
    c: Equal(g286,g288)
    c: InternalAlignment(g286,g289)
    c: InternalAlignment(g287,g289)
    c: InternalAlignment(g288,g289)
    c: InternalAlignment(g290,g289)
    c: InternalAlignment(g291,g289)
    c: Equal(g292,g293)
    c: Equal(g292,g294)
    c: InternalAlignment(g292,g295)
    c: InternalAlignment(g293,g295)
    c: InternalAlignment(g294,g295)
    c: InternalAlignment(g296,g295)
    c: InternalAlignment(g297,g295)
    c: Block(g283)
    c: Block(g289)
    c: Block(g295)
    c: Block(g277)
    c: Coincident(g298,g277)
    c: Coincident(g298,g283)
    c: Horizontal(g298)
    c: Coincident(g299,g283)
    c: Coincident(g299,g289)
    c: Vertical(g299)
    c: Coincident(g300,g289)
    c: Coincident(g300,g295)
    c: Horizontal(g300)
    c: Coincident(g301,g295)
    c: Coincident(g301,g277)
    c: Weight(g302) = 1
    c: Equal(g302,g303)
    c: Equal(g302,g304)
    c: InternalAlignment(g302,g305)
    c: InternalAlignment(g303,g305)
    c: InternalAlignment(g304,g305)
    c: InternalAlignment(g306,g305)
    c: InternalAlignment(g307,g305)
    c: Weight(g308) = 1
    c: Equal(g308,g309)
    c: Equal(g308,g310)
    c: InternalAlignment(g308,g311)
    c: InternalAlignment(g309,g311)
    c: InternalAlignment(g310,g311)
    c: InternalAlignment(g312,g311)
    c: Weight(g314) = 1
    c: Equal(g314,g315)
    c: Equal(g314,g316)
    c: InternalAlignment(g314,g317)
    c: InternalAlignment(g315,g317)
    c: InternalAlignment(g316,g317)
    c: InternalAlignment(g318,g317)
    c: InternalAlignment(g319,g317)
    c: Block(g317)
    c: Block(g311)
    c: Block(g305)
    c: Coincident(g320,g317)
    c: Coincident(g320,g311)
    c: Horizontal(g320)
    c: Coincident(g321,g311)
    c: Coincident(g321,g305)
    c: Vertical(g321)
    c: Coincident(g322,g305)
    c: Coincident(g322,g317)
    c: InternalAlignment(g323,g324)
    c: InternalAlignment(g325,g324)
    c: InternalAlignment(g326,g324)
    c: Block(g324)
    c: Equal(g327,g328)
    c: Equal(g327,g329)
    c: InternalAlignment(g327,g330)
    c: InternalAlignment(g328,g330)
    c: InternalAlignment(g329,g330)
    c: InternalAlignment(g331,g330)
    c: InternalAlignment(g332,g330)
    c: Block(g330)
    c: Coincident(g333,g324)
    c: Horizontal(g333)
    c: Block(g333)
    c: Coincident(g334,g324)
    c: Coincident(g334,g250)
    c: Vertical(g334)
    c: Coincident(g335,g330)
    c: Coincident(g335,g244)
    c: Vertical(g335)
    c: Block(g336)
    c: Block(g2)
    c: Distance(g334) = 119.89
    c: Coincident(g337,g336)
    c: Coincident(g337,g2)
    c: Coincident(g338,g2)
    c: Coincident(g338,g336)
    c: Block(g3)
    c: Block(g339)
    c: Coincident(g340,g339)
    c: Coincident(g340,g3)
    c: Coincident(g341,g339)
    c: Coincident(g341,g3)
    c: Block(g341)
    c: Block(g340)
    c: Weight(g342) = 1
    c: Equal(g342,g344)
    c: InternalAlignment(g342,g345)
    c: InternalAlignment(g343,g345)
    c: InternalAlignment(g344,g345)
    c: InternalAlignment(g346,g345)
    c: InternalAlignment(g347,g345)
    c: InternalAlignment(g352,g351)
    c: InternalAlignment(g353,g351)
    c: InternalAlignment(g355,g357)
    c: Horizontal(g369)
    c: Coincident(g370,g0)
    c: Horizontal(g370)
    c: Block(g370)
    c: Distance(g370) = 450
    c: Horizontal(g371)
    c: Distance(g371) = 12
    c: Coincident(g373,g371)
    c: Vertical(g373)
    c: Horizontal(g374)
    c: Vertical(g375)
    c: Distance(g375) = 6
    c: Coincident(g375,g371)
    c: Coincident(g374,g371)
    c: Block(g373)
    c: Coincident(g376,g373)
    c: Horizontal(g376)
    c: Distance(g376) = 6
    c: Vertical(g377)
    c: Distance(g377) = 3
    c: Vertical(g378)
    c: Distance(g378) = 3
    c: Coincident(g372,g377)
    c: Coincident(g384,g378)
    c: Weight(g379) = 1
    c: Equal(g379,g380)
    c: Coincident(g380,g374)
    c: Equal(g379,g381)
    c: Coincident(g381,g375)
    c: Equal(g379,g382)
    c: Coincident(g382,g376)
    c: Equal(g379,g383)
    c: Coincident(g384,g377)
    c: InternalAlignment(g379-g383 -> g384) x5
    c: InternalAlignment(g385,g384)
    c: InternalAlignment(g386,g384)
    c: InternalAlignment(g387,g384)
    c: Coincident(g388,g164)
    c: Coincident(g388,g158)
    c: Coincident(g392,g390)
    c: Vertical(g393)
    c: Distance(g393) = 6
    c: Coincident(g393,g390)
    c: Vertical(g394)
    c: Distance(g394) = 3
    c: Vertical(g395)
    c: Distance(g395) = 6
    c: Coincident(g395,g394)
    c: Coincident(g401,g394)
    c: Weight(g396) = 1
    c: Equal(g396,g397)
    c: Coincident(g397,g392)
    c: Equal(g396,g398)
    c: Coincident(g398,g393)
    c: Equal(g396,g399)
    c: Equal(g396,g400)
    c: Coincident(g401,g395)
    c: InternalAlignment(g396-g400 -> g401) x5
    c: InternalAlignment(g402,g401)
    c: InternalAlignment(g403,g401)
    c: InternalAlignment(g404,g401)
    c: Coincident(g405,g389)
    c: Coincident(g405,g170)
    c: Horizontal(g405)
    c: Block(g401)
    c: Coincident(g406,g176)
    c: Coincident(g406,g389)
    c: Horizontal(g406)
    c: Block(g405)
    c: Coincident(g408,g389)
    c: PointOnObject(g408,g153)
    c: Vertical(g408)
    c: Block(g409)
    c: Coincident(g410,g409)
    c: Vertical(g410)
    c: PointOnObject(g410,g40)
    c: Block(g410)
    c: Coincident(g411,g409)
    c: Vertical(g411)
    c: Block(g411)
    c: Vertical(g412)
    c: Distance(g412) = 3
    c: Equal(g379,g415) = 1
    c: Equal(g415,g416)
    c: InternalAlignment(g415,g417)
    c: InternalAlignment(g416,g417)
    c: InternalAlignment(g413,g417)
    c: InternalAlignment(g414,g417)
    c: InternalAlignment(g418,g417)
    c: Block(g417)
    c: Coincident(g418,g412)
    c: Coincident(g419,g417)
    c: PointOnObject(g419,g150)
    c: Vertical(g419)
    c: Distance(g420) = 3
    c: Block(g420)
    c: Distance(g421) = 3
    c: Parallel(g421,g420)
    c: Coincident(g421,g420)
    c: Coincident(g422,g420)
    c: Perpendicular(g422,g420)
    c: Distance(g422) = 3
    c: Coincident(g423,g421)
    c: Perpendicular(g423,g421)
    c: Distance(g423) = 3
    c: Coincident(g424,g420)
    c: Perpendicular(g424,g421)
    c: Distance(g424) = 6
    c: Coincident(g425,g424)
    c: PointOnObject(g423,g425)
    c: Coincident(g426,g420)
    c: PointOnObject(g426,g79)
    c: Block(g426)
    c: Distance(g427) = 2.76
    c: Coincident(g428,g427)
    c: Parallel(g427,g428)
    c: PointOnObject(g428,g181)
    c: Distance(g428) = 2.41
    c: Block(g428)
    c: Coincident(g429,g427)
    c: Distance(g429) = 6.6
    c: Perpendicular(g429,g428)
    c: Distance(g430) = 6.6
    c: Coincident(g431,g429)
    c: Coincident(g431,g430)
    c: Block(g432)
    c: Coincident(g433,g432)
    c: Vertical(g433)
    c: Distance(g433) = 3.6
    c: Coincident(g434,g427)
    c: Parallel(g427,g434)
    c: PointOnObject(g434,g78)
    c: Block(g434)
    c: Coincident(g435,g421)
    c: Parallel(g435,g421)
    c: PointOnObject(g435,g211)
    c: Block(g435)
    c: Coincident(g436,g435)
    c: Vertical(g436)
    c: PointOnObject(g436,g210)
    c: Coincident(g437,g436)
    c: Perpendicular(g437,g210)
    c: Distance(g437) = 3
    c: Coincident(g438,g437)
    c: Block(g437)
    c: Distance(g438) = 3
    c: Parallel(g437,g438)
    c: Coincident(g439,g438)
    c: Distance(g439) = 3
    c: Parallel(g438,g439)
    c: Coincident(g440,g439)
    c: Parallel(g440,g437)
    c: PointOnObject(g440,g124)
    c: PointOnObject(g441,g53)
    c: Tangent(g440,g441)
    c: Coincident(g442,g439)
    c: Perpendicular(g442,g439)
    c: Coincident(g443,g437)
    c: Parallel(g443,g442)
    c: Distance(g443) = 3
    c: Distance(g442) = 3
    c: PointOnObject(g442,g444)
    c: Block(g444)
    c: PointOnObject(g445,g123)
    c: Perpendicular(g123,g445)
    c: Distance(g445) = 2.41
    c: Block(g445)
    c: Coincident(g446,g445)
    c: Perpendicular(g123,g446)
    c: Distance(g446) = 2.76
    c: Coincident(g447,g446)
    c: Perpendicular(g123,g447)
    c: PointOnObject(g447,g149)
    c: Coincident(g448,g445)
    c: Parallel(g123,g448)
    c: Distance(g448) = 6.6
    c: Coincident(g449,g446)
    c: Parallel(g123,g449)
    c: Coincident(g450,g448)
    c: Distance(g449) = 6.6
    c: Coincident(g449,g450)
    c: Block(g149)
    c: Block(g124)
    c: Block(g211)
    c: Block(g181)
    c: Block(g78)
    c: Block(g79)
    c: Block(g430)
    c: Coincident(g451,g447)
    c: Distance(g451) = 46
    c: Parallel(g149,g451)
    c: Coincident(g452,g451)
    c: Horizontal(g452)
    c: PointOnObject(g452,g154)
    c: Coincident(g453,g451)
    c: Vertical(g453)
    c: Distance(g453) = 9
    c: Block(g452)
    c: PointOnObject(g454,g93)
    c: Distance(g455) = 6.6
    c: Distance(g456) = 6.6
    c: Block(g454)
    c: Coincident(g457,g456)
    c: Coincident(g457,g455)
    c: Perpendicular(g457,g182)
    c: Coincident(g458,g455)
    c: Perpendicular(g458,g182)
    c: PointOnObject(g458,g182)
    c: Block(g458)
    c: Block(g457)
    c: Block(g456)
    c: PointOnObject(g459,g196)
    c: Perpendicular(g196,g459)
    c: Distance(g459) = 3
    c: Coincident(g460,g459)
    c: Perpendicular(g196,g460)
    c: Distance(g460) = 3
    c: Coincident(g461,g460)
    c: Perpendicular(g196,g461)
    c: Distance(g461) = 3
    c: Coincident(g462,g461)
    c: Tangent(g462,g41)
    c: PointOnObject(g462,g94)
    c: Block(g462)
    c: Block(g459)
    c: Coincident(g463,g459)
    c: Parallel(g196,g463)
    c: Distance(g463) = 3
    c: Coincident(g464,g461)
    c: Distance(g464) = 3
    c: Parallel(g196,g464)
    c: Coincident(g465,g460)
    c: Distance(g465) = 6
    c: Parallel(g465,g196)
    c: Coincident(g466,g465)
    c: PointOnObject(g464,g466)
    c: Block(g466)
    c: Coincident(g467,g458)
    c: Vertical(g467)
    c: PointOnObject(g467,g195)
    c: Coincident(g468,g467)
    c: Perpendicular(g195,g468)
FEATURE [Sketcher::SketchObject] Sketch004  label="rightSideBottom"
  FullyConstrained = false
  sketch-geometry (91):
    g0: ArcOfCircle CenterX=391.073 CenterY=-83.7794 CenterZ=0 NormalX=0 NormalY=0 NormalZ=1 AngleXU=0 Radius=8 StartAngle=3.14159 EndAngle=6.28319
    g1: Circle CenterX=306.073 CenterY=-81.8102 CenterZ=0 NormalX=0 NormalY=0 NormalZ=1 AngleXU=0 Radius=1
    g2: Circle CenterX=306.073 CenterY=-77.8102 CenterZ=0 NormalX=0 NormalY=0 NormalZ=1 AngleXU=0 Radius=1
    g3: Circle CenterX=302.567 CenterY=-42.9683 CenterZ=0 NormalX=0 NormalY=0 NormalZ=1 AngleXU=0 Radius=1
    g4: Circle CenterX=306.073 CenterY=-44.8935 CenterZ=0 NormalX=0 NormalY=0 NormalZ=1 AngleXU=0 Radius=1
    g5: Circle CenterX=306.073 CenterY=-40.8935 CenterZ=0 NormalX=0 NormalY=0 NormalZ=1 AngleXU=0 Radius=1
    g6: BSplineCurve PolesCount=3 KnotsCount=2 Degree=2 IsPeriodic=0
    g7: GeomPoint X=302.567 Y=-42.9683 Z=0
    g8: GeomPoint X=306.073 Y=-40.8935 Z=0
    g9: Circle CenterX=371.567 CenterY=-80.8644 CenterZ=0 NormalX=0 NormalY=0 NormalZ=1 AngleXU=0 Radius=1
    g10: Circle CenterX=375.073 CenterY=-82.7896 CenterZ=0 NormalX=0 NormalY=0 NormalZ=1 AngleXU=0 Radius=1
    g11: Circle CenterX=375.073 CenterY=-78.7896 CenterZ=0 NormalX=0 NormalY=0 NormalZ=1 AngleXU=0 Radius=1
    g12: GeomPoint X=371.567 Y=-80.8644 Z=0
    g13: GeomPoint X=375.073 Y=-78.7896 Z=0
    g14: Circle CenterX=318.073 CenterY=-51.4823 CenterZ=0 NormalX=0 NormalY=0 NormalZ=1 AngleXU=0 Radius=1
    g15: Circle CenterX=318.073 CenterY=-47.4805 CenterZ=0 NormalX=0 NormalY=0 NormalZ=1 AngleXU=0 Radius=1
    g16: GeomPoint X=321.579 Y=-53.4075 Z=0
    g17: GeomPoint X=318.073 Y=-47.4805 Z=0
    g18: Circle CenterX=321.579 CenterY=-67.3492 CenterZ=0 NormalX=0 NormalY=0 NormalZ=1 AngleXU=0 Radius=1
    g19: Circle CenterX=318.073 CenterY=-65.424 CenterZ=0 NormalX=0 NormalY=0 NormalZ=1 AngleXU=0 Radius=1
    g20: Circle CenterX=318.073 CenterY=-69.424 CenterZ=0 NormalX=0 NormalY=0 NormalZ=1 AngleXU=0 Radius=1
    g21: GeomPoint X=321.579 Y=-67.3492 Z=0
    g22: GeomPoint X=318.073 Y=-69.424 Z=0
    g23: Circle CenterX=362.567 CenterY=-89.8542 CenterZ=0 NormalX=0 NormalY=0 NormalZ=1 AngleXU=0 Radius=1
    g24: Circle CenterX=366.073 CenterY=-91.7794 CenterZ=0 NormalX=0 NormalY=0 NormalZ=1 AngleXU=0 Radius=1
    g25: Circle CenterX=362.073 CenterY=-91.7794 CenterZ=0 NormalX=0 NormalY=0 NormalZ=1 AngleXU=0 Radius=1
    g26: GeomPoint X=362.567 Y=-89.8542 Z=0
    g27: GeomPoint X=362.073 Y=-91.7794 Z=0
    g28: Circle CenterX=322.073 CenterY=-91.7794 CenterZ=0 NormalX=0 NormalY=0 NormalZ=1 AngleXU=0 Radius=1
    g29: Circle CenterX=318.073 CenterY=-91.7794 CenterZ=0 NormalX=0 NormalY=0 NormalZ=1 AngleXU=0 Radius=1
    g30: Circle CenterX=318.073 CenterY=-87.7794 CenterZ=0 NormalX=0 NormalY=0 NormalZ=1 AngleXU=0 Radius=1
    g31: GeomPoint X=322.073 Y=-91.7794 Z=0
    g32: GeomPoint X=318.073 Y=-87.7794 Z=0
    g33: ArcOfCircle CenterX=391.073 CenterY=22.1087 CenterZ=0 NormalX=0 NormalY=0 NormalZ=1 AngleXU=0 Radius=4 StartAngle=0 EndAngle=3.14159
    g34: LineSegment StartX=387.073 StartY=22.1087 StartZ=0 EndX=383.073 EndY=-83.7794 EndZ=0
    g35: LineSegment StartX=395.073 StartY=22.1087 StartZ=0 EndX=399.073 EndY=-83.7794 EndZ=0
    g36: LineSegment StartX=232.072 StartY=-103.779 StartZ=0 EndX=232.072 EndY=-100.779 EndZ=0
    g37: GeomPoint X=232.072 Y=-94.7794 Z=0
    g38: GeomPoint X=223.072 Y=-97.7794 Z=0
    g39: Circle CenterX=232.072 CenterY=-94.7794 CenterZ=0 NormalX=0 NormalY=0 NormalZ=1 AngleXU=0 Radius=1
    g40: Circle CenterX=232.072 CenterY=-100.779 CenterZ=0 NormalX=0 NormalY=0 NormalZ=1 AngleXU=0 Radius=1
    g41: BSplineCurve PolesCount=5 KnotsCount=3 Degree=3 IsPeriodic=0
    g42: GeomPoint X=232.072 Y=-100.779 Z=0
    g43: LineSegment StartX=232.072 StartY=-94.7794 StartZ=0 EndX=232.072 EndY=-91.7794 EndZ=0
    g44: LineSegment StartX=245.072 StartY=-31.3037 StartZ=0 EndX=243.535 EndY=-33.1602 EndZ=0
    g45: LineSegment StartX=241.775 StartY=-35.2862 StartZ=0 EndX=240.266 EndY=-37.1092 EndZ=0
    g46: LineSegment StartX=243.535 StartY=-33.1602 StartZ=0 EndX=248.619 EndY=-37.3688 EndZ=0
    g47: LineSegment StartX=241.775 StartY=-35.2862 StartZ=0 EndX=246.859 EndY=-39.4949 EndZ=0
    g48: LineSegment StartX=248.619 StartY=-37.3688 StartZ=0 EndX=246.859 EndY=-39.4949 EndZ=0
    g49: LineSegment StartX=232.072 StartY=-103.779 StartZ=0 EndX=407.073 EndY=-103.779 EndZ=0
    g50: LineSegment StartX=299.888 StartY=-86.6413 StartZ=0 EndX=240.266 EndY=-37.1092 EndZ=0
    g51: LineSegment StartX=245.072 StartY=-11.4025 StartZ=0 EndX=302.567 EndY=-42.9683 EndZ=0
    g52: BSplineCurve PolesCount=3 KnotsCount=2 Degree=2 IsPeriodic=0
    g53: BSplineCurve PolesCount=3 KnotsCount=2 Degree=2 IsPeriodic=0
    g54: LineSegment StartX=321.579 StartY=-53.4075 StartZ=0 EndX=371.567 EndY=-80.8644 EndZ=0
    g55: BSplineCurve PolesCount=3 KnotsCount=2 Degree=2 IsPeriodic=0
    g56: BSplineCurve PolesCount=3 KnotsCount=2 Degree=2 IsPeriodic=0
    g57: BSplineCurve PolesCount=3 KnotsCount=2 Degree=2 IsPeriodic=0
    g58: LineSegment StartX=318.073 StartY=-69.424 StartZ=0 EndX=318.073 EndY=-87.7794 EndZ=0
    g59: LineSegment StartX=321.579 StartY=-67.3492 StartZ=0 EndX=362.567 EndY=-89.8542 EndZ=0
    g60: LineSegment StartX=362.073 StartY=-91.7794 StartZ=0 EndX=322.073 EndY=-91.7794 EndZ=0
    g61: BSplineCurve PolesCount=3 KnotsCount=2 Degree=2 IsPeriodic=0
    g62: BSplineCurve PolesCount=3 KnotsCount=2 Degree=2 IsPeriodic=0
    g63: LineSegment StartX=245.072 StartY=-31.3037 StartZ=0 EndX=302.996 EndY=-79.2541 EndZ=0
    g64: LineSegment StartX=302.567 StartY=-56.9099 StartZ=0 EndX=239.193 EndY=-22.1109 EndZ=0
    g65: LineSegment StartX=306.073 StartY=-62.8351 StartZ=0 EndX=306.073 EndY=-77.8102 EndZ=0
    g66: BSplineCurve PolesCount=3 KnotsCount=2 Degree=2 IsPeriodic=0
    g67: LineSegment StartX=298.776 StartY=-91.7794 StartZ=0 EndX=232.072 EndY=-91.7794 EndZ=0
    g68: LineSegment StartX=245.072 StartY=-11.4025 StartZ=0 EndX=243.628 EndY=-14.0323 EndZ=0
    g69: LineSegment StartX=240.741 StartY=-19.2917 StartZ=0 EndX=239.193 EndY=-22.1109 EndZ=0
    g70: LineSegment StartX=243.628 StartY=-14.0323 StartZ=0 EndX=246.258 EndY=-15.476 EndZ=0
    g71: LineSegment StartX=240.741 StartY=-19.2917 StartZ=0 EndX=243.37 EndY=-20.7355 EndZ=0
    g72: ArcOfCircle CenterX=247.444 CenterY=-19.5495 CenterZ=0 NormalX=0 NormalY=0 NormalZ=1 AngleXU=0 Radius=4.24264 StartAngle=3.4249 EndAngle=8.13729
    g73: LineSegment StartX=407.073 StartY=-103.779 StartZ=0 EndX=407.073 EndY=48.2206 EndZ=0
    g74: LineSegment StartX=375.073 StartY=48.2206 StartZ=0 EndX=375.073 EndY=-78.7896 EndZ=0
    g75: LineSegment StartX=375.073 StartY=48.2206 StartZ=0 EndX=382.073 EndY=48.2206 EndZ=0
    g76: LineSegment StartX=407.073 StartY=48.2206 StartZ=0 EndX=400.073 EndY=48.2206 EndZ=0
    g77: LineSegment StartX=394.073 StartY=48.2206 StartZ=0 EndX=394.073 EndY=52.2206 EndZ=0
    g78: LineSegment StartX=388.073 StartY=48.2206 StartZ=0 EndX=388.073 EndY=58.2206 EndZ=0
    g79: ArcOfCircle CenterX=385.073 CenterY=61.2206 CenterZ=0 NormalX=0 NormalY=0 NormalZ=1 AngleXU=0 Radius=4.24264 StartAngle=5.49779 EndAngle=10.2102
    g80: ArcOfCircle CenterX=397.073 CenterY=55.2206 CenterZ=0 NormalX=0 NormalY=0 NormalZ=1 AngleXU=0 Radius=4.24264 StartAngle=5.49779 EndAngle=10.2102
    g81: LineSegment StartX=382.073 StartY=58.2206 StartZ=0 EndX=382.073 EndY=48.2206 EndZ=0
    g82: LineSegment StartX=400.073 StartY=52.2206 StartZ=0 EndX=400.073 EndY=48.2206 EndZ=0
    g83: LineSegment StartX=394.073 StartY=48.2206 StartZ=0 EndX=388.073 EndY=48.2206 EndZ=0
    g84: LineSegment StartX=306.073 StartY=-40.8935 StartZ=0 EndX=306.073 EndY=-27.5935 EndZ=0
    g85: LineSegment StartX=318.073 StartY=-27.5935 StartZ=0 EndX=318.073 EndY=-47.4805 EndZ=0
    g86: LineSegment StartX=306.073 StartY=-27.5935 StartZ=0 EndX=310.073 EndY=-27.5935 EndZ=0
    g87: LineSegment StartX=318.073 StartY=-27.5935 StartZ=0 EndX=314.073 EndY=-27.5935 EndZ=0
    g88: LineSegment StartX=310.073 StartY=-27.5935 StartZ=0 EndX=310.073 EndY=-31.5935 EndZ=0
    g89: LineSegment StartX=314.073 StartY=-27.5935 StartZ=0 EndX=314.073 EndY=-31.5935 EndZ=0
    g90: ArcOfCircle CenterX=312.073 CenterY=-33.5935 CenterZ=0 NormalX=0 NormalY=0 NormalZ=1 AngleXU=0 Radius=2.82843 StartAngle=2.35619 EndAngle=7.06858
  constraints (121):
    c: Distance(g44) = 2.41
    c: Block(g44)
    c: Coincident(g46,g44)
    c: Coincident(g49,g36)
    c: Horizontal(g49)
    c: Block(g49)
    c: Coincident(g50,g45)
    c: Block(g50)
    c: Coincident(g51,g6)
    c: Block(g51)
    c: Coincident(g54,g52)
    c: Coincident(g54,g53)
    c: Coincident(g58,g56)
    c: Coincident(g58,g57)
    c: Vertical(g58)
    c: Coincident(g59,g56)
    c: Coincident(g59,g55)
    c: Coincident(g60,g55)
    c: Coincident(g60,g57)
    c: Horizontal(g60)
    c: Block(g61)
    c: Block(g62)
    c: Coincident(g63,g44)
    c: Coincident(g63,g62)
    c: Coincident(g64,g61)
    c: Coincident(g65,g61)
    c: Coincident(g65,g62)
    c: Vertical(g65)
    c: Block(g66)
    c: Coincident(g66,g50)
    c: Coincident(g67,g66)
    c: Coincident(g67,g43)
    c: Horizontal(g67)
    c: Coincident(g68,g51)
    c: Perpendicular(g68,g51)
    c: Coincident(g69,g64)
    c: Coincident(g70,g68)
    c: Distance(g70) = 3
    c: Distance(g71) = 3
    c: Perpendicular(g68,g70)
    c: Coincident(g72,g70)
    c: Coincident(g72,g71)
    c: Block(g72)
    c: Block(g69)
    c: Block(g71)
    c: Block(g54)
    c: Block(g59)
    c: Block(g58)
    c: Block(g60)
    c: Block(g67)
    c: Block(g43)
    c: Block(g36)
    c: Block(g48)
    c: Block(g46)
    c: Block(g47)
    c: Block(g45)
    c: Block(g35)
    c: Block(g34)
    c: Block(g0)
    c: Block(g33)
    c: Block(g52)
    c: Block(g6)
    c: Block(g41)
    c: Block(g57)
    c: Block(g55)
    c: Block(g53)
    c: Block(g68)
    c: Distance(g48) = 2.76
    c: Distance(g47) = 6.6
    c: Distance(g45) = 2.36657
    c: Coincident(g73,g49)
    c: Vertical(g73)
    c: Distance(g73) = 152
    c: Coincident(g74,g53)
    c: Vertical(g74)
    c: Block(g74)
    c: Coincident(g75,g74)
    c: Horizontal(g75)
    c: Distance(g75) = 7
    c: Horizontal(g76)
    c: Distance(g76) = 7
    c: Coincident(g76,g73)
    c: Vertical(g77)
    c: Distance(g77) = 4
    c: Vertical(g78)
    c: Distance(g78) = 10
    c: Coincident(g79,g78)
    c: Coincident(g80,g77)
    c: Block(g80)
    c: Block(g79)
    c: Coincident(g81,g79)
    c: Coincident(g81,g75)
    c: Vertical(g81)
    c: Coincident(g82,g80)
    c: Coincident(g82,g76)
    c: Vertical(g82)
    c: Coincident(g83,g77)
    c: Coincident(g83,g78)
    c: Horizontal(g83)
    c: Coincident(g84,g6)
    c: Vertical(g84)
    c: Distance(g84) = 13.3
    c: Coincident(g85,g52)
    c: Vertical(g85)
    c: Block(g85)
    c: Coincident(g86,g84)
    c: Horizontal(g86)
    c: Distance(g86) = 4
    c: Coincident(g87,g85)
    c: Horizontal(g87)
    c: Distance(g87) = 4
    c: Coincident(g88,g86)
    c: Vertical(g88)
    c: Coincident(g89,g87)
    c: Vertical(g89)
    c: Distance(g88) = 4
    c: Distance(g89) = 4
    c: Coincident(g90,g88)
    c: Coincident(g90,g89)
    c: Block(g90)
    c: Block(g56)
FEATURE [Sketcher::SketchObject] Sketch005  label="middleTop"
  FullyConstrained = true
  sketch-geometry (133):
    g0: Circle CenterX=175.025 CenterY=27.0667 CenterZ=0 NormalX=0 NormalY=0 NormalZ=1 AngleXU=0 Radius=1
    g1: Circle CenterX=179.022 CenterY=24.8665 CenterZ=0 NormalX=0 NormalY=0 NormalZ=1 AngleXU=0 Radius=1
    g2: Circle CenterX=179.022 CenterY=27.0606 CenterZ=0 NormalX=0 NormalY=0 NormalZ=1 AngleXU=0 Radius=1
    g3: BSplineCurve PolesCount=3 KnotsCount=2 Degree=2 IsPeriodic=0
    g4: GeomPoint X=175.025 Y=27.0667 Z=0
    g5: GeomPoint X=179.022 Y=27.0606 Z=0
    g6: Circle CenterX=189.124 CenterY=27.0628 CenterZ=0 NormalX=0 NormalY=0 NormalZ=1 AngleXU=0 Radius=1
    g7: Circle CenterX=185.124 CenterY=24.8665 CenterZ=0 NormalX=0 NormalY=0 NormalZ=1 AngleXU=0 Radius=1
    g8: Circle CenterX=185.124 CenterY=27.0606 CenterZ=0 NormalX=0 NormalY=0 NormalZ=1 AngleXU=0 Radius=1
    g9: BSplineCurve PolesCount=3 KnotsCount=2 Degree=2 IsPeriodic=0
    g10: GeomPoint X=189.124 Y=27.0628 Z=0
    g11: GeomPoint X=185.124 Y=27.0606 Z=0
    g12: Circle CenterX=165.871 CenterY=18.1458 CenterZ=0 NormalX=0 NormalY=0 NormalZ=1 AngleXU=0 Radius=1
    g13: Circle CenterX=169.377 CenterY=16.2206 CenterZ=0 NormalX=0 NormalY=0 NormalZ=1 AngleXU=0 Radius=1
    g14: Circle CenterX=165.871 CenterY=14.2956 CenterZ=0 NormalX=0 NormalY=0 NormalZ=1 AngleXU=0 Radius=1
    g15: BSplineCurve PolesCount=3 KnotsCount=2 Degree=2 IsPeriodic=0
    g16: GeomPoint X=165.871 Y=18.1458 Z=0
    g17: GeomPoint X=165.871 Y=14.2956 Z=0
    g18: Circle CenterX=198.275 CenterY=18.1318 CenterZ=0 NormalX=0 NormalY=0 NormalZ=1 AngleXU=0 Radius=1
    g19: Circle CenterX=194.768 CenterY=16.2206 CenterZ=0 NormalX=0 NormalY=0 NormalZ=1 AngleXU=0 Radius=1
    g20: Circle CenterX=198.264 CenterY=14.2963 CenterZ=0 NormalX=0 NormalY=0 NormalZ=1 AngleXU=0 Radius=1
    g21: BSplineCurve PolesCount=3 KnotsCount=2 Degree=2 IsPeriodic=0
    g22: GeomPoint X=198.275 Y=18.1318 Z=0
    g23: GeomPoint X=198.264 Y=14.2963 Z=0
    g24: Circle CenterX=125.607 CenterY=54.1951 CenterZ=0 NormalX=0 NormalY=0 NormalZ=1 AngleXU=0 Radius=1
    g25: Circle CenterX=139.632 CenterY=46.4944 CenterZ=0 NormalX=0 NormalY=0 NormalZ=1 AngleXU=0 Radius=1
    g26: Circle CenterX=127.326 CenterY=56.7187 CenterZ=0 NormalX=0 NormalY=0 NormalZ=1 AngleXU=0 Radius=1
    g27: BSplineCurve PolesCount=3 KnotsCount=2 Degree=2 IsPeriodic=0
    g28: GeomPoint X=125.607 Y=54.1951 Z=0
    g29: GeomPoint X=127.326 Y=56.7187 Z=0
    g30: Circle CenterX=236.824 CenterY=56.7187 CenterZ=0 NormalX=0 NormalY=0 NormalZ=1 AngleXU=0 Radius=1
    g31: Circle CenterX=224.513 CenterY=46.4944 CenterZ=0 NormalX=0 NormalY=0 NormalZ=1 AngleXU=0 Radius=1
    g32: Circle CenterX=238.538 CenterY=54.1951 CenterZ=0 NormalX=0 NormalY=0 NormalZ=1 AngleXU=0 Radius=1
    g33: BSplineCurve PolesCount=3 KnotsCount=2 Degree=2 IsPeriodic=0
    g34: GeomPoint X=236.824 Y=56.7187 Z=0
    g35: GeomPoint X=238.538 Y=54.1951 Z=0
    g36: Circle CenterX=189.121 CenterY=124.221 CenterZ=0 NormalX=0 NormalY=0 NormalZ=1 AngleXU=0 Radius=1
    g37: Circle CenterX=185.124 CenterY=124.221 CenterZ=0 NormalX=0 NormalY=0 NormalZ=1 AngleXU=0 Radius=1
    g38: Circle CenterX=185.124 CenterY=120.221 CenterZ=0 NormalX=0 NormalY=0 NormalZ=1 AngleXU=0 Radius=1
    g39: BSplineCurve PolesCount=3 KnotsCount=2 Degree=2 IsPeriodic=0
    g40: GeomPoint X=189.121 Y=124.221 Z=0
    g41: GeomPoint X=185.124 Y=120.221 Z=0
    g42: Circle CenterX=175.022 CenterY=124.221 CenterZ=0 NormalX=0 NormalY=0 NormalZ=1 AngleXU=0 Radius=1
    g43: Circle CenterX=179.022 CenterY=124.221 CenterZ=0 NormalX=0 NormalY=0 NormalZ=1 AngleXU=0 Radius=1
    g44: Circle CenterX=179.022 CenterY=120.221 CenterZ=0 NormalX=0 NormalY=0 NormalZ=1 AngleXU=0 Radius=1
    g45: BSplineCurve PolesCount=3 KnotsCount=2 Degree=2 IsPeriodic=0
    g46: GeomPoint X=175.022 Y=124.221 Z=0
    g47: GeomPoint X=179.022 Y=120.221 Z=0
    g48: LineSegment StartX=232.071 StartY=124.221 StartZ=0 EndX=232.071 EndY=127.221 EndZ=0
    g49-g52: Circle x4 (B-spline internal-alignment scaffolding for g53; pole/knot coordinates omitted)
    g53: BSplineCurve PolesCount=5 KnotsCount=3 Degree=3 IsPeriodic=0
    g54: GeomPoint X=232.072 Y=133.221 Z=0
    g55: GeomPoint X=223.072 Y=130.221 Z=0
    g56: GeomPoint X=232.071 Y=127.221 Z=0
    g57-g61: Circle x5 (B-spline internal-alignment scaffolding for g62; pole/knot coordinates omitted)
    g62: BSplineCurve PolesCount=5 KnotsCount=3 Degree=3 IsPeriodic=0
    g63: GeomPoint X=132.072 Y=133.221 Z=0
    g64: GeomPoint X=141.072 Y=130.221 Z=0
    g65: GeomPoint X=132.072 Y=127.221 Z=0
    g66: ArcOfCircle CenterX=247.391 CenterY=52.0843 CenterZ=0 NormalX=0 NormalY=0 NormalZ=1 AngleXU=0 Radius=4.24264 StartAngle=4.42912 EndAngle=9.14151
    g67: LineSegment StartX=240.687 StartY=51.8263 StartZ=0 EndX=239.192 EndY=54.5542 EndZ=0
    g68: LineSegment StartX=243.575 StartY=46.5669 StartZ=0 EndX=245.072 EndY=43.8408 EndZ=0
    g69: LineSegment StartX=240.168 StartY=69.471 StartZ=0 EndX=241.708 EndY=67.6172 EndZ=0
    g70: LineSegment StartX=246.783 StartY=71.8328 StartZ=0 EndX=248.546 EndY=69.7098 EndZ=0
    g71: LineSegment StartX=245.073 StartY=63.5726 StartZ=0 EndX=243.476 EndY=65.4955 EndZ=0
    g72: LineSegment StartX=123.967 StartY=69.4706 StartZ=0 EndX=122.37 EndY=67.5474 EndZ=0
    g73: LineSegment StartX=232.072 StartY=133.221 StartZ=0 EndX=232.072 EndY=136.221 EndZ=0
    g74: LineSegment StartX=232.072 StartY=136.221 StartZ=0 EndX=132.072 EndY=136.221 EndZ=0
    g75: LineSegment StartX=132.072 StartY=136.221 StartZ=0 EndX=132.072 EndY=133.221 EndZ=0
    g76: LineSegment StartX=132.072 StartY=127.221 StartZ=0 EndX=132.072 EndY=124.221 EndZ=0
    g77: LineSegment StartX=132.072 StartY=124.221 StartZ=0 EndX=175.022 EndY=124.221 EndZ=0
    g78: LineSegment StartX=189.121 StartY=124.221 StartZ=0 EndX=232.071 EndY=124.221 EndZ=0
    g79: LineSegment StartX=185.124 StartY=120.221 StartZ=0 EndX=185.124 EndY=27.0606 EndZ=0
    g80: LineSegment StartX=189.124 StartY=27.0628 StartZ=0 EndX=240.168 EndY=69.471 EndZ=0
    g81: LineSegment StartX=241.708 StartY=67.6172 StartZ=0 EndX=246.783 EndY=71.8328 EndZ=0
    g82: LineSegment StartX=248.546 StartY=69.7098 StartZ=0 EndX=243.476 EndY=65.4955 EndZ=0
    g83: LineSegment StartX=245.073 StartY=63.5726 StartZ=0 EndX=236.824 EndY=56.7187 EndZ=0
    g84: LineSegment StartX=238.538 StartY=54.1951 StartZ=0 EndX=239.192 EndY=54.5542 EndZ=0
    g85: LineSegment StartX=240.687 StartY=51.8263 StartZ=0 EndX=243.317 EndY=53.2701 EndZ=0
    g86: LineSegment StartX=246.205 StartY=48.0108 StartZ=0 EndX=243.575 EndY=46.5669 EndZ=0
    g87: LineSegment StartX=245.072 StartY=43.8408 StartZ=0 EndX=198.275 EndY=18.1318 EndZ=0
    g88: LineSegment StartX=165.871 StartY=18.1458 StartZ=0 EndX=118.934 EndY=43.9178 EndZ=0
    g89: LineSegment StartX=118.934 StartY=43.9178 StartZ=0 EndX=120.377 EndY=46.5474 EndZ=0
    g90: LineSegment StartX=117.748 StartY=47.9913 StartZ=0 EndX=120.377 EndY=46.5474 EndZ=0
    g91: LineSegment StartX=120.635 StartY=53.2507 StartZ=0 EndX=123.265 EndY=51.8068 EndZ=0
    g92: LineSegment StartX=123.265 StartY=51.8068 StartZ=0 EndX=124.73 EndY=54.6766 EndZ=0
    g93: ArcOfCircle CenterX=116.562 CenterY=52.0649 CenterZ=0 NormalX=0 NormalY=0 NormalZ=1 AngleXU=0 Radius=4.24264 StartAngle=0.283267 EndAngle=4.99566
    g94: LineSegment StartX=124.73 StartY=54.6766 StartZ=0 EndX=125.607 EndY=54.1951 EndZ=0
    g95: LineSegment StartX=127.326 StartY=56.7187 StartZ=0 EndX=119.072 EndY=63.5741 EndZ=0
    g96: LineSegment StartX=119.072 StartY=63.5741 StartZ=0 EndX=120.669 EndY=65.4973 EndZ=0
    g97: LineSegment StartX=120.669 StartY=65.4973 StartZ=0 EndX=115.591 EndY=69.7147 EndZ=0
    g98: LineSegment StartX=115.591 StartY=69.7147 StartZ=0 EndX=117.293 EndY=71.7641 EndZ=0
    g99: LineSegment StartX=117.293 StartY=71.7641 StartZ=0 EndX=122.37 EndY=67.5474 EndZ=0
    g100: LineSegment StartX=123.967 StartY=69.4706 StartZ=0 EndX=175.025 EndY=27.0667 EndZ=0
    g101: LineSegment StartX=179.022 StartY=27.0606 StartZ=0 EndX=179.022 EndY=120.221 EndZ=0
    g102-g117: Circle x16 (B-spline internal-alignment scaffolding for g118; pole/knot coordinates omitted)
    g118: BSplineCurve PolesCount=16 KnotsCount=14 Degree=3 IsPeriodic=0
    g119-g132: GeomPoint x14 (B-spline internal-alignment scaffolding for g118; pole/knot coordinates omitted)
  constraints (180):
    c: Weight(g0) = 1
    c: Equal(g0,g1)
    c: Equal(g0,g2)
    c: InternalAlignment(g0,g3)
    c: InternalAlignment(g1,g3)
    c: InternalAlignment(g2,g3)
    c: InternalAlignment(g4,g3)
    c: InternalAlignment(g5,g3)
    c: Weight(g6) = 1
    c: Equal(g6,g7)
    c: Equal(g6,g8)
    c: InternalAlignment(g6,g9)
    c: InternalAlignment(g7,g9)
    c: InternalAlignment(g8,g9)
    c: InternalAlignment(g10,g9)
    c: InternalAlignment(g11,g9)
    c: Block(g9)
    c: Block(g3)
    c: Weight(g12) = 1
    c: Equal(g12,g13)
    c: Equal(g12,g14)
    c: InternalAlignment(g12,g15)
    c: InternalAlignment(g13,g15)
    c: InternalAlignment(g14,g15)
    c: InternalAlignment(g16,g15)
    c: InternalAlignment(g17,g15)
    c: Weight(g18) = 1
    c: Equal(g18,g19)
    c: Equal(g18,g20)
    c: InternalAlignment(g18,g21)
    c: InternalAlignment(g19,g21)
    c: InternalAlignment(g20,g21)
    c: InternalAlignment(g22,g21)
    c: InternalAlignment(g23,g21)
    c: Block(g15)
    c: Block(g21)
    c: Weight(g24) = 1
    c: Equal(g24,g25)
    c: Equal(g24,g26)
    c: InternalAlignment(g24,g27)
    c: InternalAlignment(g25,g27)
    c: InternalAlignment(g26,g27)
    c: InternalAlignment(g28,g27)
    c: InternalAlignment(g29,g27)
    c: Block(g27)
    c: Weight(g30) = 1
    c: Equal(g30,g31)
    c: Equal(g30,g32)
    c: InternalAlignment(g30,g33)
    c: InternalAlignment(g31,g33)
    c: InternalAlignment(g32,g33)
    c: InternalAlignment(g34,g33)
    c: InternalAlignment(g35,g33)
    c: Block(g33)
    c: Weight(g36) = 1
    c: Equal(g36,g37)
    c: Equal(g36,g38)
    c: InternalAlignment(g36,g39)
    c: InternalAlignment(g37,g39)
    c: InternalAlignment(g38,g39)
    c: InternalAlignment(g40,g39)
    c: InternalAlignment(g41,g39)
    c: Weight(g42) = 1
    c: Equal(g42,g43)
    c: Equal(g42,g44)
    c: InternalAlignment(g42,g45)
    c: InternalAlignment(g43,g45)
    c: InternalAlignment(g44,g45)
    c: InternalAlignment(g46,g45)
    c: InternalAlignment(g47,g45)
    c: Block(g45)
    c: Block(g39)
    c: Vertical(g48)
    c: Distance(g48) = 3
    c: Weight(g49) = 1
    c: Equal(g49,g50)
    c: Equal(g49,g51)
    c: Equal(g49,g52)
    c: Coincident(g53,g48)
    c: InternalAlignment(g49-g52 -> g53) x4
    c: InternalAlignment(g54,g53)
    c: InternalAlignment(g55,g53)
    c: InternalAlignment(g56,g53)
    c: Weight(g57) = 1
    c: Equal(g57, g58-g61) x4
    c: InternalAlignment(g57-g61 -> g62) x5
    c: InternalAlignment(g63,g62)
    c: InternalAlignment(g64,g62)
    c: InternalAlignment(g65,g62)
    c: Block(g62)
    c: Block(g67)
    c: Block(g68)
    c: Distance(g69) = 2.41
    c: Distance(g70) = 2.76
    c: Distance(g71) = 2.5
    c: Distance(g72) = 2.5
    c: Block(g66)
    c: Block(g48)
    c: Block(g53)
    c: Coincident(g73,g53)
    c: Vertical(g73)
    c: Distance(g73) = 3
    c: Coincident(g74,g73)
    c: Horizontal(g74)
    c: Distance(g74) = 100
    c: Coincident(g75,g74)
    c: Coincident(g75,g62)
    c: Vertical(g75)
    c: Distance(g75) = 3
    c: Coincident(g76,g62)
    c: Vertical(g76)
    c: Distance(g76) = 3
    c: Coincident(g77,g76)
    c: Coincident(g77,g45)
    c: Horizontal(g77)
    c: Distance(g77) = 42.95
    c: Coincident(g78,g39)
    c: Coincident(g78,g48)
    c: Horizontal(g78)
    c: Distance(g78) = 42.95
    c: Coincident(g79,g39)
    c: Coincident(g79,g9)
    c: Vertical(g79)
    c: Distance(g79) = 93.16
    c: Coincident(g80,g9)
    c: Coincident(g80,g69)
    c: Angle(g80) = 0.693245
    c: Block(g80)
    c: Coincident(g81,g69)
    c: Coincident(g81,g70)
    c: Block(g81)
    c: Coincident(g82,g70)
    c: Coincident(g82,g71)
    c: Block(g82)
    c: Coincident(g83,g71)
    c: Coincident(g83,g33)
    c: Block(g71)
    c: Coincident(g84,g33)
    c: Coincident(g84,g67)
    c: Coincident(g85,g67)
    c: Coincident(g85,g66)
    c: Coincident(g86,g66)
    c: Coincident(g86,g68)
    c: Coincident(g87,g68)
    c: Coincident(g87,g21)
    c: Coincident(g88,g15)
    c: Coincident(g89,g88)
    c: Block(g89)
    c: Coincident(g90,g89)
    c: Block(g90)
    c: Block(g91)
    c: Coincident(g92,g91)
    c: Block(g92)
    c: Coincident(g93,g91)
    c: Coincident(g93,g90)
    c: Block(g93)
    c: Coincident(g94,g92)
    c: Coincident(g94,g27)
    c: Coincident(g95,g27)
    c: Block(g95)
    c: Coincident(g96,g95)
    c: Coincident(g97,g96)
    c: Coincident(g98,g97)
    c: Coincident(g99,g98)
    c: Coincident(g99,g72)
    c: Block(g98)
    c: Block(g96)
    c: Block(g72)
    c: Coincident(g100,g72)
    c: Coincident(g100,g3)
    c: Coincident(g101,g3)
    c: Coincident(g101,g45)
    c: Vertical(g101)
    c: Coincident(g118,g21)
    c: Weight(g102) = 1
    c: Equal(g102, g103-g117) x15
    c: Coincident(g118,g15)
    c: InternalAlignment(g102-g117 -> g118) x16
    c: InternalAlignment(g119-g132 -> g118) x14
    c: Block(g118)
FEATURE [Sketcher::SketchObject] Sketch006  label="leftSideTop"
  FullyConstrained = true
  sketch-geometry (99):
    g0: Circle CenterX=61.1495 CenterY=111.695 CenterZ=0 NormalX=0 NormalY=0 NormalZ=1 AngleXU=0 Radius=1
    g1: Circle CenterX=58.0728 CenterY=114.251 CenterZ=0 NormalX=0 NormalY=0 NormalZ=1 AngleXU=0 Radius=1
    g2: Circle CenterX=58.0728 CenterY=110.251 CenterZ=0 NormalX=0 NormalY=0 NormalZ=1 AngleXU=0 Radius=1
    g3: BSplineCurve PolesCount=3 KnotsCount=2 Degree=2 IsPeriodic=0
    g4: GeomPoint X=61.1495 Y=111.695 Z=0
    g5: GeomPoint X=58.0728 Y=110.251 Z=0
    g6: Circle CenterX=61.5791 CenterY=89.3511 CenterZ=0 NormalX=0 NormalY=0 NormalZ=1 AngleXU=0 Radius=1
    g7: Circle CenterX=58.0728 CenterY=91.2763 CenterZ=0 NormalX=0 NormalY=0 NormalZ=1 AngleXU=0 Radius=1
    g8: Circle CenterX=58.0728 CenterY=95.2763 CenterZ=0 NormalX=0 NormalY=0 NormalZ=1 AngleXU=0 Radius=1
    g9: BSplineCurve PolesCount=3 KnotsCount=2 Degree=2 IsPeriodic=0
    g10: GeomPoint X=61.5791 Y=89.3511 Z=0
    g11: GeomPoint X=58.0728 Y=95.2763 Z=0
    g12: Circle CenterX=62.0728 CenterY=124.221 CenterZ=0 NormalX=0 NormalY=0 NormalZ=1 AngleXU=0 Radius=1
    g13: Circle CenterX=58.0728 CenterY=124.221 CenterZ=0 NormalX=0 NormalY=0 NormalZ=1 AngleXU=0 Radius=1
    g14: Circle CenterX=61.1496 CenterY=121.665 CenterZ=0 NormalX=0 NormalY=0 NormalZ=1 AngleXU=0 Radius=1
    g15: BSplineCurve PolesCount=3 KnotsCount=2 Degree=2 IsPeriodic=0
    g16: GeomPoint X=62.0728 Y=124.221 Z=0
    g17: GeomPoint X=61.1496 Y=121.665 Z=0
    g18: Circle CenterX=61.5791 CenterY=75.4095 CenterZ=0 NormalX=0 NormalY=0 NormalZ=1 AngleXU=0 Radius=1
    g19: Circle CenterX=58.0728 CenterY=77.3346 CenterZ=0 NormalX=0 NormalY=0 NormalZ=1 AngleXU=0 Radius=1
    g20: Circle CenterX=58.0728 CenterY=73.3346 CenterZ=0 NormalX=0 NormalY=0 NormalZ=1 AngleXU=0 Radius=1
    g21: BSplineCurve PolesCount=3 KnotsCount=2 Degree=2 IsPeriodic=0
    g22: GeomPoint X=61.5791 Y=75.4095 Z=0
    g23: GeomPoint X=58.0728 Y=73.3346 Z=0
    g24: Circle CenterX=2.07281 CenterY=124.221 CenterZ=0 NormalX=0 NormalY=0 NormalZ=1 AngleXU=0 Radius=1
    g25: Circle CenterX=1.57905 CenterY=122.295 CenterZ=0 NormalX=0 NormalY=0 NormalZ=1 AngleXU=0 Radius=1
    g26: BSplineCurve PolesCount=3 KnotsCount=2 Degree=2 IsPeriodic=0
    g27: GeomPoint X=2.07281 Y=124.221 Z=0
    g28: GeomPoint X=1.57905 Y=122.295 Z=0
    g29: Circle CenterX=46.0728 CenterY=124.221 CenterZ=0 NormalX=0 NormalY=0 NormalZ=1 AngleXU=0 Radius=1
    g30: Circle CenterX=46.0728 CenterY=120.221 CenterZ=0 NormalX=0 NormalY=0 NormalZ=1 AngleXU=0 Radius=1
    g31: BSplineCurve PolesCount=3 KnotsCount=2 Degree=2 IsPeriodic=0
    g32: GeomPoint X=42.0728 Y=124.221 Z=0
    g33: GeomPoint X=46.0728 Y=120.221 Z=0
    g34: Circle CenterX=46.0728 CenterY=109.865 CenterZ=0 NormalX=0 NormalY=0 NormalZ=1 AngleXU=0 Radius=1
    g35: Circle CenterX=46.0728 CenterY=105.865 CenterZ=0 NormalX=0 NormalY=0 NormalZ=1 AngleXU=0 Radius=1
    g36: Circle CenterX=42.0728 CenterY=105.865 CenterZ=0 NormalX=0 NormalY=0 NormalZ=1 AngleXU=0 Radius=1
    g37: BSplineCurve PolesCount=3 KnotsCount=2 Degree=2 IsPeriodic=0
    g38: GeomPoint X=46.0728 Y=109.865 Z=0
    g39: GeomPoint X=42.0728 Y=105.865 Z=0
    g40: Circle CenterX=35.5028 CenterY=105.865 CenterZ=0 NormalX=0 NormalY=0 NormalZ=1 AngleXU=0 Radius=1
    g41: Circle CenterX=31.5028 CenterY=105.865 CenterZ=0 NormalX=0 NormalY=0 NormalZ=1 AngleXU=0 Radius=1
    g42: Circle CenterX=27.9965 CenterY=107.79 CenterZ=0 NormalX=0 NormalY=0 NormalZ=1 AngleXU=0 Radius=1
    g43: BSplineCurve PolesCount=3 KnotsCount=2 Degree=2 IsPeriodic=0
    g44: GeomPoint X=35.5028 Y=105.865 Z=0
    g45: GeomPoint X=27.9965 Y=107.79 Z=0
    g46-g50: Circle x5 (B-spline internal-alignment scaffolding for g51; pole/knot coordinates omitted)
    g51: BSplineCurve PolesCount=5 KnotsCount=3 Degree=3 IsPeriodic=0
    g52: GeomPoint X=132.072 Y=133.221 Z=0
    g53: GeomPoint X=141.072 Y=130.221 Z=0
    g54: GeomPoint X=132.072 Y=127.221 Z=0
    g55: ArcOfCircle CenterX=116.562 CenterY=52.0649 CenterZ=0 NormalX=0 NormalY=0 NormalZ=1 AngleXU=0 Radius=4.24264 StartAngle=0.283268 EndAngle=4.99566
    g56: LineSegment StartX=123.967 StartY=69.4706 StartZ=0 EndX=122.37 EndY=67.5474 EndZ=0
    g57: LineSegment StartX=117.293 StartY=71.7641 StartZ=0 EndX=115.591 EndY=69.7147 EndZ=0
    g58: LineSegment StartX=120.669 StartY=65.4973 StartZ=0 EndX=119.072 EndY=63.5741 EndZ=0
    g59: LineSegment StartX=124.73 StartY=54.6766 StartZ=0 EndX=123.265 EndY=51.8068 EndZ=0
    g60: LineSegment StartX=120.377 StartY=46.5474 StartZ=0 EndX=118.934 EndY=43.9178 EndZ=0
    g61: BSplineCurve PolesCount=3 KnotsCount=2 Degree=2 IsPeriodic=0
    g62: BSplineCurve PolesCount=3 KnotsCount=2 Degree=2 IsPeriodic=0
    g63: LineSegment StartX=61.5791 StartY=75.4095 StartZ=0 EndX=118.934 EndY=43.9178 EndZ=0
    g64: LineSegment StartX=117.748 StartY=47.9913 StartZ=0 EndX=120.377 EndY=46.5474 EndZ=0
    g65: LineSegment StartX=120.635 StartY=53.2507 StartZ=0 EndX=123.265 EndY=51.8068 EndZ=0
    g66: LineSegment StartX=124.73 StartY=54.6766 StartZ=0 EndX=61.5791 EndY=89.3511 EndZ=0
    g67: LineSegment StartX=58.0728 StartY=95.2763 StartZ=0 EndX=58.0728 EndY=110.251 EndZ=0
    g68: LineSegment StartX=61.1495 StartY=111.695 StartZ=0 EndX=119.072 EndY=63.5741 EndZ=0
    g69: LineSegment StartX=120.669 StartY=65.4973 StartZ=0 EndX=115.591 EndY=69.7147 EndZ=0
    g70: LineSegment StartX=117.293 StartY=71.7641 StartZ=0 EndX=122.37 EndY=67.5474 EndZ=0
    g71: LineSegment StartX=123.967 StartY=69.4706 StartZ=0 EndX=61.1496 EndY=121.665 EndZ=0
    g72: LineSegment StartX=62.0728 StartY=124.221 StartZ=0 EndX=132.072 EndY=124.221 EndZ=0
    g73: LineSegment StartX=132.072 StartY=127.221 StartZ=0 EndX=132.072 EndY=124.221 EndZ=0
    g74: LineSegment StartX=132.072 StartY=133.221 StartZ=0 EndX=132.072 EndY=136.221 EndZ=0
    g75: LineSegment StartX=132.072 StartY=136.221 StartZ=0 EndX=-42.9272 EndY=136.221 EndZ=0
    g76: LineSegment StartX=2.07281 StartY=124.221 StartZ=0 EndX=42.0728 EndY=124.221 EndZ=0
    g77: LineSegment StartX=46.0728 StartY=120.221 StartZ=0 EndX=46.0728 EndY=109.865 EndZ=0
    g78: LineSegment StartX=42.0728 StartY=105.865 StartZ=0 EndX=35.5028 EndY=105.865 EndZ=0
    g79: LineSegment StartX=27.9965 StartY=107.79 StartZ=0 EndX=1.57905 EndY=122.295 EndZ=0
    g80: LineSegment StartX=-6.92718 StartY=76.4095 StartZ=0 EndX=42.0728 EndY=76.4095 EndZ=0
    g81: LineSegment StartX=-17.9272 StartY=48.2206 StartZ=0 EndX=-17.9272 EndY=58.2206 EndZ=0
    g82: LineSegment StartX=-35.9272 StartY=48.2206 StartZ=0 EndX=-35.9272 EndY=52.2206 EndZ=0
    g83: LineSegment StartX=-29.9272 StartY=48.2206 StartZ=0 EndX=-29.9272 EndY=52.2206 EndZ=0
    g84: LineSegment StartX=-23.9272 StartY=48.2206 StartZ=0 EndX=-23.9272 EndY=58.2206 EndZ=0
    g85: ArcOfCircle CenterX=-32.9272 CenterY=55.2206 CenterZ=0 NormalX=0 NormalY=0 NormalZ=1 AngleXU=0 Radius=4.24264 StartAngle=5.49779 EndAngle=10.2102
    g86: ArcOfCircle CenterX=-20.9272 CenterY=61.2206 CenterZ=0 NormalX=0 NormalY=0 NormalZ=1 AngleXU=0 Radius=4.24264 StartAngle=5.49779 EndAngle=10.2102
    g87: LineSegment StartX=-10.9272 StartY=48.2206 StartZ=0 EndX=-10.9272 EndY=72.4095 EndZ=0
    g88: LineSegment StartX=-42.9272 StartY=48.2206 StartZ=0 EndX=-42.9272 EndY=136.221 EndZ=0
    g89: LineSegment StartX=46.0728 StartY=72.4095 StartZ=0 EndX=46.0728 EndY=-27.5905 EndZ=0
    g90: LineSegment StartX=58.0728 StartY=-27.5905 StartZ=0 EndX=58.0728 EndY=73.3346 EndZ=0
    g91: LineSegment StartX=50.0728 StartY=-27.5905 StartZ=0 EndX=50.0728 EndY=-31.5905 EndZ=0
    g92: LineSegment StartX=54.0728 StartY=-27.5905 StartZ=0 EndX=54.0728 EndY=-31.5905 EndZ=0
    g93: ArcOfCircle CenterX=52.0728 CenterY=-33.5905 CenterZ=0 NormalX=0 NormalY=0 NormalZ=1 AngleXU=0 Radius=2.82843 StartAngle=2.35619 EndAngle=7.06858
    g94: LineSegment StartX=46.0728 StartY=-27.5905 StartZ=0 EndX=50.0728 EndY=-27.5905 EndZ=0
    g95: LineSegment StartX=54.0728 StartY=-27.5905 StartZ=0 EndX=58.0728 EndY=-27.5905 EndZ=0
    g96: LineSegment StartX=-17.9272 StartY=48.2206 StartZ=0 EndX=-10.9272 EndY=48.2206 EndZ=0
    g97: LineSegment StartX=-29.9272 StartY=48.2206 StartZ=0 EndX=-23.9272 EndY=48.2206 EndZ=0
    g98: LineSegment StartX=-42.9272 StartY=48.2206 StartZ=0 EndX=-35.9272 EndY=48.2206 EndZ=0
  constraints (172):
    c: Weight(g0) = 1
    c: Equal(g0,g1)
    c: Equal(g0,g2)
    c: InternalAlignment(g0,g3)
    c: InternalAlignment(g1,g3)
    c: InternalAlignment(g2,g3)
    c: InternalAlignment(g4,g3)
    c: InternalAlignment(g5,g3)
    c: Weight(g6) = 1
    c: Equal(g6,g7)
    c: Equal(g6,g8)
    c: InternalAlignment(g6,g9)
    c: InternalAlignment(g7,g9)
    c: InternalAlignment(g8,g9)
    c: InternalAlignment(g10,g9)
    c: InternalAlignment(g11,g9)
    c: Block(g3)
    c: Block(g9)
    c: Weight(g12) = 1
    c: Equal(g12,g13)
    c: Equal(g12,g14)
    c: InternalAlignment(g12,g15)
    c: InternalAlignment(g13,g15)
    c: InternalAlignment(g14,g15)
    c: InternalAlignment(g16,g15)
    c: InternalAlignment(g17,g15)
    c: Block(g15)
    c: Weight(g18) = 1
    c: Equal(g18,g19)
    c: Equal(g18,g20)
    c: InternalAlignment(g18,g21)
    c: InternalAlignment(g19,g21)
    c: InternalAlignment(g20,g21)
    c: InternalAlignment(g22,g21)
    c: InternalAlignment(g23,g21)
    c: Block(g21)
    c: Weight(g24) = 1
    c: Equal(g24,g25)
    c: InternalAlignment(g24,g26)
    c: InternalAlignment(g25,g26)
    c: InternalAlignment(g27,g26)
    c: InternalAlignment(g28,g26)
    c: InternalAlignment(g29,g31)
    c: InternalAlignment(g30,g31)
    c: InternalAlignment(g32,g31)
    c: InternalAlignment(g33,g31)
    c: Weight(g34) = 1
    c: Equal(g34,g35)
    c: Equal(g34,g36)
    c: InternalAlignment(g34,g37)
    c: InternalAlignment(g35,g37)
    c: InternalAlignment(g36,g37)
    c: InternalAlignment(g38,g37)
    c: InternalAlignment(g39,g37)
    c: Equal(g40,g41)
    c: Equal(g40,g42)
    c: InternalAlignment(g40,g43)
    c: InternalAlignment(g41,g43)
    c: InternalAlignment(g42,g43)
    c: InternalAlignment(g44,g43)
    c: InternalAlignment(g45,g43)
    c: Block(g31)
    c: Block(g37)
    c: Block(g43)
    c: Block(g26)
    c: Weight(g46) = 1
    c: Equal(g46, g47-g50) x4
    c: InternalAlignment(g46-g50 -> g51) x5
    c: InternalAlignment(g52,g51)
    c: InternalAlignment(g53,g51)
    c: InternalAlignment(g54,g51)
    c: Block(g51)
    c: Block(g55)
    c: Block(g56)
    c: Block(g57)
    c: Block(g58)
    c: Block(g59)
    c: Block(g60)
    c: Block(g61)
    c: Block(g62)
    c: Coincident(g90,g21)
    c: Coincident(g63,g21)
    c: Coincident(g63,g60)
    c: Coincident(g64,g55)
    c: Coincident(g64,g60)
    c: Coincident(g65,g55)
    c: Coincident(g65,g59)
    c: Coincident(g66,g59)
    c: Coincident(g66,g9)
    c: Coincident(g67,g9)
    c: Coincident(g67,g3)
    c: Vertical(g67)
    c: Coincident(g68,g3)
    c: Coincident(g68,g58)
    c: Coincident(g69,g58)
    c: Coincident(g69,g57)
    c: Coincident(g70,g57)
    c: Coincident(g70,g56)
    c: Coincident(g71,g56)
    c: Coincident(g71,g15)
    c: Coincident(g72,g15)
    c: Horizontal(g72)
    c: Coincident(g73,g51)
    c: Coincident(g73,g72)
    c: Vertical(g73)
    c: Coincident(g74,g51)
    c: Vertical(g74)
    c: Coincident(g75,g74)
    c: Horizontal(g75)
    c: Coincident(g76,g26)
    c: Coincident(g76,g31)
    c: Horizontal(g76)
    c: Coincident(g77,g31)
    c: Coincident(g77,g37)
    c: Vertical(g77)
    c: Coincident(g78,g37)
    c: Coincident(g78,g43)
    c: Horizontal(g78)
    c: Coincident(g79,g43)
    c: Coincident(g79,g26)
    c: Coincident(g80,g62)
    c: Coincident(g80,g61)
    c: Horizontal(g80)
    c: Vertical(g81)
    c: Distance(g81) = 10
    c: Vertical(g82)
    c: Distance(g82) = 4
    c: Vertical(g83)
    c: Distance(g83) = 4
    c: Vertical(g84)
    c: Distance(g84) = 10
    c: Coincident(g85,g83)
    c: Coincident(g85,g82)
    c: Block(g85)
    c: Coincident(g86,g84)
    c: Coincident(g86,g81)
    c: Block(g86)
    c: Coincident(g87,g62)
    c: Vertical(g87)
    c: Coincident(g88,g75)
    c: Vertical(g88)
    c: Block(g75)
    c: Coincident(g89,g61)
    c: Vertical(g89)
    c: Distance(g89) = 100
    c: Block(g90)
    c: Vertical(g91)
    c: Distance(g91) = 4
    c: Vertical(g92)
    c: Distance(g92) = 4
    c: Coincident(g93,g91)
    c: Coincident(g93,g92)
    c: Block(g93)
    c: Coincident(g94,g89)
    c: Coincident(g94,g91)
    c: Horizontal(g94)
    c: Distance(g94) = 4
    c: Coincident(g95,g92)
    c: Coincident(g95,g90)
    c: Horizontal(g95)
    c: Distance(g95) = 4
    c: Block(g87)
    c: Block(g88)
    c: Coincident(g96,g81)
    c: Coincident(g96,g87)
    c: Horizontal(g96)
    c: Coincident(g97,g83)
    c: Coincident(g97,g84)
    c: Horizontal(g97)
    c: Coincident(g98,g88)
    c: Coincident(g98,g82)
    c: Horizontal(g98)
FEATURE [Sketcher::SketchObject] Sketch007  label="leftSideBottom"
  FullyConstrained = true
  sketch-geometry (92):
    g0: ArcOfCircle CenterX=-26.9272 CenterY=-83.7794 CenterZ=0 NormalX=0 NormalY=0 NormalZ=1 AngleXU=0 Radius=8 StartAngle=3.14159 EndAngle=6.28319
    g1: Circle CenterX=61.5791 CenterY=-56.9099 CenterZ=0 NormalX=0 NormalY=0 NormalZ=1 AngleXU=0 Radius=1
    g2: Circle CenterX=58.0728 CenterY=-58.8351 CenterZ=0 NormalX=0 NormalY=0 NormalZ=1 AngleXU=0 Radius=1
    g3: Circle CenterX=58.0728 CenterY=-62.8351 CenterZ=0 NormalX=0 NormalY=0 NormalZ=1 AngleXU=0 Radius=1
    g4: BSplineCurve PolesCount=3 KnotsCount=2 Degree=2 IsPeriodic=0
    g5: GeomPoint X=61.5791 Y=-56.9099 Z=0
    g6: GeomPoint X=58.0728 Y=-62.8351 Z=0
    g7: Circle CenterX=58.0728 CenterY=-77.8102 CenterZ=0 NormalX=0 NormalY=0 NormalZ=1 AngleXU=0 Radius=1
    g8: Circle CenterX=58.0728 CenterY=-81.8102 CenterZ=0 NormalX=0 NormalY=0 NormalZ=1 AngleXU=0 Radius=1
    g9: Circle CenterX=61.1496 CenterY=-79.2541 CenterZ=0 NormalX=0 NormalY=0 NormalZ=1 AngleXU=0 Radius=1
    g10: BSplineCurve PolesCount=3 KnotsCount=2 Degree=2 IsPeriodic=0
    g11: GeomPoint X=58.0728 Y=-77.8102 Z=0
    g12: GeomPoint X=61.1496 Y=-79.2541 Z=0
    g13: Circle CenterX=61.6457 CenterY=-88.8112 CenterZ=0 NormalX=0 NormalY=0 NormalZ=1 AngleXU=0 Radius=1
    g14: Circle CenterX=58.0728 CenterY=-91.7794 CenterZ=0 NormalX=0 NormalY=0 NormalZ=1 AngleXU=0 Radius=1
    g15: Circle CenterX=63.9135 CenterY=-91.8014 CenterZ=0 NormalX=0 NormalY=0 NormalZ=1 AngleXU=0 Radius=1
    g16: BSplineCurve PolesCount=3 KnotsCount=2 Degree=2 IsPeriodic=0
    g17: GeomPoint X=61.6457 Y=-88.8112 Z=0
    g18: GeomPoint X=63.9135 Y=-91.8014 Z=0
    g19: Circle CenterX=58.0728 CenterY=-40.8935 CenterZ=0 NormalX=0 NormalY=0 NormalZ=1 AngleXU=0 Radius=1
    g20: Circle CenterX=58.0728 CenterY=-44.8935 CenterZ=0 NormalX=0 NormalY=0 NormalZ=1 AngleXU=0 Radius=1
    g21: Circle CenterX=61.5791 CenterY=-42.9683 CenterZ=0 NormalX=0 NormalY=0 NormalZ=1 AngleXU=0 Radius=1
    g22: BSplineCurve PolesCount=3 KnotsCount=2 Degree=2 IsPeriodic=0
    g23: GeomPoint X=58.0728 Y=-40.8935 Z=0
    g24: GeomPoint X=61.5791 Y=-42.9683 Z=0
    g25: Circle CenterX=42.5666 CenterY=-67.3492 CenterZ=0 NormalX=0 NormalY=0 NormalZ=1 AngleXU=0 Radius=1
    g26: Circle CenterX=46.0728 CenterY=-65.424 CenterZ=0 NormalX=0 NormalY=0 NormalZ=1 AngleXU=0 Radius=1
    g27: Circle CenterX=46.0728 CenterY=-69.424 CenterZ=0 NormalX=0 NormalY=0 NormalZ=1 AngleXU=0 Radius=1
    g28: BSplineCurve PolesCount=3 KnotsCount=2 Degree=2 IsPeriodic=0
    g29: GeomPoint X=42.5666 Y=-67.3492 Z=0
    g30: GeomPoint X=46.0728 Y=-69.424 Z=0
    g31: Circle CenterX=2.07281 CenterY=-91.7794 CenterZ=0 NormalX=0 NormalY=0 NormalZ=1 AngleXU=0 Radius=1
    g32: Circle CenterX=-1.92719 CenterY=-91.7794 CenterZ=0 NormalX=0 NormalY=0 NormalZ=1 AngleXU=0 Radius=1
    g33: Circle CenterX=1.57905 CenterY=-89.8542 CenterZ=0 NormalX=0 NormalY=0 NormalZ=1 AngleXU=0 Radius=1
    g34: BSplineCurve PolesCount=3 KnotsCount=2 Degree=2 IsPeriodic=0
    g35: GeomPoint X=2.07281 Y=-91.7794 Z=0
    g36: GeomPoint X=1.57905 Y=-89.8542 Z=0
    g37: ArcOfCircle CenterX=-26.9272 CenterY=22.1087 CenterZ=0 NormalX=0 NormalY=0 NormalZ=1 AngleXU=0 Radius=4 StartAngle=5e-16 EndAngle=3.14159
    g38: Circle CenterX=-10.9272 CenterY=-78.7794 CenterZ=0 NormalX=0 NormalY=0 NormalZ=1 AngleXU=0 Radius=1
    g39: Circle CenterX=-10.9272 CenterY=-82.7794 CenterZ=0 NormalX=0 NormalY=0 NormalZ=1 AngleXU=0 Radius=1
    g40: Circle CenterX=-7.42095 CenterY=-80.8542 CenterZ=0 NormalX=0 NormalY=0 NormalZ=1 AngleXU=0 Radius=1
    g41: BSplineCurve PolesCount=3 KnotsCount=2 Degree=2 IsPeriodic=0
    g42: GeomPoint X=-10.9272 Y=-78.7794 Z=0
    g43: GeomPoint X=-7.42095 Y=-80.8542 Z=0
    g44: BSplineCurve PolesCount=3 KnotsCount=2 Degree=2 IsPeriodic=0
    g45: GeomPoint X=42.5666 Y=-53.4075 Z=0
    g46: GeomPoint X=46.0728 Y=-47.4823 Z=0
    g47: BSplineCurve PolesCount=5 KnotsCount=3 Degree=3 IsPeriodic=0
    g48: LineSegment StartX=124.814 StartY=-22.1885 StartZ=0 EndX=123.265 EndY=-19.3655 EndZ=0
    g49: ArcOfCircle CenterX=116.562 CenterY=-19.6236 CenterZ=0 NormalX=0 NormalY=0 NormalZ=1 AngleXU=0 Radius=4.24264 StartAngle=1.28753 EndAngle=6.00037
    g50: LineSegment StartX=-30.9272 StartY=22.1087 StartZ=0 EndX=-34.9272 EndY=-83.7794 EndZ=0
    g51: LineSegment StartX=-22.9272 StartY=22.1087 StartZ=0 EndX=-18.9272 EndY=-83.7794 EndZ=0
    g52: LineSegment StartX=118.934 StartY=-11.4765 StartZ=0 EndX=120.377 EndY=-14.1062 EndZ=0
    g53: LineSegment StartX=118.86 StartY=-31.3104 StartZ=0 EndX=120.377 EndY=-33.1447 EndZ=0
    g54: LineSegment StartX=115.291 StartY=-37.3514 StartZ=0 EndX=117.05 EndY=-39.4781 EndZ=0
    g55: LineSegment StartX=122.136 StartY=-35.2714 StartZ=0 EndX=123.656 EndY=-37.1092 EndZ=0
    g56: BSplineCurve PolesCount=3 KnotsCount=2 Degree=2 IsPeriodic=0
    g57: LineSegment StartX=132.072 StartY=-100.779 StartZ=0 EndX=132.072 EndY=-103.779 EndZ=0
    g58: LineSegment StartX=132.072 StartY=-91.8014 StartZ=0 EndX=132.072 EndY=-94.7791 EndZ=0
    g59: LineSegment StartX=63.9135 StartY=-91.8014 StartZ=0 EndX=132.072 EndY=-91.8014 EndZ=0
    g60: LineSegment StartX=61.6457 StartY=-88.8112 StartZ=0 EndX=123.656 EndY=-37.1092 EndZ=0
    g61: LineSegment StartX=122.136 StartY=-35.2714 StartZ=0 EndX=117.05 EndY=-39.4781 EndZ=0
    g62: LineSegment StartX=115.291 StartY=-37.3514 StartZ=0 EndX=120.377 EndY=-33.1447 EndZ=0
    g63: LineSegment StartX=118.86 StartY=-31.3104 StartZ=0 EndX=61.1496 EndY=-79.2541 EndZ=0
    g64: LineSegment StartX=58.0728 StartY=-77.8102 StartZ=0 EndX=58.0728 EndY=-62.8351 EndZ=0
    g65: LineSegment StartX=61.5791 StartY=-56.9099 StartZ=0 EndX=124.814 EndY=-22.1885 EndZ=0
    g66: LineSegment StartX=120.636 StartY=-20.8076 StartZ=0 EndX=123.265 EndY=-19.3655 EndZ=0
    g67: LineSegment StartX=117.748 StartY=-15.55 StartZ=0 EndX=120.377 EndY=-14.1062 EndZ=0
    g68: LineSegment StartX=118.934 StartY=-11.4765 StartZ=0 EndX=61.5791 EndY=-42.9683 EndZ=0
    g69: LineSegment StartX=-42.9272 StartY=-103.779 StartZ=0 EndX=132.072 EndY=-103.779 EndZ=0
    g70: LineSegment StartX=42.5666 StartY=-53.4075 StartZ=0 EndX=-7.42095 EndY=-80.8542 EndZ=0
    g71: LineSegment StartX=-10.9272 StartY=-78.7794 StartZ=0 EndX=-10.9272 EndY=48.2206 EndZ=0
    g72: LineSegment StartX=2.07281 StartY=-91.7794 StartZ=0 EndX=42.0728 EndY=-91.7794 EndZ=0
    g73: LineSegment StartX=46.0728 StartY=-87.7794 StartZ=0 EndX=46.0728 EndY=-69.424 EndZ=0
    g74: LineSegment StartX=42.5666 StartY=-67.3492 StartZ=0 EndX=1.57905 EndY=-89.8542 EndZ=0
    g75: LineSegment StartX=-42.9272 StartY=-103.779 StartZ=0 EndX=-42.9272 EndY=48.2206 EndZ=0
    g76: LineSegment StartX=-17.9272 StartY=48.2206 StartZ=0 EndX=-17.9272 EndY=58.2206 EndZ=0
    g77: LineSegment StartX=-35.9272 StartY=48.2206 StartZ=0 EndX=-35.9272 EndY=52.2206 EndZ=0
    g78: LineSegment StartX=-29.9272 StartY=48.2206 StartZ=0 EndX=-29.9272 EndY=52.2206 EndZ=0
    g79: LineSegment StartX=-23.9272 StartY=48.2206 StartZ=0 EndX=-23.9272 EndY=58.2206 EndZ=0
    g80: ArcOfCircle CenterX=-32.9272 CenterY=55.2206 CenterZ=0 NormalX=0 NormalY=0 NormalZ=1 AngleXU=0 Radius=4.24264 StartAngle=5.49779 EndAngle=10.2102
    g81: ArcOfCircle CenterX=-20.9272 CenterY=61.2206 CenterZ=0 NormalX=0 NormalY=0 NormalZ=1 AngleXU=0 Radius=4.24264 StartAngle=5.49779 EndAngle=10.2102
    g82: LineSegment StartX=-17.9272 StartY=48.2206 StartZ=0 EndX=-10.9272 EndY=48.2206 EndZ=0
    g83: LineSegment StartX=-42.9272 StartY=48.2206 StartZ=0 EndX=-35.9272 EndY=48.2206 EndZ=0
    g84: LineSegment StartX=50.0728 StartY=-27.5905 StartZ=0 EndX=50.0728 EndY=-31.5905 EndZ=0
    g85: LineSegment StartX=54.0728 StartY=-27.5905 StartZ=0 EndX=54.0728 EndY=-31.5905 EndZ=0
    g86: ArcOfCircle CenterX=52.0728 CenterY=-33.5905 CenterZ=0 NormalX=0 NormalY=0 NormalZ=1 AngleXU=0 Radius=2.82843 StartAngle=2.35619 EndAngle=7.06858
    g87: LineSegment StartX=46.0728 StartY=-27.5905 StartZ=0 EndX=50.0728 EndY=-27.5905 EndZ=0
    g88: LineSegment StartX=54.0728 StartY=-27.5905 StartZ=0 EndX=58.0728 EndY=-27.5905 EndZ=0
    g89: LineSegment StartX=46.0728 StartY=-27.5905 StartZ=0 EndX=46.0728 EndY=-47.4823 EndZ=0
    g90: LineSegment StartX=58.0728 StartY=-27.5905 StartZ=0 EndX=58.0728 EndY=-40.8935 EndZ=0
    g91: LineSegment StartX=-29.9272 StartY=48.2206 StartZ=0 EndX=-23.9272 EndY=48.2206 EndZ=0
  constraints (170):
    c: Weight(g1) = 1
    c: Equal(g1,g2)
    c: Equal(g1,g3)
    c: InternalAlignment(g1,g4)
    c: InternalAlignment(g2,g4)
    c: InternalAlignment(g3,g4)
    c: InternalAlignment(g5,g4)
    c: InternalAlignment(g6,g4)
    c: Weight(g7) = 1
    c: Equal(g7,g8)
    c: Equal(g7,g9)
    c: InternalAlignment(g7,g10)
    c: InternalAlignment(g8,g10)
    c: InternalAlignment(g9,g10)
    c: InternalAlignment(g11,g10)
    c: InternalAlignment(g12,g10)
    c: Block(g4)
    c: Block(g10)
    c: Weight(g13) = 1
    c: Equal(g13,g14)
    c: Equal(g13,g15)
    c: InternalAlignment(g13,g16)
    c: InternalAlignment(g14,g16)
    c: InternalAlignment(g15,g16)
    c: InternalAlignment(g17,g16)
    c: InternalAlignment(g18,g16)
    c: Block(g16)
    c: Weight(g19) = 1
    c: Equal(g19,g20)
    c: Equal(g19,g21)
    c: InternalAlignment(g19,g22)
    c: InternalAlignment(g20,g22)
    c: InternalAlignment(g21,g22)
    c: InternalAlignment(g23,g22)
    c: InternalAlignment(g24,g22)
    c: Block(g22)
    c: Weight(g25) = 1
    c: Equal(g25,g26)
    c: Equal(g25,g27)
    c: InternalAlignment(g25,g28)
    c: InternalAlignment(g26,g28)
    c: InternalAlignment(g27,g28)
    c: InternalAlignment(g29,g28)
    c: InternalAlignment(g30,g28)
    c: Weight(g31) = 1
    c: Equal(g31,g32)
    c: Equal(g31,g33)
    c: InternalAlignment(g31,g34)
    c: InternalAlignment(g32,g34)
    c: InternalAlignment(g33,g34)
    c: InternalAlignment(g35,g34)
    c: InternalAlignment(g36,g34)
    c: Block(g34)
    c: Block(g28)
    c: Block(g37)
    c: Block(g0)
    c: Weight(g38) = 1
    c: Equal(g38,g40)
    c: InternalAlignment(g38,g41)
    c: InternalAlignment(g39,g41)
    c: InternalAlignment(g40,g41)
    c: InternalAlignment(g42,g41)
    c: InternalAlignment(g43,g41)
    c: InternalAlignment(g45,g44)
    c: InternalAlignment(g46,g44)
    c: Block(g47)
    c: Block(g44)
    c: Block(g41)
    c: Block(g48)
    c: Block(g49)
    c: Coincident(g50,g37)
    c: Coincident(g50,g0)
    c: Coincident(g51,g37)
    c: Coincident(g51,g0)
    c: Block(g51)
    c: Block(g50)
    c: Block(g52)
    c: Block(g53)
    c: Block(g54)
    c: Block(g55)
    c: Block(g56)
    c: Coincident(g57,g47)
    c: Vertical(g57)
    c: Coincident(g58,g47)
    c: Vertical(g58)
    c: Coincident(g59,g16)
    c: Coincident(g59,g58)
    c: Horizontal(g59)
    c: Coincident(g60,g16)
    c: Coincident(g60,g55)
    c: Coincident(g61,g55)
    c: Coincident(g61,g54)
    c: Coincident(g62,g54)
    c: Coincident(g62,g53)
    c: Coincident(g63,g53)
    c: Coincident(g63,g10)
    c: Coincident(g64,g10)
    c: Coincident(g64,g4)
    c: Vertical(g64)
    c: Coincident(g65,g4)
    c: Coincident(g65,g48)
    c: Coincident(g66,g49)
    c: Coincident(g66,g48)
    c: Coincident(g67,g49)
    c: Coincident(g67,g52)
    c: Coincident(g68,g52)
    c: Coincident(g68,g22)
    c: Coincident(g69,g57)
    c: Horizontal(g69)
    c: Coincident(g70,g44)
    c: Coincident(g70,g41)
    c: Coincident(g71,g41)
    c: Vertical(g71)
    c: Coincident(g72,g34)
    c: Coincident(g72,g56)
    c: Horizontal(g72)
    c: Coincident(g73,g56)
    c: Coincident(g73,g28)
    c: Vertical(g73)
    c: Coincident(g74,g28)
    c: Coincident(g74,g34)
    c: Block(g69)
    c: Coincident(g75,g69)
    c: Vertical(g75)
    c: Distance(g75) = 152
    c: Block(g71)
    c: Vertical(g76)
    c: Distance(g76) = 10
    c: Vertical(g77)
    c: Distance(g77) = 4
    c: Vertical(g78)
    c: Distance(g78) = 4
    c: Vertical(g79)
    c: Distance(g79) = 10
    c: Coincident(g80,g78)
    c: Coincident(g80,g77)
    c: Block(g80)
    c: Coincident(g81,g79)
    c: Coincident(g81,g76)
    c: Block(g81)
    c: Coincident(g82,g76)
    c: Coincident(g82,g71)
    c: Horizontal(g82)
    c: Coincident(g83,g75)
    c: Coincident(g83,g77)
    c: Horizontal(g83)
    c: Distance(g83) = 7
    c: Distance(g82) = 7
    c: Vertical(g84)
    c: Distance(g84) = 4
    c: Vertical(g85)
    c: Distance(g85) = 4
    c: Coincident(g86,g84)
    c: Coincident(g86,g85)
    c: Block(g86)
    c: Coincident(g87,g84)
    c: Horizontal(g87)
    c: Distance(g87) = 4
    c: Coincident(g88,g85)
    c: Horizontal(g88)
    c: Distance(g88) = 4
    c: Coincident(g89,g87)
    c: Coincident(g89,g44)
    c: Vertical(g89)
    c: Coincident(g90,g88)
    c: Coincident(g90,g22)
    c: Vertical(g90)
    c: Coincident(g91,g78)
    c: Coincident(g91,g79)
    c: Horizontal(g91)
FEATURE [Sketcher::SketchObject] Sketch008  label="rightSideTop"
  FullyConstrained = false
  sketch-geometry (108):
    g0: Circle CenterX=302.996 CenterY=111.695 CenterZ=0 NormalX=0 NormalY=0 NormalZ=1 AngleXU=0 Radius=1
    g1: Circle CenterX=306.073 CenterY=114.251 CenterZ=0 NormalX=0 NormalY=0 NormalZ=1 AngleXU=0 Radius=1
    g2: Circle CenterX=306.073 CenterY=110.251 CenterZ=0 NormalX=0 NormalY=0 NormalZ=1 AngleXU=0 Radius=1
    g3: BSplineCurve PolesCount=3 KnotsCount=2 Degree=2 IsPeriodic=0
    g4: GeomPoint X=302.996 Y=111.695 Z=0
    g5: GeomPoint X=306.073 Y=110.251 Z=0
    g6: Circle CenterX=306.073 CenterY=95.2763 CenterZ=0 NormalX=0 NormalY=0 NormalZ=1 AngleXU=0 Radius=1
    g7: Circle CenterX=306.073 CenterY=91.2763 CenterZ=0 NormalX=0 NormalY=0 NormalZ=1 AngleXU=0 Radius=1
    g8: Circle CenterX=302.567 CenterY=89.3511 CenterZ=0 NormalX=0 NormalY=0 NormalZ=1 AngleXU=0 Radius=1
    g9: BSplineCurve PolesCount=3 KnotsCount=2 Degree=2 IsPeriodic=0
    g10: GeomPoint X=306.073 Y=95.2763 Z=0
    g11: GeomPoint X=302.567 Y=89.3511 Z=0
    g12: LineSegment StartX=306.073 StartY=110.251 StartZ=0 EndX=306.073 EndY=95.2763 EndZ=0
    g13: Circle CenterX=302.073 CenterY=124.221 CenterZ=0 NormalX=0 NormalY=0 NormalZ=1 AngleXU=0 Radius=1
    g14: Circle CenterX=306.073 CenterY=124.221 CenterZ=0 NormalX=0 NormalY=0 NormalZ=1 AngleXU=0 Radius=1
    g15: Circle CenterX=302.996 CenterY=121.665 CenterZ=0 NormalX=0 NormalY=0 NormalZ=1 AngleXU=0 Radius=1
    g16: BSplineCurve PolesCount=3 KnotsCount=2 Degree=2 IsPeriodic=0
    g17: GeomPoint X=302.073 Y=124.221 Z=0
    g18: GeomPoint X=302.996 Y=121.665 Z=0
    g19: Circle CenterX=306.073 CenterY=73.3346 CenterZ=0 NormalX=0 NormalY=0 NormalZ=1 AngleXU=0 Radius=1
    g20: Circle CenterX=306.073 CenterY=77.3346 CenterZ=0 NormalX=0 NormalY=0 NormalZ=1 AngleXU=0 Radius=1
    g21: Circle CenterX=302.535 CenterY=75.4095 CenterZ=0 NormalX=0 NormalY=0 NormalZ=1 AngleXU=0 Radius=1
    g22: BSplineCurve PolesCount=3 KnotsCount=2 Degree=2 IsPeriodic=0
    g23: GeomPoint X=306.073 Y=73.3346 Z=0
    g24: GeomPoint X=302.535 Y=75.4095 Z=0
    g25: Circle CenterX=362.073 CenterY=124.221 CenterZ=0 NormalX=0 NormalY=0 NormalZ=1 AngleXU=0 Radius=1
    g26: Circle CenterX=366.073 CenterY=124.221 CenterZ=0 NormalX=0 NormalY=0 NormalZ=1 AngleXU=0 Radius=1
    g27: Circle CenterX=362.567 CenterY=122.294 CenterZ=0 NormalX=0 NormalY=0 NormalZ=1 AngleXU=0 Radius=1
    g28: BSplineCurve PolesCount=3 KnotsCount=2 Degree=2 IsPeriodic=0
    g29: GeomPoint X=362.073 Y=124.221 Z=0
    g30: GeomPoint X=362.567 Y=122.294 Z=0
    g31: Circle CenterX=322.073 CenterY=124.221 CenterZ=0 NormalX=0 NormalY=0 NormalZ=1 AngleXU=0 Radius=1
    g32: Circle CenterX=318.073 CenterY=124.221 CenterZ=0 NormalX=0 NormalY=0 NormalZ=1 AngleXU=0 Radius=1
    g33: Circle CenterX=318.073 CenterY=120.221 CenterZ=0 NormalX=0 NormalY=0 NormalZ=1 AngleXU=0 Radius=1
    g34: BSplineCurve PolesCount=3 KnotsCount=2 Degree=2 IsPeriodic=0
    g35: GeomPoint X=322.073 Y=124.221 Z=0
    g36: GeomPoint X=318.073 Y=120.221 Z=0
    g37: Circle CenterX=322.073 CenterY=105.865 CenterZ=0 NormalX=0 NormalY=0 NormalZ=1 AngleXU=0 Radius=1
    g38: Circle CenterX=318.073 CenterY=105.865 CenterZ=0 NormalX=0 NormalY=0 NormalZ=1 AngleXU=0 Radius=1
    g39: Circle CenterX=318.073 CenterY=109.865 CenterZ=0 NormalX=0 NormalY=0 NormalZ=1 AngleXU=0 Radius=1
    g40: BSplineCurve PolesCount=3 KnotsCount=2 Degree=2 IsPeriodic=0
    g41: GeomPoint X=322.073 Y=105.865 Z=0
    g42: GeomPoint X=318.073 Y=109.865 Z=0
    g43: Circle CenterX=336.157 CenterY=107.779 CenterZ=0 NormalX=0 NormalY=0 NormalZ=1 AngleXU=0 Radius=1
    g44: Circle CenterX=332.651 CenterY=105.853 CenterZ=0 NormalX=0 NormalY=0 NormalZ=1 AngleXU=0 Radius=1
    g45: Circle CenterX=328.643 CenterY=105.865 CenterZ=0 NormalX=0 NormalY=0 NormalZ=1 AngleXU=0 Radius=1
    g46: BSplineCurve PolesCount=3 KnotsCount=2 Degree=2 IsPeriodic=0
    g47: GeomPoint X=336.157 Y=107.779 Z=0
    g48: GeomPoint X=328.643 Y=105.865 Z=0
    g49: Circle CenterX=322.073 CenterY=76.4095 CenterZ=0 NormalX=0 NormalY=0 NormalZ=1 AngleXU=0 Radius=4
    g50: BSplineCurve PolesCount=3 KnotsCount=2 Degree=2 IsPeriodic=0
    g51: GeomPoint X=318.073 Y=72.4095 Z=0
    g52: GeomPoint X=322.073 Y=76.4095 Z=0
    g53: Circle CenterX=375.073 CenterY=72.4095 CenterZ=0 NormalX=0 NormalY=0 NormalZ=1 AngleXU=0 Radius=1
    g54: Circle CenterX=375.073 CenterY=76.4095 CenterZ=0 NormalX=0 NormalY=0 NormalZ=1 AngleXU=0 Radius=1
    g55: Circle CenterX=371.073 CenterY=76.4095 CenterZ=0 NormalX=0 NormalY=0 NormalZ=1 AngleXU=0 Radius=1
    g56: BSplineCurve PolesCount=3 KnotsCount=2 Degree=2 IsPeriodic=0
    g57: GeomPoint X=375.073 Y=72.4095 Z=0
    g58: GeomPoint X=371.073 Y=76.4095 Z=0
    g59: LineSegment StartX=322.073 StartY=76.4095 StartZ=0 EndX=371.073 EndY=76.4095 EndZ=0
    g60: Circle CenterX=232.072 CenterY=133.221 CenterZ=0 NormalX=0 NormalY=0 NormalZ=1 AngleXU=0 Radius=1
    g61: Circle CenterX=226.072 CenterY=136.221 CenterZ=0 NormalX=0 NormalY=0 NormalZ=1 AngleXU=0 Radius=1
    g62: Circle CenterX=226.072 CenterY=124.221 CenterZ=0 NormalX=0 NormalY=0 NormalZ=1 AngleXU=0 Radius=1
    g63: Circle CenterX=232.072 CenterY=127.221 CenterZ=0 NormalX=0 NormalY=0 NormalZ=1 AngleXU=0 Radius=1
    g64: BSplineCurve PolesCount=5 KnotsCount=3 Degree=3 IsPeriodic=0
    g65: GeomPoint X=232.072 Y=133.221 Z=0
    g66: GeomPoint X=223.072 Y=130.221 Z=0
    g67: GeomPoint X=232.072 Y=127.221 Z=0
    g68: LineSegment StartX=240.687 StartY=51.8263 StartZ=0 EndX=243.317 EndY=53.2701 EndZ=0
    g69: LineSegment StartX=243.575 StartY=46.5669 StartZ=0 EndX=246.205 EndY=48.0108 EndZ=0
    g70: ArcOfCircle CenterX=247.391 CenterY=52.0843 CenterZ=0 NormalX=0 NormalY=0 NormalZ=1 AngleXU=0 Radius=4.24264 StartAngle=4.42912 EndAngle=9.14151
    g71: LineSegment StartX=243.475 StartY=65.4951 StartZ=0 EndX=245.073 EndY=63.5726 EndZ=0
    g72: LineSegment StartX=243.575 StartY=46.5669 StartZ=0 EndX=245.072 EndY=43.8408 EndZ=0
    g73: LineSegment StartX=245.072 StartY=43.8408 StartZ=0 EndX=302.535 EndY=75.4095 EndZ=0
    g74: LineSegment StartX=239.192 StartY=54.5542 StartZ=0 EndX=302.567 EndY=89.3511 EndZ=0
    g75: LineSegment StartX=232.072 StartY=127.221 StartZ=0 EndX=232.072 EndY=124.221 EndZ=0
    g76: LineSegment StartX=232.072 StartY=136.221 StartZ=0 EndX=232.072 EndY=133.221 EndZ=0
    g77: LineSegment StartX=232.072 StartY=136.221 StartZ=0 EndX=407.073 EndY=136.221 EndZ=0
    g78: LineSegment StartX=322.073 StartY=124.221 StartZ=0 EndX=362.073 EndY=124.221 EndZ=0
    g79: LineSegment StartX=362.567 StartY=122.294 StartZ=0 EndX=336.157 EndY=107.779 EndZ=0
    g80: LineSegment StartX=322.073 StartY=105.865 StartZ=0 EndX=328.643 EndY=105.865 EndZ=0
    g81: LineSegment StartX=318.073 StartY=120.221 StartZ=0 EndX=318.073 EndY=109.865 EndZ=0
    g82: LineSegment StartX=232.072 StartY=124.221 StartZ=0 EndX=302.073 EndY=124.221 EndZ=0
    g83: LineSegment StartX=302.996 StartY=121.665 StartZ=0 EndX=240.171 EndY=69.471 EndZ=0
    g84: LineSegment StartX=240.171 StartY=69.471 StartZ=0 EndX=241.711 EndY=67.6177 EndZ=0
    g85: LineSegment StartX=241.711 StartY=67.6177 StartZ=0 EndX=246.787 EndY=71.8365 EndZ=0
    g86: LineSegment StartX=246.787 StartY=71.8365 StartZ=0 EndX=248.551 EndY=69.712 EndZ=0
    g87: LineSegment StartX=248.551 StartY=69.712 StartZ=0 EndX=243.475 EndY=65.4951 EndZ=0
    g88: LineSegment StartX=245.073 StartY=63.5726 StartZ=0 EndX=302.996 EndY=111.695 EndZ=0
    g89: LineSegment StartX=239.192 StartY=54.5542 StartZ=0 EndX=240.687 EndY=51.8263 EndZ=0
    g90: LineSegment StartX=375.073 StartY=48.2206 StartZ=0 EndX=382.073 EndY=48.2206 EndZ=0
    g91: LineSegment StartX=407.073 StartY=48.2206 StartZ=0 EndX=400.073 EndY=48.2206 EndZ=0
    g92: LineSegment StartX=394.073 StartY=48.2206 StartZ=0 EndX=394.073 EndY=52.2206 EndZ=0
    g93: LineSegment StartX=388.073 StartY=48.2206 StartZ=0 EndX=388.073 EndY=58.2206 EndZ=0
    g94: ArcOfCircle CenterX=385.073 CenterY=61.2206 CenterZ=0 NormalX=0 NormalY=0 NormalZ=1 AngleXU=0 Radius=4.24264 StartAngle=5.49779 EndAngle=10.2102
    g95: ArcOfCircle CenterX=397.073 CenterY=55.2206 CenterZ=0 NormalX=0 NormalY=0 NormalZ=1 AngleXU=0 Radius=4.24264 StartAngle=5.49779 EndAngle=10.2102
    g96: LineSegment StartX=382.073 StartY=58.2206 StartZ=0 EndX=382.073 EndY=48.2206 EndZ=0
    g97: LineSegment StartX=400.073 StartY=52.2206 StartZ=0 EndX=400.073 EndY=48.2206 EndZ=0
    g98: LineSegment StartX=394.073 StartY=48.2206 StartZ=0 EndX=388.073 EndY=48.2206 EndZ=0
    g99: LineSegment StartX=306.073 StartY=-27.5935 StartZ=0 EndX=310.073 EndY=-27.5935 EndZ=0
    g100: LineSegment StartX=318.073 StartY=-27.5935 StartZ=0 EndX=314.073 EndY=-27.5935 EndZ=0
    g101: LineSegment StartX=310.073 StartY=-27.5935 StartZ=0 EndX=310.073 EndY=-31.5935 EndZ=0
    g102: LineSegment StartX=314.073 StartY=-27.5935 StartZ=0 EndX=314.073 EndY=-31.5935 EndZ=0
    g103: ArcOfCircle CenterX=312.073 CenterY=-33.5935 CenterZ=0 NormalX=0 NormalY=0 NormalZ=1 AngleXU=0 Radius=2.82843 StartAngle=2.35619 EndAngle=7.06858
    g104: LineSegment StartX=375.073 StartY=72.4095 StartZ=0 EndX=375.073 EndY=48.2206 EndZ=0
    g105: LineSegment StartX=407.073 StartY=48.2206 StartZ=0 EndX=407.073 EndY=136.221 EndZ=0
    g106: LineSegment StartX=318.073 StartY=-27.5935 StartZ=0 EndX=318.073 EndY=72.4095 EndZ=0
    g107: LineSegment StartX=306.073 StartY=73.3346 StartZ=0 EndX=306.073 EndY=-27.5935 EndZ=0
  constraints (136):
    c: Weight(g0) = 1
    c: Equal(g0,g1)
    c: Equal(g0,g2)
    c: InternalAlignment(g0,g3)
    c: InternalAlignment(g1,g3)
    c: InternalAlignment(g2,g3)
    c: InternalAlignment(g4,g3)
    c: InternalAlignment(g5,g3)
    c: Weight(g6) = 1
    c: Equal(g6,g7)
    c: Equal(g6,g8)
    c: InternalAlignment(g6,g9)
    c: InternalAlignment(g7,g9)
    c: InternalAlignment(g8,g9)
    c: InternalAlignment(g10,g9)
    c: InternalAlignment(g11,g9)
    c: Block(g3)
    c: Block(g9)
    c: Coincident(g12,g3)
    c: Coincident(g12,g9)
    c: Vertical(g12)
    c: Weight(g13) = 1
    c: Equal(g13,g14)
    c: Equal(g13,g15)
    c: InternalAlignment(g14,g16)
    c: InternalAlignment(g15,g16)
    c: InternalAlignment(g17,g16)
    c: InternalAlignment(g18,g16)
    c: Block(g71)
    c: Block(g72)
    c: Coincident(g73,g72)
    c: Coincident(g73,g22)
    c: Block(g73)
    c: Coincident(g70,g69)
    c: Coincident(g70,g68)
    c: Coincident(g74,g9)
    c: Block(g74)
    c: Distance(g71) = 2.5
    c: Block(g64)
    c: Block(g46)
    c: Block(g59)
    c: Coincident(g75,g64)
    c: Vertical(g75)
    c: Coincident(g76,g64)
    c: Vertical(g76)
    c: Coincident(g77,g76)
    c: Horizontal(g77)
    c: Coincident(g78,g34)
    c: Coincident(g78,g28)
    c: Horizontal(g78)
    c: Coincident(g79,g28)
    c: Coincident(g79,g46)
    c: Coincident(g80,g40)
    c: Coincident(g80,g46)
    c: Horizontal(g80)
    c: Coincident(g81,g34)
    c: Coincident(g81,g40)
    c: Vertical(g81)
    c: Block(g34)
    c: Block(g40)
    c: Block(g28)
    c: Coincident(g82,g75)
    c: Coincident(g82,g16)
    c: Horizontal(g82)
    c: Coincident(g83,g16)
    c: Block(g82)
    c: Block(g83)
    c: Block(g16)
    c: Coincident(g84,g83)
    c: Block(g84)
    c: Coincident(g85,g84)
    c: Block(g85)
    c: Coincident(g86,g85)
    c: Coincident(g87,g86)
    c: Coincident(g87,g71)
    c: Block(g87)
    c: Coincident(g88,g71)
    c: Coincident(g88,g3)
    c: Block(g88)
    c: Coincident(g89,g74)
    c: Coincident(g89,g68)
    c: Block(g70)
    c: Block(g68)
    c: Block(g69)
    c: Block(g22)
    c: Block(g50)
    c: Block(g56)
    c: Horizontal(g90)
    c: Distance(g90) = 7
    c: Horizontal(g91)
    c: Distance(g91) = 7
    c: Vertical(g92)
    c: Distance(g92) = 4
    c: Vertical(g93)
    c: Distance(g93) = 10
    c: Coincident(g94,g93)
    c: Coincident(g95,g92)
    c: Block(g95)
    c: Block(g94)
    c: Coincident(g96,g94)
    c: Coincident(g96,g90)
    c: Vertical(g96)
    c: Coincident(g97,g95)
    c: Coincident(g97,g91)
    c: Vertical(g97)
    c: Coincident(g98,g92)
    c: Coincident(g98,g93)
    c: Horizontal(g98)
    c: Horizontal(g99)
    c: Distance(g99) = 4
    c: Horizontal(g100)
    c: Distance(g100) = 4
    c: Coincident(g101,g99)
    c: Vertical(g101)
    c: Coincident(g102,g100)
    c: Vertical(g102)
    c: Distance(g101) = 4
    c: Distance(g102) = 4
    c: Coincident(g103,g101)
    c: Coincident(g103,g102)
    c: Block(g103)
    c: Coincident(g104,g56)
    c: Coincident(g104,g90)
    c: Vertical(g104)
    c: Block(g104)
    c: Coincident(g105,g91)
    c: Coincident(g105,g77)
    c: Vertical(g105)
    c: Block(g77)
    c: Block(g105)
    c: Coincident(g106,g100)
    c: Coincident(g106,g50)
    c: Vertical(g106)
    c: Coincident(g107,g22)
    c: Coincident(g107,g99)
    c: Vertical(g107)
FEATURE [Sketcher::SketchObject] Sketch009  label="middleBottom"
  FullyConstrained = true
  sketch-geometry (109):
    g0: Circle CenterX=175.022 CenterY=5.37834 CenterZ=0 NormalX=0 NormalY=0 NormalZ=1 AngleXU=0 Radius=1
    g1: Circle CenterX=179.022 CenterY=7.57463 CenterZ=0 NormalX=0 NormalY=0 NormalZ=1 AngleXU=0 Radius=1
    g2: Circle CenterX=179.022 CenterY=5.34704 CenterZ=0 NormalX=0 NormalY=0 NormalZ=1 AngleXU=0 Radius=1
    g3: BSplineCurve PolesCount=3 KnotsCount=2 Degree=2 IsPeriodic=0
    g4: GeomPoint X=175.022 Y=5.37834 Z=0
    g5: GeomPoint X=179.022 Y=5.34704 Z=0
    g6: Circle CenterX=189.124 CenterY=5.37834 CenterZ=0 NormalX=0 NormalY=0 NormalZ=1 AngleXU=0 Radius=1
    g7: Circle CenterX=185.124 CenterY=7.57463 CenterZ=0 NormalX=0 NormalY=0 NormalZ=1 AngleXU=0 Radius=1
    g8: Circle CenterX=185.124 CenterY=5.34704 CenterZ=0 NormalX=0 NormalY=0 NormalZ=1 AngleXU=0 Radius=1
    g9: BSplineCurve PolesCount=3 KnotsCount=2 Degree=2 IsPeriodic=0
    g10: GeomPoint X=189.124 Y=5.37834 Z=0
    g11: GeomPoint X=185.124 Y=5.34704 Z=0
    g12: Circle CenterX=224.513 CenterY=-14.0532 CenterZ=0 NormalX=0 NormalY=0 NormalZ=1 AngleXU=0 Radius=1
    g13: Circle CenterX=236.584 CenterY=-24.2775 CenterZ=0 NormalX=0 NormalY=0 NormalZ=1 AngleXU=0 Radius=1
    g14: BSplineCurve PolesCount=3 KnotsCount=2 Degree=2 IsPeriodic=0
    g15: GeomPoint X=236.584 Y=-24.2775 Z=0
    g16: Circle CenterX=125.607 CenterY=-21.7539 CenterZ=0 NormalX=0 NormalY=0 NormalZ=1 AngleXU=0 Radius=1
    g17: Circle CenterX=139.632 CenterY=-14.0532 CenterZ=0 NormalX=0 NormalY=0 NormalZ=1 AngleXU=0 Radius=1
    g18: Circle CenterX=127.325 CenterY=-24.2775 CenterZ=0 NormalX=0 NormalY=0 NormalZ=1 AngleXU=0 Radius=1
    g19: BSplineCurve PolesCount=3 KnotsCount=2 Degree=2 IsPeriodic=0
    g20: GeomPoint X=125.607 Y=-21.7539 Z=0
    g21: GeomPoint X=127.325 Y=-24.2775 Z=0
    g22: Circle CenterX=179.022 CenterY=-85.8163 CenterZ=0 NormalX=0 NormalY=0 NormalZ=1 AngleXU=0 Radius=1
    g23: Circle CenterX=179.022 CenterY=-91.7794 CenterZ=0 NormalX=0 NormalY=0 NormalZ=1 AngleXU=0 Radius=1
    g24: Circle CenterX=171.895 CenterY=-91.8014 CenterZ=0 NormalX=0 NormalY=0 NormalZ=1 AngleXU=0 Radius=1
    g25: BSplineCurve PolesCount=3 KnotsCount=2 Degree=2 IsPeriodic=0
    g26: GeomPoint X=179.022 Y=-85.8163 Z=0
    g27: GeomPoint X=171.895 Y=-91.8014 Z=0
    g28: Circle CenterX=185.124 CenterY=-86.2028 CenterZ=0 NormalX=0 NormalY=0 NormalZ=1 AngleXU=0 Radius=1
    g29: Circle CenterX=185.124 CenterY=-91.7794 CenterZ=0 NormalX=0 NormalY=0 NormalZ=1 AngleXU=0 Radius=1
    g30: Circle CenterX=191.747 CenterY=-91.7794 CenterZ=0 NormalX=0 NormalY=0 NormalZ=1 AngleXU=0 Radius=1
    g31: BSplineCurve PolesCount=3 KnotsCount=2 Degree=2 IsPeriodic=0
    g32: GeomPoint X=185.124 Y=-86.2028 Z=0
    g33: GeomPoint X=191.747 Y=-91.7794 Z=0
    g34: BSplineCurve PolesCount=5 KnotsCount=3 Degree=3 IsPeriodic=0
    g35: LineSegment StartX=132.072 StartY=-100.779 StartZ=0 EndX=132.072 EndY=-103.779 EndZ=0
    g36: GeomPoint X=232.072 Y=-94.7794 Z=0
    g37: GeomPoint X=223.072 Y=-97.7794 Z=0
    g38: Circle CenterX=232.072 CenterY=-94.7794 CenterZ=0 NormalX=0 NormalY=0 NormalZ=1 AngleXU=0 Radius=1
    g39: Circle CenterX=232.072 CenterY=-100.779 CenterZ=0 NormalX=0 NormalY=0 NormalZ=1 AngleXU=0 Radius=1
    g40: BSplineCurve PolesCount=5 KnotsCount=3 Degree=3 IsPeriodic=0
    g41: GeomPoint X=232.072 Y=-100.779 Z=0
    g42: LineSegment StartX=123.656 StartY=-37.1092 StartZ=0 EndX=122.136 EndY=-35.2714 EndZ=0
    g43: LineSegment StartX=117.05 StartY=-39.4781 StartZ=0 EndX=115.291 EndY=-37.3514 EndZ=0
    g44: LineSegment StartX=120.377 StartY=-33.1447 StartZ=0 EndX=118.86 EndY=-31.3104 EndZ=0
    g45: ArcOfCircle CenterX=116.562 CenterY=-19.6236 CenterZ=0 NormalX=0 NormalY=0 NormalZ=1 AngleXU=0 Radius=4.24264 StartAngle=1.28753 EndAngle=5.99992
    g46: LineSegment StartX=240.266 StartY=-37.1092 StartZ=0 EndX=189.124 EndY=5.37834 EndZ=0
    g47: LineSegment StartX=191.747 StartY=-91.7794 StartZ=0 EndX=232.072 EndY=-91.7794 EndZ=0
    g48: LineSegment StartX=232.072 StartY=-91.7794 StartZ=0 EndX=232.072 EndY=-94.7794 EndZ=0
    g49: LineSegment StartX=232.072 StartY=-100.779 StartZ=0 EndX=232.072 EndY=-103.779 EndZ=0
    g50: LineSegment StartX=132.072 StartY=-103.779 StartZ=0 EndX=232.072 EndY=-103.779 EndZ=0
    g51: LineSegment StartX=132.072 StartY=-91.8014 StartZ=0 EndX=132.072 EndY=-94.7791 EndZ=0
    g52: LineSegment StartX=132.072 StartY=-91.8014 StartZ=0 EndX=171.895 EndY=-91.8014 EndZ=0
    g53: LineSegment StartX=179.022 StartY=-85.8163 StartZ=0 EndX=179.022 EndY=5.34704 EndZ=0
    g54: LineSegment StartX=175.022 StartY=5.37834 StartZ=0 EndX=123.656 EndY=-37.1092 EndZ=0
    g55: LineSegment StartX=185.124 StartY=5.34704 StartZ=0 EndX=185.124 EndY=-86.2028 EndZ=0
    g56: LineSegment StartX=122.136 StartY=-35.2714 StartZ=0 EndX=117.05 EndY=-39.4781 EndZ=0
    g57: LineSegment StartX=115.291 StartY=-37.3514 StartZ=0 EndX=120.377 EndY=-33.1447 EndZ=0
    g58: LineSegment StartX=118.86 StartY=-31.3104 StartZ=0 EndX=127.325 EndY=-24.2775 EndZ=0
    g59: LineSegment StartX=125.607 StartY=-21.7539 StartZ=0 EndX=124.815 EndY=-22.1887 EndZ=0
    g60: LineSegment StartX=123.265 StartY=-19.3655 StartZ=0 EndX=124.815 EndY=-22.1887 EndZ=0
    g61: LineSegment StartX=120.636 StartY=-20.8094 StartZ=0 EndX=123.265 EndY=-19.3655 EndZ=0
    g62: LineSegment StartX=117.748 StartY=-15.55 StartZ=0 EndX=120.377 EndY=-14.1062 EndZ=0
    g63: LineSegment StartX=120.377 StartY=-14.1062 StartZ=0 EndX=118.934 EndY=-11.4765 EndZ=0
    g64: LineSegment StartX=236.584 StartY=-24.2775 StartZ=0 EndX=245.072 EndY=-31.3037 EndZ=0
    g65: LineSegment StartX=245.072 StartY=-31.3037 StartZ=0 EndX=243.535 EndY=-33.1602 EndZ=0
    g66: LineSegment StartX=243.535 StartY=-33.1602 StartZ=0 EndX=248.619 EndY=-37.3688 EndZ=0
    g67: LineSegment StartX=248.619 StartY=-37.3688 StartZ=0 EndX=246.855 EndY=-39.5064 EndZ=0
    g68: LineSegment StartX=246.855 StartY=-39.5064 StartZ=0 EndX=241.778 EndY=-35.2889 EndZ=0
    g69: LineSegment StartX=241.778 StartY=-35.2889 StartZ=0 EndX=240.266 EndY=-37.1092 EndZ=0
    g70: LineSegment StartX=243.628 StartY=-14.0323 StartZ=0 EndX=246.258 EndY=-15.476 EndZ=0
    g71: LineSegment StartX=240.741 StartY=-19.2917 StartZ=0 EndX=243.37 EndY=-20.7355 EndZ=0
    g72: ArcOfCircle CenterX=247.444 CenterY=-19.5496 CenterZ=0 NormalX=0 NormalY=0 NormalZ=1 AngleXU=0 Radius=4.24264 StartAngle=3.4249 EndAngle=8.13729
    g73: LineSegment StartX=240.741 StartY=-19.2917 StartZ=0 EndX=239.201 EndY=-22.0968 EndZ=0
    g74: LineSegment StartX=238.538 StartY=-21.7516 StartZ=0 EndX=239.201 EndY=-22.0968 EndZ=0
    g75: LineSegment StartX=245.072 StartY=-11.4025 StartZ=0 EndX=243.628 EndY=-14.0323 EndZ=0
    g76-g91: Circle x16 (B-spline internal-alignment scaffolding for g92; pole/knot coordinates omitted)
    g92: BSplineCurve PolesCount=16 KnotsCount=14 Degree=3 IsPeriodic=0
    g93-g106: GeomPoint x14 (B-spline internal-alignment scaffolding for g92; pole/knot coordinates omitted)
    g107: LineSegment StartX=165.871 StartY=14.2956 StartZ=0 EndX=118.934 EndY=-11.4765 EndZ=0
    g108: LineSegment StartX=198.264 StartY=14.2963 StartZ=0 EndX=245.072 EndY=-11.4025 EndZ=0
  constraints (146):
    c: Weight(g0) = 1
    c: Equal(g0,g1)
    c: Equal(g0,g2)
    c: InternalAlignment(g0,g3)
    c: InternalAlignment(g1,g3)
    c: InternalAlignment(g2,g3)
    c: InternalAlignment(g4,g3)
    c: InternalAlignment(g5,g3)
    c: Weight(g6) = 1
    c: Equal(g6,g7)
    c: Equal(g6,g8)
    c: InternalAlignment(g6,g9)
    c: InternalAlignment(g7,g9)
    c: InternalAlignment(g8,g9)
    c: InternalAlignment(g10,g9)
    c: InternalAlignment(g11,g9)
    c: Block(g9)
    c: Block(g3)
    c: InternalAlignment(g12,g14)
    c: InternalAlignment(g13,g14)
    c: InternalAlignment(g15,g14)
    c: Block(g14)
    c: Weight(g16) = 1
    c: Equal(g16,g17)
    c: Equal(g16,g18)
    c: InternalAlignment(g16,g19)
    c: InternalAlignment(g17,g19)
    c: InternalAlignment(g18,g19)
    c: InternalAlignment(g20,g19)
    c: InternalAlignment(g21,g19)
    c: Block(g19)
    c: Weight(g22) = 1
    c: Equal(g22,g23)
    c: Equal(g22,g24)
    c: InternalAlignment(g22,g25)
    c: InternalAlignment(g23,g25)
    c: InternalAlignment(g24,g25)
    c: InternalAlignment(g26,g25)
    c: InternalAlignment(g27,g25)
    c: Weight(g28) = 1
    c: Equal(g28,g29)
    c: Equal(g28,g30)
    c: InternalAlignment(g28,g31)
    c: InternalAlignment(g29,g31)
    c: InternalAlignment(g30,g31)
    c: InternalAlignment(g32,g31)
    c: InternalAlignment(g33,g31)
    c: Block(g31)
    c: Block(g25)
    c: Block(g34)
    c: Coincident(g35,g34)
    c: Vertical(g35)
    c: Block(g35)
    c: Equal(g38,g39)
    c: InternalAlignment(g38,g40)
    c: InternalAlignment(g39,g40)
    c: InternalAlignment(g36,g40)
    c: InternalAlignment(g37,g40)
    c: InternalAlignment(g41,g40)
    c: Block(g40)
    c: Distance(g42) = 2.385
    c: Distance(g43) = 2.76
    c: Parallel(g42,g44)
    c: Block(g45)
    c: Coincident(g46,g9)
    c: Coincident(g47,g31)
    c: Horizontal(g47)
    c: Block(g47)
    c: Coincident(g48,g47)
    c: Coincident(g48,g40)
    c: Vertical(g48)
    c: Block(g48)
    c: Coincident(g49,g40)
    c: Vertical(g49)
    c: Block(g49)
    c: Coincident(g50,g35)
    c: Coincident(g50,g49)
    c: Horizontal(g50)
    c: Block(g50)
    c: Coincident(g51,g34)
    c: Vertical(g51)
    c: Coincident(g52,g51)
    c: Coincident(g52,g25)
    c: Horizontal(g52)
    c: Coincident(g53,g25)
    c: Coincident(g53,g3)
    c: Vertical(g53)
    c: Coincident(g54,g3)
    c: Coincident(g54,g42)
    c: Coincident(g55,g9)
    c: Coincident(g55,g31)
    c: Vertical(g55)
    c: Block(g42)
    c: Coincident(g56,g42)
    c: Coincident(g56,g43)
    c: Coincident(g57,g43)
    c: Coincident(g57,g44)
    c: Block(g57)
    c: Block(g56)
    c: Coincident(g58,g44)
    c: Coincident(g58,g19)
    c: Block(g58)
    c: Coincident(g59,g19)
    c: Block(g59)
    c: Coincident(g60,g59)
    c: Block(g60)
    c: Coincident(g61,g45)
    c: Coincident(g61,g60)
    c: Coincident(g62,g45)
    c: Coincident(g63,g62)
    c: Block(g63)
    c: Coincident(g64,g14)
    c: Block(g64)
    c: Coincident(g65,g64)
    c: Coincident(g66,g65)
    c: Coincident(g67,g66)
    c: Coincident(g68,g67)
    c: Coincident(g69,g68)
    c: Coincident(g69,g46)
    c: Block(g46)
    c: Block(g68)
    c: Block(g66)
    c: Distance(g70) = 3
    c: Distance(g71) = 3
    c: Coincident(g72,g70)
    c: Coincident(g72,g71)
    c: Block(g72)
    c: Coincident(g73,g71)
    c: Distance(g73) = 3.2
    c: Coincident(g74,g14)
    c: Coincident(g74,g73)
    c: Coincident(g75,g70)
    c: Block(g75)
    c: Block(g73)
    c: Distance(g63) = 3
    c: Distance(g60) = 3.22077
    c: Weight(g76) = 1
    c: Equal(g76, g77-g91) x15
    c: InternalAlignment(g76-g91 -> g92) x16
    c: InternalAlignment(g93-g106 -> g92) x14
    c: Coincident(g107,g92)
    c: Coincident(g107,g63)
    c: Block(g107)
    c: Block(g92)
    c: Coincident(g108,g92)
    c: Coincident(g108,g75)
FEATURE [Sketcher::SketchObject] Sketch010  label="legBottom"
  FullyConstrained = false
  MapMode = 4
  Placement = pos=(0,0,0) rot=(0.57735,0.57735,0.57735;2.0944rad)
  sketch-geometry (40):
    g0: BSplineCurve PolesCount=3 KnotsCount=2 Degree=2 IsPeriodic=0
    g1: Circle CenterX=-199.665 CenterY=-138.314 CenterZ=0 NormalX=0 NormalY=0 NormalZ=1 AngleXU=0 Radius=1
    g2: GeomPoint X=-199.665 Y=-138.314 Z=0
    g3: LineSegment StartX=-199.665 StartY=-138.314 StartZ=0 EndX=-200.721 EndY=-141.122 EndZ=0
    g4: Circle CenterX=-17.0256 CenterY=-190.268 CenterZ=0 NormalX=0 NormalY=0 NormalZ=1 AngleXU=0 Radius=10.5072
    g5: Circle CenterX=-37.7758 CenterY=-187.672 CenterZ=0 NormalX=0 NormalY=0 NormalZ=1 AngleXU=0 Radius=5.64388
    g6: Circle CenterX=-51.4606 CenterY=-185.091 CenterZ=0 NormalX=0 NormalY=0 NormalZ=1 AngleXU=0 Radius=3.01653
    g7: Circle CenterX=-60.4835 CenterY=-182.688 CenterZ=0 NormalX=0 NormalY=0 NormalZ=1 AngleXU=0 Radius=2.12826
    g8: Circle CenterX=-3.29005 CenterY=-177.662 CenterZ=0 NormalX=0 NormalY=0 NormalZ=1 AngleXU=0 Radius=3.26661
    g9: ArcOfCircle CenterX=11.0205 CenterY=-198.019 CenterZ=0 NormalX=0 NormalY=0 NormalZ=1 AngleXU=0 Radius=13 StartAngle=2.78068 EndAngle=5.92131
    g10: LineSegment StartX=5.08312 StartY=-176.581 StartZ=0 EndX=-1.14188 EndY=-193.429 EndZ=0
    g11: LineSegment StartX=29.4118 StartY=-185.752 StartZ=0 EndX=23.1786 EndY=-202.622 EndZ=0
    g12: ArcOfCircle CenterX=17.2475 CenterY=-181.166 CenterZ=0 NormalX=0 NormalY=0 NormalZ=1 AngleXU=0 Radius=13 StartAngle=5.92268 EndAngle=9.06428
    g13: LineSegment StartX=38.8952 StartY=-231.233 StartZ=0 EndX=-200.721 EndY=-141.122 EndZ=0
    g14: LineSegment StartX=38.8952 StartY=-231.233 StartZ=0 EndX=39.9512 EndY=-228.425 EndZ=0
    g15: ArcOfCircle CenterX=46.9911 CenterY=-209.705 CenterZ=0 NormalX=0 NormalY=0 NormalZ=1 AngleXU=0 Radius=20 StartAngle=2.78766 EndAngle=4.35269
    g16: LineSegment StartX=23.7323 StartY=-126.969 StartZ=0 EndX=17.4091 EndY=-143.817 EndZ=0
    g17: ArcOfCircle CenterX=29.5716 CenterY=-148.408 CenterZ=0 NormalX=0 NormalY=0 NormalZ=1 AngleXU=0 Radius=13 StartAngle=2.78068 EndAngle=5.92131
    g18: ArcOfCircle CenterX=35.8967 CenterY=-131.555 CenterZ=0 NormalX=0 NormalY=0 NormalZ=1 AngleXU=0 Radius=13 StartAngle=5.92268 EndAngle=9.06428
    g19: ArcOfCircle CenterX=48.1805 CenterY=-98.7782 CenterZ=0 NormalX=0 NormalY=0 NormalZ=1 AngleXU=0 Radius=13 StartAngle=2.78068 EndAngle=5.92131
    g20: LineSegment StartX=42.354 StartY=-77.3391 StartZ=0 EndX=36.018 EndY=-94.1875 EndZ=0
    g21: ArcOfCircle CenterX=54.5183 CenterY=-81.9247 CenterZ=0 NormalX=0 NormalY=0 NormalZ=1 AngleXU=0 Radius=13 StartAngle=5.92268 EndAngle=9.06428
    g22: LineSegment StartX=66.6827 StartY=-86.5104 StartZ=0 EndX=60.3386 EndY=-103.381 EndZ=0
    g23: LineSegment StartX=23.1786 StartY=-202.622 StartZ=0 EndX=19.0195 EndY=-213.878 EndZ=0
    g24: ArcOfCircle CenterX=20.184 CenterY=-217.506 CenterZ=0 NormalX=0 NormalY=0 NormalZ=1 AngleXU=0 Radius=3.81084 StartAngle=1.88136 EndAngle=6.80465
    g25: LineSegment StartX=38.4753 StartY=-115.966 StartZ=0 EndX=41.2852 EndY=-117.017 EndZ=0
    g26: ArcOfCircle CenterX=36.3663 CenterY=-113.042 CenterZ=0 NormalX=0 NormalY=0 NormalZ=1 AngleXU=0 Radius=3.60555 StartAngle=0.230024 EndAngle=5.3372
    g27: LineSegment StartX=39.8769 StartY=-112.22 StartZ=0 EndX=42.6867 EndY=-113.271 EndZ=0
    g28: LineSegment StartX=19.9036 StartY=-165.61 StartZ=0 EndX=22.7134 EndY=-166.661 EndZ=0
    g29: ArcOfCircle CenterX=17.7945 CenterY=-162.686 CenterZ=0 NormalX=0 NormalY=0 NormalZ=1 AngleXU=0 Radius=3.60555 StartAngle=0.230024 EndAngle=5.3372
    g30: LineSegment StartX=21.3051 StartY=-161.864 StartZ=0 EndX=24.1149 EndY=-162.915 EndZ=0
    g31: LineSegment StartX=41.085 StartY=-66.3176 StartZ=0 EndX=46.0385 EndY=-62.5254 EndZ=0
    g32: LineSegment StartX=48.9563 StartY=-66.3367 StartZ=0 EndX=44.7488 EndY=-73.3482 EndZ=0
    g33: ArcOfCircle CenterX=49.8795 CenterY=-62.6074 CenterZ=0 NormalX=0 NormalY=0 NormalZ=1 AngleXU=0 Radius=3.84187 StartAngle=4.46973 EndAngle=9.40343
    g34: LineSegment StartX=28.2308 StartY=-202.773 StartZ=0 EndX=23.4884 EndY=-215.608 EndZ=0
    g35: LineSegment StartX=41.085 StartY=-66.3176 StartZ=0 EndX=8.65492 EndY=-152.553 EndZ=0
    g36: LineSegment StartX=43.5724 StartY=-110.934 StartZ=0 EndX=42.6867 EndY=-113.271 EndZ=0
    g37: LineSegment StartX=40.4148 StartY=-119.365 StartZ=0 EndX=41.2852 EndY=-117.017 EndZ=0
    g38: LineSegment StartX=21.8316 StartY=-169.001 StartZ=0 EndX=22.7134 EndY=-166.661 EndZ=0
    g39: LineSegment StartX=24.9948 StartY=-160.575 StartZ=0 EndX=24.1149 EndY=-162.915 EndZ=0
  constraints (72):
    c: Block(g9)
    c: Block(g12)
    c: InternalAlignment(g1,g0)
    c: InternalAlignment(g2,g0)
    c: Block(g0)
    c: Block(g4)
    c: Block(g8)
    c: Block(g5)
    c: Block(g6)
    c: Block(g7)
    c: Block(g15)
    c: Coincident(g14,g13)
    c: Coincident(g14,g15)
    c: Block(g14)
    c: Coincident(g3,g0)
    c: Coincident(g3,g13)
    c: Block(g13)
    c: Coincident(g10,g12)
    c: Coincident(g10,g9)
    c: Coincident(g11,g12)
    c: Coincident(g11,g9)
    c: Block(g17)
    c: Block(g18)
    c: Coincident(g16,g18)
    c: Coincident(g16,g17)
    c: Block(g19)
    c: Block(g21)
    c: Coincident(g20,g21)
    c: Coincident(g20,g19)
    c: Coincident(g22,g21)
    c: Coincident(g22,g19)
    c: Coincident(g23,g9)
    c: Parallel(g11,g23)
    c: Distance(g23) = 12
    c: Block(g11)
    c: Coincident(g24,g23)
    c: Block(g24)
    c: Block(g26)
    c: Coincident(g27,g26)
    c: Coincident(g25,g26)
    c: Parallel(g27,g25)
    c: Block(g25)
    c: Block(g27)
    c: Block(g29)
    c: Coincident(g30,g29)
    c: Coincident(g28,g29)
    c: Parallel(g30,g28)
    c: Block(g28)
    c: Block(g30)
    c: Block(g31)
    c: PointOnObject(g32,g21)
    c: Coincident(g33,g31)
    c: Coincident(g33,g32)
    c: Block(g33)
    c: Coincident(g34,g15)
    c: Coincident(g34,g24)
    c: Tangent(g34,g15)
    c: Coincident(g35,g31)
    c: Coincident(g35,g0)
    c: Block(g32)
    c: Coincident(g36,g27)
    c: PointOnObject(g36,g19)
    c: Block(g36)
    c: Coincident(g37,g25)
    c: PointOnObject(g37,g18)
    c: Block(g37)
    c: Coincident(g38,g28)
    c: Coincident(g39,g30)
    c: PointOnObject(g39,g17)
    c: PointOnObject(g38,g12)
    c: Block(g39)
    c: Block(g38)
